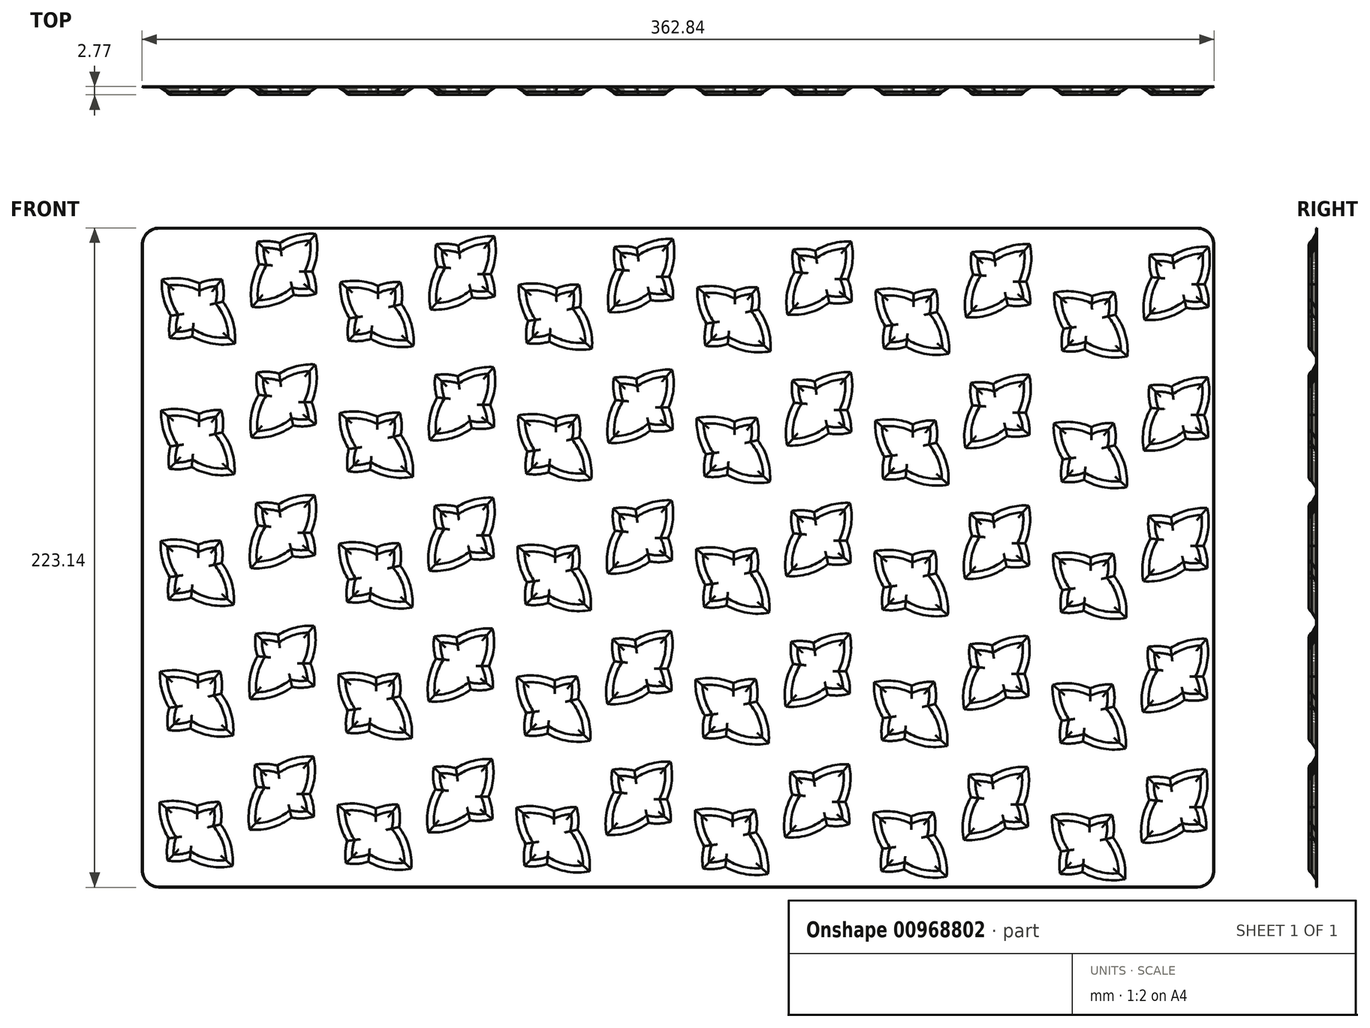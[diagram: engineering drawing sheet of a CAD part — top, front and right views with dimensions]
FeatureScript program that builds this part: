
annotation { "Feature Type Name" : "Feature", "Feature Type Description" : "" }
export const myFeature = defineFeature(function(context is Context, id is Id, definition is map)
    precondition{}
    {
        {
            var Q0;
            Q0=qCreatedBy(makeId("Front.planeOp"),FACE);
            var sketch = newSketch(context, id + "F0", { "sketchPlane" : qUnion([Q0])});
            skLineSegment(sketch, "E0.bottom", {"start": v(175.68, 113.88) * mm, "end": v(-175.68, 113.88) * mm});
            skLineSegment(sketch, "E0.top", {"start": v(175.68, -113.88) * mm, "end": v(-175.68, -113.88) * mm});
            skLineSegment(sketch, "E0.left", {"start": v(183.73, 105.83) * mm, "end": v(183.73, -105.83) * mm});
            skLineSegment(sketch, "E0.right", {"start": v(-183.73, 105.83) * mm, "end": v(-183.73, -105.83) * mm});
            skPoint(sketch, "E1.visualSharp", {"position": v(183.73, 113.88) * mm});
            skArc(sketch, "E1.filletArc", {"start": v(183.73, 105.83) * mm, "mid": v(181.37, 111.52) * mm, "end": v(175.68, 113.88) * mm});
            skPoint(sketch, "E2.visualSharp", {"position": v(-183.73, 113.88) * mm});
            skArc(sketch, "E2.filletArc", {"start": v(-175.68, 113.88) * mm, "mid": v(-181.37, 111.52) * mm, "end": v(-183.73, 105.83) * mm});
            skPoint(sketch, "E3.visualSharp", {"position": v(-183.73, -113.88) * mm});
            skArc(sketch, "E3.filletArc", {"start": v(-183.73, -105.83) * mm, "mid": v(-181.37, -111.52) * mm, "end": v(-175.68, -113.88) * mm});
            skPoint(sketch, "E4.visualSharp", {"position": v(183.73, -113.88) * mm});
            skArc(sketch, "E4.filletArc", {"start": v(175.68, -113.88) * mm, "mid": v(181.37, -111.52) * mm, "end": v(183.73, -105.83) * mm});
            skSolve(sketch);
        }
        {
            var Q0;
            Q0=makeQuery(id+"F0.imprint","IMPRINT",FACE,{"disambiguationData":[TD([[makeQuery(id+"F0.imprint","IMPRINT",EDGE,{"derivedFrom":sQuery(id+"F0.wireOp",EDGE,"E0.bottom")}),1.0]])]});
            var sketch = newSketch(context, id + "F1", { "sketchPlane" : qUnion([Q0])});
            skArc(sketch, "E5.0", {"start": v(-169.28, 82.17) * mm, "mid": v(-169.97, 79.25) * mm, "end": v(-170.06, 76.26) * mm});
            skArc(sketch, "E5.1", {"start": v(-170.4, 90.37) * mm, "mid": v(-169.2, 86.2) * mm, "end": v(-166.97, 82.48) * mm, "construction": true});
            skArc(sketch, "E5.2", {"start": v(-157.93, 89.73) * mm, "mid": v(-160.02, 89.11) * mm, "end": v(-161.98, 88.14) * mm, "construction": true});
            skArc(sketch, "E5.3", {"start": v(-152.04, 74.31) * mm, "mid": v(-153.16, 80.57) * mm, "end": v(-156.38, 86.05) * mm});
            skArc(sketch, "E5.4", {"start": v(-166.97, 82.48) * mm, "mid": v(-167.67, 80.45) * mm, "end": v(-168.03, 78.33) * mm, "construction": true});
            skArc(sketch, "E5.5", {"start": v(-154.2, 76.24) * mm, "mid": v(-155.66, 81.27) * mm, "end": v(-158.67, 85.56) * mm, "construction": true});
            skArc(sketch, "E5.6", {"start": v(-158.67, 85.56) * mm, "mid": v(-158.1, 87.6) * mm, "end": v(-157.93, 89.73) * mm, "construction": true});
            skArc(sketch, "E5.7", {"start": v(-163.98, 79.57) * mm, "mid": v(-159.36, 77.12) * mm, "end": v(-154.2, 76.24) * mm, "construction": true});
            skArc(sketch, "E5.8", {"start": v(-172.6, 92.24) * mm, "mid": v(-171.67, 86.96) * mm, "end": v(-169.28, 82.17) * mm});
            skArc(sketch, "E5.9", {"start": v(-161.98, 90.46) * mm, "mid": v(-167.16, 92.16) * mm, "end": v(-172.6, 92.24) * mm});
            skArc(sketch, "E5.10", {"start": v(-156.38, 86.05) * mm, "mid": v(-155.91, 89.01) * mm, "end": v(-156.12, 92) * mm});
            skArc(sketch, "E5.11", {"start": v(-168.03, 78.33) * mm, "mid": v(-165.95, 78.76) * mm, "end": v(-163.98, 79.57) * mm, "construction": true});
            skArc(sketch, "E5.12", {"start": v(-161.98, 88.14) * mm, "mid": v(-166.03, 89.84) * mm, "end": v(-170.4, 90.37) * mm, "construction": true});
            skArc(sketch, "E5.13", {"start": v(-156.12, 92) * mm, "mid": v(-159.13, 91.54) * mm, "end": v(-161.98, 90.46) * mm});
            skArc(sketch, "E5.14", {"start": v(-170.06, 76.26) * mm, "mid": v(-167.07, 76.41) * mm, "end": v(-164.2, 77.23) * mm});
            skArc(sketch, "E5.15", {"start": v(-164.2, 77.23) * mm, "mid": v(-158.37, 74.72) * mm, "end": v(-152.04, 74.31) * mm});
            skArc(sketch, "E6.0", {"start": v(-124.64, 90.96) * mm, "mid": v(-125.1, 93.98) * mm, "end": v(-126.18, 96.83) * mm});
            skArc(sketch, "E6.1", {"start": v(-138.3, 102.87) * mm, "mid": v(-137.88, 100.8) * mm, "end": v(-137.07, 98.83) * mm, "construction": true});
            skArc(sketch, "E6.2", {"start": v(-126.27, 105.24) * mm, "mid": v(-130.44, 104.05) * mm, "end": v(-134.16, 101.81) * mm, "construction": true});
            skArc(sketch, "E6.3", {"start": v(-131.08, 93.52) * mm, "mid": v(-129.03, 92.95) * mm, "end": v(-126.9, 92.78) * mm, "construction": true});
            skArc(sketch, "E6.4", {"start": v(-134.47, 104.12) * mm, "mid": v(-137.38, 104.82) * mm, "end": v(-140.38, 104.9) * mm});
            skArc(sketch, "E6.5", {"start": v(-139.4, 99.04) * mm, "mid": v(-141.92, 93.22) * mm, "end": v(-142.33, 86.89) * mm});
            skArc(sketch, "E6.6", {"start": v(-142.33, 86.89) * mm, "mid": v(-136.07, 88) * mm, "end": v(-130.58, 91.22) * mm});
            skArc(sketch, "E6.7", {"start": v(-128.5, 96.82) * mm, "mid": v(-126.8, 100.88) * mm, "end": v(-126.27, 105.24) * mm, "construction": true});
            skArc(sketch, "E6.8", {"start": v(-134.16, 101.81) * mm, "mid": v(-136.19, 102.52) * mm, "end": v(-138.3, 102.87) * mm, "construction": true});
            skArc(sketch, "E6.9", {"start": v(-140.4, 89.04) * mm, "mid": v(-135.37, 90.5) * mm, "end": v(-131.08, 93.52) * mm, "construction": true});
            skArc(sketch, "E6.10", {"start": v(-137.07, 98.83) * mm, "mid": v(-139.52, 94.2) * mm, "end": v(-140.4, 89.04) * mm, "construction": true});
            skArc(sketch, "E6.11", {"start": v(-126.9, 92.78) * mm, "mid": v(-127.53, 94.87) * mm, "end": v(-128.5, 96.82) * mm, "construction": true});
            skArc(sketch, "E6.12", {"start": v(-124.4, 107.44) * mm, "mid": v(-129.68, 106.51) * mm, "end": v(-134.47, 104.12) * mm});
            skArc(sketch, "E6.13", {"start": v(-140.38, 104.9) * mm, "mid": v(-140.22, 101.92) * mm, "end": v(-139.4, 99.04) * mm});
            skArc(sketch, "E6.14", {"start": v(-130.58, 91.22) * mm, "mid": v(-127.62, 90.76) * mm, "end": v(-124.64, 90.96) * mm});
            skArc(sketch, "E6.15", {"start": v(-126.18, 96.83) * mm, "mid": v(-124.48, 102) * mm, "end": v(-124.4, 107.44) * mm});
            skArc(sketch, "E7.0.1.0", {"start": v(-152.24, 30.1) * mm, "mid": v(-153.36, 36.35) * mm, "end": v(-156.57, 41.84) * mm});
            skArc(sketch, "E7.0.1.1", {"start": v(-156.57, 41.84) * mm, "mid": v(-156.1, 44.8) * mm, "end": v(-156.31, 47.79) * mm});
            skArc(sketch, "E7.0.1.2", {"start": v(-162.17, 43.93) * mm, "mid": v(-166.23, 45.62) * mm, "end": v(-170.6, 46.15) * mm, "construction": true});
            skArc(sketch, "E7.0.1.3", {"start": v(-164.18, 35.35) * mm, "mid": v(-159.55, 32.9) * mm, "end": v(-154.39, 32.02) * mm, "construction": true});
            skArc(sketch, "E7.0.1.4", {"start": v(-172.8, 48.02) * mm, "mid": v(-171.86, 42.75) * mm, "end": v(-169.47, 37.95) * mm});
            skArc(sketch, "E7.0.1.5", {"start": v(-139.6, 54.82) * mm, "mid": v(-142.11, 49) * mm, "end": v(-142.52, 42.67) * mm});
            skArc(sketch, "E7.0.1.6", {"start": v(-137.26, 54.61) * mm, "mid": v(-139.71, 49.98) * mm, "end": v(-140.6, 44.82) * mm, "construction": true});
            skArc(sketch, "E7.0.1.7", {"start": v(-164.39, 33.02) * mm, "mid": v(-158.57, 30.5) * mm, "end": v(-152.24, 30.1) * mm});
            skArc(sketch, "E7.0.1.8", {"start": v(-162.18, 46.24) * mm, "mid": v(-167.35, 47.94) * mm, "end": v(-172.8, 48.02) * mm});
            skArc(sketch, "E7.0.1.9", {"start": v(-140.6, 44.82) * mm, "mid": v(-135.56, 46.3) * mm, "end": v(-131.28, 49.3) * mm, "construction": true});
            skArc(sketch, "E7.0.1.10", {"start": v(-170.6, 46.15) * mm, "mid": v(-169.4, 41.98) * mm, "end": v(-167.17, 38.26) * mm, "construction": true});
            skArc(sketch, "E7.0.1.11", {"start": v(-154.39, 32.02) * mm, "mid": v(-155.86, 37.05) * mm, "end": v(-158.87, 41.34) * mm, "construction": true});
            skArc(sketch, "E7.0.1.12", {"start": v(-142.52, 42.67) * mm, "mid": v(-136.26, 43.8) * mm, "end": v(-130.78, 47) * mm});
            skArc(sketch, "E7.0.1.13", {"start": v(-124.83, 46.75) * mm, "mid": v(-125.3, 49.76) * mm, "end": v(-126.37, 52.61) * mm});
            skArc(sketch, "E7.0.1.14", {"start": v(-168.22, 34.12) * mm, "mid": v(-166.14, 34.54) * mm, "end": v(-164.18, 35.35) * mm, "construction": true});
            skArc(sketch, "E7.0.1.15", {"start": v(-158.13, 45.51) * mm, "mid": v(-160.22, 44.9) * mm, "end": v(-162.17, 43.93) * mm, "construction": true});
            skArc(sketch, "E7.0.1.16", {"start": v(-134.36, 57.6) * mm, "mid": v(-136.38, 58.3) * mm, "end": v(-138.5, 58.66) * mm, "construction": true});
            skArc(sketch, "E7.0.1.17", {"start": v(-127.1, 48.56) * mm, "mid": v(-127.72, 50.65) * mm, "end": v(-128.7, 52.6) * mm, "construction": true});
            skArc(sketch, "E7.0.1.18", {"start": v(-156.31, 47.79) * mm, "mid": v(-159.33, 47.32) * mm, "end": v(-162.18, 46.24) * mm});
            skArc(sketch, "E7.0.1.19", {"start": v(-170.26, 32.04) * mm, "mid": v(-167.27, 32.2) * mm, "end": v(-164.39, 33.02) * mm});
            skArc(sketch, "E7.0.1.20", {"start": v(-131.28, 49.3) * mm, "mid": v(-129.22, 48.74) * mm, "end": v(-127.1, 48.56) * mm, "construction": true});
            skArc(sketch, "E7.0.1.21", {"start": v(-167.17, 38.26) * mm, "mid": v(-167.87, 36.23) * mm, "end": v(-168.22, 34.12) * mm, "construction": true});
            skArc(sketch, "E7.0.1.22", {"start": v(-158.87, 41.34) * mm, "mid": v(-158.3, 43.4) * mm, "end": v(-158.13, 45.51) * mm, "construction": true});
            skArc(sketch, "E7.0.1.23", {"start": v(-130.78, 47) * mm, "mid": v(-127.82, 46.54) * mm, "end": v(-124.83, 46.75) * mm});
            skArc(sketch, "E7.0.1.24", {"start": v(-169.47, 37.95) * mm, "mid": v(-170.17, 35.04) * mm, "end": v(-170.26, 32.04) * mm});
            skArc(sketch, "E7.0.1.25", {"start": v(-138.5, 58.66) * mm, "mid": v(-138.07, 56.58) * mm, "end": v(-137.26, 54.61) * mm, "construction": true});
            skArc(sketch, "E7.0.1.26", {"start": v(-126.46, 61.03) * mm, "mid": v(-130.64, 59.83) * mm, "end": v(-134.36, 57.6) * mm, "construction": true});
            skArc(sketch, "E7.0.1.27", {"start": v(-124.6, 63.23) * mm, "mid": v(-129.87, 62.3) * mm, "end": v(-134.66, 59.9) * mm});
            skArc(sketch, "E7.0.1.28", {"start": v(-128.7, 52.6) * mm, "mid": v(-127, 56.66) * mm, "end": v(-126.46, 61.03) * mm, "construction": true});
            skArc(sketch, "E7.0.1.29", {"start": v(-126.37, 52.61) * mm, "mid": v(-124.68, 57.79) * mm, "end": v(-124.6, 63.23) * mm});
            skArc(sketch, "E7.0.1.30", {"start": v(-140.58, 60.7) * mm, "mid": v(-140.42, 57.7) * mm, "end": v(-139.6, 54.82) * mm});
            skArc(sketch, "E7.0.1.31", {"start": v(-134.66, 59.9) * mm, "mid": v(-137.58, 60.6) * mm, "end": v(-140.58, 60.7) * mm});
            skArc(sketch, "E7.0.2.0", {"start": v(-152.44, -14.12) * mm, "mid": v(-153.55, -7.86) * mm, "end": v(-156.77, -2.38) * mm});
            skArc(sketch, "E7.0.2.1", {"start": v(-156.77, -2.38) * mm, "mid": v(-156.3, 0.58) * mm, "end": v(-156.5, 3.57) * mm});
            skArc(sketch, "E7.0.2.2", {"start": v(-162.37, -0.29) * mm, "mid": v(-166.42, 1.4) * mm, "end": v(-170.79, 1.94) * mm, "construction": true});
            skArc(sketch, "E7.0.2.3", {"start": v(-164.37, -8.86) * mm, "mid": v(-159.75, -11.31) * mm, "end": v(-154.58, -12.2) * mm, "construction": true});
            skArc(sketch, "E7.0.2.4", {"start": v(-172.99, 3.8) * mm, "mid": v(-172.06, -1.47) * mm, "end": v(-169.67, -6.26) * mm});
            skArc(sketch, "E7.0.2.5", {"start": v(-139.8, 10.6) * mm, "mid": v(-142.3, 4.78) * mm, "end": v(-142.72, -1.54) * mm});
            skArc(sketch, "E7.0.2.6", {"start": v(-137.46, 10.4) * mm, "mid": v(-139.9, 5.77) * mm, "end": v(-140.8, 0.6) * mm, "construction": true});
            skArc(sketch, "E7.0.2.7", {"start": v(-164.58, -11.2) * mm, "mid": v(-158.76, -13.71) * mm, "end": v(-152.44, -14.12) * mm});
            skArc(sketch, "E7.0.2.8", {"start": v(-162.37, 2.03) * mm, "mid": v(-167.55, 3.72) * mm, "end": v(-172.99, 3.8) * mm});
            skArc(sketch, "E7.0.2.9", {"start": v(-140.8, 0.6) * mm, "mid": v(-135.76, 2.08) * mm, "end": v(-131.47, 5.09) * mm, "construction": true});
            skArc(sketch, "E7.0.2.10", {"start": v(-170.79, 1.94) * mm, "mid": v(-169.6, -2.24) * mm, "end": v(-167.36, -5.96) * mm, "construction": true});
            skArc(sketch, "E7.0.2.11", {"start": v(-154.58, -12.2) * mm, "mid": v(-156.05, -7.16) * mm, "end": v(-159.07, -2.87) * mm, "construction": true});
            skArc(sketch, "E7.0.2.12", {"start": v(-142.72, -1.54) * mm, "mid": v(-136.46, -0.42) * mm, "end": v(-130.97, 2.8) * mm});
            skArc(sketch, "E7.0.2.13", {"start": v(-125.03, 2.53) * mm, "mid": v(-125.5, 5.54) * mm, "end": v(-126.57, 8.4) * mm});
            skArc(sketch, "E7.0.2.14", {"start": v(-168.42, -10.1) * mm, "mid": v(-166.34, -9.67) * mm, "end": v(-164.37, -8.86) * mm, "construction": true});
            skArc(sketch, "E7.0.2.15", {"start": v(-158.32, 1.3) * mm, "mid": v(-160.41, 0.68) * mm, "end": v(-162.37, -0.29) * mm, "construction": true});
            skArc(sketch, "E7.0.2.16", {"start": v(-134.55, 13.38) * mm, "mid": v(-136.58, 14.09) * mm, "end": v(-138.7, 14.44) * mm, "construction": true});
            skArc(sketch, "E7.0.2.17", {"start": v(-127.3, 4.35) * mm, "mid": v(-127.92, 6.44) * mm, "end": v(-128.89, 8.4) * mm, "construction": true});
            skArc(sketch, "E7.0.2.18", {"start": v(-156.5, 3.57) * mm, "mid": v(-159.52, 3.1) * mm, "end": v(-162.37, 2.03) * mm});
            skArc(sketch, "E7.0.2.19", {"start": v(-170.45, -12.17) * mm, "mid": v(-167.46, -12.02) * mm, "end": v(-164.58, -11.2) * mm});
            skArc(sketch, "E7.0.2.20", {"start": v(-131.47, 5.09) * mm, "mid": v(-129.42, 4.52) * mm, "end": v(-127.3, 4.35) * mm, "construction": true});
            skArc(sketch, "E7.0.2.21", {"start": v(-167.36, -5.96) * mm, "mid": v(-168.07, -7.98) * mm, "end": v(-168.42, -10.1) * mm, "construction": true});
            skArc(sketch, "E7.0.2.22", {"start": v(-159.07, -2.87) * mm, "mid": v(-158.5, -0.82) * mm, "end": v(-158.32, 1.3) * mm, "construction": true});
            skArc(sketch, "E7.0.2.23", {"start": v(-130.97, 2.8) * mm, "mid": v(-128.02, 2.33) * mm, "end": v(-125.03, 2.53) * mm});
            skArc(sketch, "E7.0.2.24", {"start": v(-169.67, -6.26) * mm, "mid": v(-170.36, -9.18) * mm, "end": v(-170.45, -12.17) * mm});
            skArc(sketch, "E7.0.2.25", {"start": v(-138.7, 14.44) * mm, "mid": v(-138.27, 12.36) * mm, "end": v(-137.46, 10.4) * mm, "construction": true});
            skArc(sketch, "E7.0.2.26", {"start": v(-126.66, 16.81) * mm, "mid": v(-130.83, 15.62) * mm, "end": v(-134.55, 13.38) * mm, "construction": true});
            skArc(sketch, "E7.0.2.27", {"start": v(-124.8, 19.01) * mm, "mid": v(-130.07, 18.08) * mm, "end": v(-134.86, 15.69) * mm});
            skArc(sketch, "E7.0.2.28", {"start": v(-128.89, 8.4) * mm, "mid": v(-127.2, 12.45) * mm, "end": v(-126.66, 16.81) * mm, "construction": true});
            skArc(sketch, "E7.0.2.29", {"start": v(-126.57, 8.4) * mm, "mid": v(-124.87, 13.57) * mm, "end": v(-124.8, 19.01) * mm});
            skArc(sketch, "E7.0.2.30", {"start": v(-140.77, 16.48) * mm, "mid": v(-140.62, 13.49) * mm, "end": v(-139.8, 10.6) * mm});
            skArc(sketch, "E7.0.2.31", {"start": v(-134.86, 15.69) * mm, "mid": v(-137.78, 16.39) * mm, "end": v(-140.77, 16.48) * mm});
            skArc(sketch, "E7.0.3.0", {"start": v(-152.63, -58.33) * mm, "mid": v(-153.75, -52.08) * mm, "end": v(-156.96, -46.6) * mm});
            skArc(sketch, "E7.0.3.1", {"start": v(-156.96, -46.6) * mm, "mid": v(-156.5, -43.63) * mm, "end": v(-156.7, -40.65) * mm});
            skArc(sketch, "E7.0.3.2", {"start": v(-162.56, -44.5) * mm, "mid": v(-166.62, -42.8) * mm, "end": v(-170.98, -42.28) * mm, "construction": true});
            skArc(sketch, "E7.0.3.3", {"start": v(-164.57, -53.08) * mm, "mid": v(-159.94, -55.53) * mm, "end": v(-154.78, -56.4) * mm, "construction": true});
            skArc(sketch, "E7.0.3.4", {"start": v(-173.18, -40.41) * mm, "mid": v(-172.26, -45.69) * mm, "end": v(-169.86, -50.48) * mm});
            skArc(sketch, "E7.0.3.5", {"start": v(-140, -33.61) * mm, "mid": v(-142.5, -39.43) * mm, "end": v(-142.91, -45.76) * mm});
            skArc(sketch, "E7.0.3.6", {"start": v(-137.66, -33.82) * mm, "mid": v(-140.1, -38.45) * mm, "end": v(-140.99, -43.6) * mm, "construction": true});
            skArc(sketch, "E7.0.3.7", {"start": v(-164.78, -55.41) * mm, "mid": v(-158.96, -57.93) * mm, "end": v(-152.63, -58.33) * mm});
            skArc(sketch, "E7.0.3.8", {"start": v(-162.57, -42.19) * mm, "mid": v(-167.74, -40.5) * mm, "end": v(-173.18, -40.41) * mm});
            skArc(sketch, "E7.0.3.9", {"start": v(-140.99, -43.6) * mm, "mid": v(-135.96, -42.14) * mm, "end": v(-131.67, -39.13) * mm, "construction": true});
            skArc(sketch, "E7.0.3.10", {"start": v(-170.98, -42.28) * mm, "mid": v(-169.8, -46.45) * mm, "end": v(-167.56, -50.17) * mm, "construction": true});
            skArc(sketch, "E7.0.3.11", {"start": v(-154.78, -56.4) * mm, "mid": v(-156.25, -51.38) * mm, "end": v(-159.26, -47.09) * mm, "construction": true});
            skArc(sketch, "E7.0.3.12", {"start": v(-142.91, -45.76) * mm, "mid": v(-136.65, -44.64) * mm, "end": v(-131.17, -41.43) * mm});
            skArc(sketch, "E7.0.3.13", {"start": v(-125.22, -41.68) * mm, "mid": v(-125.69, -38.67) * mm, "end": v(-126.76, -35.82) * mm});
            skArc(sketch, "E7.0.3.14", {"start": v(-168.61, -54.31) * mm, "mid": v(-166.53, -53.89) * mm, "end": v(-164.57, -53.08) * mm, "construction": true});
            skArc(sketch, "E7.0.3.15", {"start": v(-158.52, -42.92) * mm, "mid": v(-160.6, -43.53) * mm, "end": v(-162.56, -44.5) * mm, "construction": true});
            skArc(sketch, "E7.0.3.16", {"start": v(-134.75, -30.83) * mm, "mid": v(-136.78, -30.13) * mm, "end": v(-138.9, -29.77) * mm, "construction": true});
            skArc(sketch, "E7.0.3.17", {"start": v(-127.5, -39.87) * mm, "mid": v(-128.11, -37.78) * mm, "end": v(-129.08, -35.82) * mm, "construction": true});
            skArc(sketch, "E7.0.3.18", {"start": v(-156.7, -40.65) * mm, "mid": v(-159.72, -41.1) * mm, "end": v(-162.57, -42.19) * mm});
            skArc(sketch, "E7.0.3.19", {"start": v(-170.65, -56.4) * mm, "mid": v(-167.66, -56.23) * mm, "end": v(-164.78, -55.41) * mm});
            skArc(sketch, "E7.0.3.20", {"start": v(-131.67, -39.13) * mm, "mid": v(-129.62, -39.7) * mm, "end": v(-127.5, -39.87) * mm, "construction": true});
            skArc(sketch, "E7.0.3.21", {"start": v(-167.56, -50.17) * mm, "mid": v(-168.26, -52.2) * mm, "end": v(-168.61, -54.31) * mm, "construction": true});
            skArc(sketch, "E7.0.3.22", {"start": v(-159.26, -47.09) * mm, "mid": v(-158.7, -45.04) * mm, "end": v(-158.52, -42.92) * mm, "construction": true});
            skArc(sketch, "E7.0.3.23", {"start": v(-131.17, -41.43) * mm, "mid": v(-128.21, -41.9) * mm, "end": v(-125.22, -41.68) * mm});
            skArc(sketch, "E7.0.3.24", {"start": v(-169.86, -50.48) * mm, "mid": v(-170.56, -53.4) * mm, "end": v(-170.65, -56.4) * mm});
            skArc(sketch, "E7.0.3.25", {"start": v(-138.9, -29.77) * mm, "mid": v(-138.46, -31.85) * mm, "end": v(-137.66, -33.82) * mm, "construction": true});
            skArc(sketch, "E7.0.3.26", {"start": v(-126.86, -27.4) * mm, "mid": v(-131.03, -28.6) * mm, "end": v(-134.75, -30.83) * mm, "construction": true});
            skArc(sketch, "E7.0.3.27", {"start": v(-124.99, -25.2) * mm, "mid": v(-130.26, -26.13) * mm, "end": v(-135.05, -28.53) * mm});
            skArc(sketch, "E7.0.3.28", {"start": v(-129.08, -35.82) * mm, "mid": v(-127.39, -31.77) * mm, "end": v(-126.86, -27.4) * mm, "construction": true});
            skArc(sketch, "E7.0.3.29", {"start": v(-126.76, -35.82) * mm, "mid": v(-125.07, -30.65) * mm, "end": v(-124.99, -25.2) * mm});
            skArc(sketch, "E7.0.3.30", {"start": v(-140.97, -27.74) * mm, "mid": v(-140.81, -30.73) * mm, "end": v(-140, -33.61) * mm});
            skArc(sketch, "E7.0.3.31", {"start": v(-135.05, -28.53) * mm, "mid": v(-137.97, -27.83) * mm, "end": v(-140.97, -27.74) * mm});
            skArc(sketch, "E7.0.4.0", {"start": v(-152.83, -102.55) * mm, "mid": v(-153.94, -96.3) * mm, "end": v(-157.16, -90.8) * mm});
            skArc(sketch, "E7.0.4.1", {"start": v(-157.16, -90.8) * mm, "mid": v(-156.7, -87.85) * mm, "end": v(-156.9, -84.86) * mm});
            skArc(sketch, "E7.0.4.2", {"start": v(-162.76, -88.72) * mm, "mid": v(-166.82, -87.02) * mm, "end": v(-171.18, -86.5) * mm, "construction": true});
            skArc(sketch, "E7.0.4.3", {"start": v(-164.77, -97.3) * mm, "mid": v(-160.14, -99.74) * mm, "end": v(-154.97, -100.62) * mm, "construction": true});
            skArc(sketch, "E7.0.4.4", {"start": v(-173.38, -84.63) * mm, "mid": v(-172.45, -89.9) * mm, "end": v(-170.06, -94.7) * mm});
            skArc(sketch, "E7.0.4.5", {"start": v(-140.19, -77.83) * mm, "mid": v(-142.7, -83.65) * mm, "end": v(-143.1, -89.97) * mm});
            skArc(sketch, "E7.0.4.6", {"start": v(-137.85, -78.03) * mm, "mid": v(-140.3, -82.66) * mm, "end": v(-141.18, -87.82) * mm, "construction": true});
            skArc(sketch, "E7.0.4.7", {"start": v(-164.97, -99.63) * mm, "mid": v(-159.15, -102.14) * mm, "end": v(-152.83, -102.55) * mm});
            skArc(sketch, "E7.0.4.8", {"start": v(-162.77, -86.4) * mm, "mid": v(-167.94, -84.7) * mm, "end": v(-173.38, -84.63) * mm});
            skArc(sketch, "E7.0.4.9", {"start": v(-141.18, -87.82) * mm, "mid": v(-136.15, -86.35) * mm, "end": v(-131.86, -83.34) * mm, "construction": true});
            skArc(sketch, "E7.0.4.10", {"start": v(-171.18, -86.5) * mm, "mid": v(-169.99, -90.67) * mm, "end": v(-167.75, -94.39) * mm, "construction": true});
            skArc(sketch, "E7.0.4.11", {"start": v(-154.97, -100.62) * mm, "mid": v(-156.45, -95.6) * mm, "end": v(-159.46, -91.3) * mm, "construction": true});
            skArc(sketch, "E7.0.4.12", {"start": v(-143.1, -89.97) * mm, "mid": v(-136.85, -88.85) * mm, "end": v(-131.37, -85.64) * mm});
            skArc(sketch, "E7.0.4.13", {"start": v(-125.42, -85.9) * mm, "mid": v(-125.88, -82.89) * mm, "end": v(-126.96, -80.03) * mm});
            skArc(sketch, "E7.0.4.14", {"start": v(-168.8, -98.53) * mm, "mid": v(-166.73, -98.1) * mm, "end": v(-164.77, -97.3) * mm, "construction": true});
            skArc(sketch, "E7.0.4.15", {"start": v(-158.71, -87.13) * mm, "mid": v(-160.8, -87.75) * mm, "end": v(-162.76, -88.72) * mm, "construction": true});
            skArc(sketch, "E7.0.4.16", {"start": v(-134.94, -75.05) * mm, "mid": v(-136.97, -74.34) * mm, "end": v(-139.09, -73.99) * mm, "construction": true});
            skArc(sketch, "E7.0.4.17", {"start": v(-127.69, -84.09) * mm, "mid": v(-128.3, -82) * mm, "end": v(-129.28, -80.04) * mm, "construction": true});
            skArc(sketch, "E7.0.4.18", {"start": v(-156.9, -84.86) * mm, "mid": v(-159.91, -85.33) * mm, "end": v(-162.77, -86.4) * mm});
            skArc(sketch, "E7.0.4.19", {"start": v(-170.84, -100.6) * mm, "mid": v(-167.85, -100.45) * mm, "end": v(-164.97, -99.63) * mm});
            skArc(sketch, "E7.0.4.20", {"start": v(-131.86, -83.34) * mm, "mid": v(-129.81, -83.91) * mm, "end": v(-127.69, -84.09) * mm, "construction": true});
            skArc(sketch, "E7.0.4.21", {"start": v(-167.75, -94.39) * mm, "mid": v(-168.46, -96.41) * mm, "end": v(-168.8, -98.53) * mm, "construction": true});
            skArc(sketch, "E7.0.4.22", {"start": v(-159.46, -91.3) * mm, "mid": v(-158.89, -89.25) * mm, "end": v(-158.71, -87.13) * mm, "construction": true});
            skArc(sketch, "E7.0.4.23", {"start": v(-131.37, -85.64) * mm, "mid": v(-128.4, -86.1) * mm, "end": v(-125.42, -85.9) * mm});
            skArc(sketch, "E7.0.4.24", {"start": v(-170.06, -94.7) * mm, "mid": v(-170.75, -97.6) * mm, "end": v(-170.84, -100.6) * mm});
            skArc(sketch, "E7.0.4.25", {"start": v(-139.09, -73.99) * mm, "mid": v(-138.66, -76.07) * mm, "end": v(-137.85, -78.03) * mm, "construction": true});
            skArc(sketch, "E7.0.4.26", {"start": v(-127.05, -71.62) * mm, "mid": v(-131.22, -72.81) * mm, "end": v(-134.94, -75.05) * mm, "construction": true});
            skArc(sketch, "E7.0.4.27", {"start": v(-125.18, -69.42) * mm, "mid": v(-130.46, -70.35) * mm, "end": v(-135.25, -72.74) * mm});
            skArc(sketch, "E7.0.4.28", {"start": v(-129.28, -80.04) * mm, "mid": v(-127.58, -75.98) * mm, "end": v(-127.05, -71.62) * mm, "construction": true});
            skArc(sketch, "E7.0.4.29", {"start": v(-126.96, -80.03) * mm, "mid": v(-125.26, -74.86) * mm, "end": v(-125.18, -69.42) * mm});
            skArc(sketch, "E7.0.4.30", {"start": v(-141.16, -71.95) * mm, "mid": v(-141, -74.95) * mm, "end": v(-140.19, -77.83) * mm});
            skArc(sketch, "E7.0.4.31", {"start": v(-135.25, -72.74) * mm, "mid": v(-138.17, -72.04) * mm, "end": v(-141.16, -71.95) * mm});
            skArc(sketch, "E7.1.0.0", {"start": v(-91.63, 73.43) * mm, "mid": v(-92.75, 79.7) * mm, "end": v(-95.97, 85.18) * mm});
            skArc(sketch, "E7.1.0.1", {"start": v(-95.97, 85.18) * mm, "mid": v(-95.5, 88.13) * mm, "end": v(-95.7, 91.12) * mm});
            skArc(sketch, "E7.1.0.2", {"start": v(-101.57, 87.26) * mm, "mid": v(-105.62, 88.96) * mm, "end": v(-109.99, 89.49) * mm, "construction": true});
            skArc(sketch, "E7.1.0.3", {"start": v(-103.57, 78.69) * mm, "mid": v(-98.95, 76.24) * mm, "end": v(-93.78, 75.36) * mm, "construction": true});
            skArc(sketch, "E7.1.0.4", {"start": v(-112.19, 91.36) * mm, "mid": v(-111.26, 86.08) * mm, "end": v(-108.87, 81.3) * mm});
            skArc(sketch, "E7.1.0.5", {"start": v(-79, 98.16) * mm, "mid": v(-81.5, 92.34) * mm, "end": v(-81.92, 86.01) * mm});
            skArc(sketch, "E7.1.0.6", {"start": v(-76.66, 97.95) * mm, "mid": v(-79.1, 93.32) * mm, "end": v(-79.99, 88.16) * mm, "construction": true});
            skArc(sketch, "E7.1.0.7", {"start": v(-103.78, 76.35) * mm, "mid": v(-97.96, 73.84) * mm, "end": v(-91.63, 73.43) * mm});
            skArc(sketch, "E7.1.0.8", {"start": v(-101.57, 89.58) * mm, "mid": v(-106.75, 91.28) * mm, "end": v(-112.19, 91.36) * mm});
            skArc(sketch, "E7.1.0.9", {"start": v(-79.99, 88.16) * mm, "mid": v(-74.96, 89.63) * mm, "end": v(-70.67, 92.64) * mm, "construction": true});
            skArc(sketch, "E7.1.0.10", {"start": v(-109.99, 89.49) * mm, "mid": v(-108.8, 85.32) * mm, "end": v(-106.56, 81.6) * mm, "construction": true});
            skArc(sketch, "E7.1.0.11", {"start": v(-93.78, 75.36) * mm, "mid": v(-95.25, 80.39) * mm, "end": v(-98.26, 84.68) * mm, "construction": true});
            skArc(sketch, "E7.1.0.12", {"start": v(-81.92, 86.01) * mm, "mid": v(-75.66, 87.13) * mm, "end": v(-70.17, 90.34) * mm});
            skArc(sketch, "E7.1.0.13", {"start": v(-64.23, 90.08) * mm, "mid": v(-64.7, 93.1) * mm, "end": v(-65.77, 95.95) * mm});
            skArc(sketch, "E7.1.0.14", {"start": v(-107.62, 77.45) * mm, "mid": v(-105.54, 77.88) * mm, "end": v(-103.57, 78.69) * mm, "construction": true});
            skArc(sketch, "E7.1.0.15", {"start": v(-97.52, 88.85) * mm, "mid": v(-99.61, 88.23) * mm, "end": v(-101.57, 87.26) * mm, "construction": true});
            skArc(sketch, "E7.1.0.16", {"start": v(-73.75, 100.94) * mm, "mid": v(-75.78, 101.64) * mm, "end": v(-77.9, 102) * mm, "construction": true});
            skArc(sketch, "E7.1.0.17", {"start": v(-66.5, 91.9) * mm, "mid": v(-67.12, 93.99) * mm, "end": v(-68.09, 95.94) * mm, "construction": true});
            skArc(sketch, "E7.1.0.18", {"start": v(-95.7, 91.12) * mm, "mid": v(-98.72, 90.66) * mm, "end": v(-101.57, 89.58) * mm});
            skArc(sketch, "E7.1.0.19", {"start": v(-109.65, 75.38) * mm, "mid": v(-106.66, 75.53) * mm, "end": v(-103.78, 76.35) * mm});
            skArc(sketch, "E7.1.0.20", {"start": v(-70.67, 92.64) * mm, "mid": v(-68.62, 92.07) * mm, "end": v(-66.5, 91.9) * mm, "construction": true});
            skArc(sketch, "E7.1.0.21", {"start": v(-106.56, 81.6) * mm, "mid": v(-107.26, 79.57) * mm, "end": v(-107.62, 77.45) * mm, "construction": true});
            skArc(sketch, "E7.1.0.22", {"start": v(-98.26, 84.68) * mm, "mid": v(-97.7, 86.73) * mm, "end": v(-97.52, 88.85) * mm, "construction": true});
            skArc(sketch, "E7.1.0.23", {"start": v(-70.17, 90.34) * mm, "mid": v(-67.21, 89.88) * mm, "end": v(-64.23, 90.08) * mm});
            skArc(sketch, "E7.1.0.24", {"start": v(-108.87, 81.3) * mm, "mid": v(-109.56, 78.37) * mm, "end": v(-109.65, 75.38) * mm});
            skArc(sketch, "E7.1.0.25", {"start": v(-77.9, 102) * mm, "mid": v(-77.47, 99.91) * mm, "end": v(-76.66, 97.95) * mm, "construction": true});
            skArc(sketch, "E7.1.0.26", {"start": v(-65.86, 104.36) * mm, "mid": v(-70.03, 103.17) * mm, "end": v(-73.75, 100.94) * mm, "construction": true});
            skArc(sketch, "E7.1.0.27", {"start": v(-64, 106.56) * mm, "mid": v(-69.27, 105.64) * mm, "end": v(-74.06, 103.24) * mm});
            skArc(sketch, "E7.1.0.28", {"start": v(-68.09, 95.94) * mm, "mid": v(-66.4, 100) * mm, "end": v(-65.86, 104.36) * mm, "construction": true});
            skArc(sketch, "E7.1.0.29", {"start": v(-65.77, 95.95) * mm, "mid": v(-64.07, 101.12) * mm, "end": v(-64, 106.56) * mm});
            skArc(sketch, "E7.1.0.30", {"start": v(-79.97, 104.03) * mm, "mid": v(-79.81, 101.04) * mm, "end": v(-79, 98.16) * mm});
            skArc(sketch, "E7.1.0.31", {"start": v(-74.06, 103.24) * mm, "mid": v(-76.97, 103.94) * mm, "end": v(-79.97, 104.03) * mm});
            skArc(sketch, "E7.1.1.0", {"start": v(-91.83, 29.22) * mm, "mid": v(-92.95, 35.47) * mm, "end": v(-96.16, 40.96) * mm});
            skArc(sketch, "E7.1.1.1", {"start": v(-96.16, 40.96) * mm, "mid": v(-95.7, 43.92) * mm, "end": v(-95.9, 46.9) * mm});
            skArc(sketch, "E7.1.1.2", {"start": v(-101.76, 43.05) * mm, "mid": v(-105.82, 44.74) * mm, "end": v(-110.18, 45.27) * mm, "construction": true});
            skArc(sketch, "E7.1.1.3", {"start": v(-103.77, 34.47) * mm, "mid": v(-99.14, 32.02) * mm, "end": v(-93.98, 31.14) * mm, "construction": true});
            skArc(sketch, "E7.1.1.4", {"start": v(-112.38, 47.14) * mm, "mid": v(-111.45, 41.87) * mm, "end": v(-109.06, 37.08) * mm});
            skArc(sketch, "E7.1.1.5", {"start": v(-79.2, 53.94) * mm, "mid": v(-81.7, 48.12) * mm, "end": v(-82.11, 41.8) * mm});
            skArc(sketch, "E7.1.1.6", {"start": v(-76.85, 53.73) * mm, "mid": v(-79.3, 49.1) * mm, "end": v(-80.18, 43.94) * mm, "construction": true});
            skArc(sketch, "E7.1.1.7", {"start": v(-103.98, 32.14) * mm, "mid": v(-98.16, 29.63) * mm, "end": v(-91.83, 29.22) * mm});
            skArc(sketch, "E7.1.1.8", {"start": v(-101.77, 45.37) * mm, "mid": v(-106.94, 47.06) * mm, "end": v(-112.38, 47.14) * mm});
            skArc(sketch, "E7.1.1.9", {"start": v(-80.18, 43.94) * mm, "mid": v(-75.15, 45.41) * mm, "end": v(-70.87, 48.43) * mm, "construction": true});
            skArc(sketch, "E7.1.1.10", {"start": v(-110.18, 45.27) * mm, "mid": v(-109, 41.1) * mm, "end": v(-106.76, 37.38) * mm, "construction": true});
            skArc(sketch, "E7.1.1.11", {"start": v(-93.98, 31.14) * mm, "mid": v(-95.45, 36.17) * mm, "end": v(-98.46, 40.46) * mm, "construction": true});
            skArc(sketch, "E7.1.1.12", {"start": v(-82.11, 41.8) * mm, "mid": v(-75.85, 42.91) * mm, "end": v(-70.37, 46.13) * mm});
            skArc(sketch, "E7.1.1.13", {"start": v(-64.42, 45.87) * mm, "mid": v(-64.89, 48.88) * mm, "end": v(-65.96, 51.73) * mm});
            skArc(sketch, "E7.1.1.14", {"start": v(-107.81, 33.24) * mm, "mid": v(-105.73, 33.67) * mm, "end": v(-103.77, 34.47) * mm, "construction": true});
            skArc(sketch, "E7.1.1.15", {"start": v(-97.72, 44.64) * mm, "mid": v(-99.8, 44.02) * mm, "end": v(-101.76, 43.05) * mm, "construction": true});
            skArc(sketch, "E7.1.1.16", {"start": v(-73.95, 56.72) * mm, "mid": v(-75.97, 57.43) * mm, "end": v(-78.1, 57.78) * mm, "construction": true});
            skArc(sketch, "E7.1.1.17", {"start": v(-66.7, 47.68) * mm, "mid": v(-67.31, 49.77) * mm, "end": v(-68.28, 51.73) * mm, "construction": true});
            skArc(sketch, "E7.1.1.18", {"start": v(-95.9, 46.9) * mm, "mid": v(-98.92, 46.44) * mm, "end": v(-101.77, 45.37) * mm});
            skArc(sketch, "E7.1.1.19", {"start": v(-109.85, 31.16) * mm, "mid": v(-106.86, 31.32) * mm, "end": v(-103.98, 32.14) * mm});
            skArc(sketch, "E7.1.1.20", {"start": v(-70.87, 48.43) * mm, "mid": v(-68.81, 47.86) * mm, "end": v(-66.7, 47.68) * mm, "construction": true});
            skArc(sketch, "E7.1.1.21", {"start": v(-106.76, 37.38) * mm, "mid": v(-107.46, 35.35) * mm, "end": v(-107.81, 33.24) * mm, "construction": true});
            skArc(sketch, "E7.1.1.22", {"start": v(-98.46, 40.46) * mm, "mid": v(-97.9, 42.51) * mm, "end": v(-97.72, 44.64) * mm, "construction": true});
            skArc(sketch, "E7.1.1.23", {"start": v(-70.37, 46.13) * mm, "mid": v(-67.41, 45.66) * mm, "end": v(-64.42, 45.87) * mm});
            skArc(sketch, "E7.1.1.24", {"start": v(-109.06, 37.08) * mm, "mid": v(-109.76, 34.16) * mm, "end": v(-109.85, 31.16) * mm});
            skArc(sketch, "E7.1.1.25", {"start": v(-78.1, 57.78) * mm, "mid": v(-77.66, 55.7) * mm, "end": v(-76.85, 53.73) * mm, "construction": true});
            skArc(sketch, "E7.1.1.26", {"start": v(-66.05, 60.15) * mm, "mid": v(-70.23, 58.96) * mm, "end": v(-73.95, 56.72) * mm, "construction": true});
            skArc(sketch, "E7.1.1.27", {"start": v(-64.19, 62.35) * mm, "mid": v(-69.46, 61.42) * mm, "end": v(-74.25, 59.03) * mm});
            skArc(sketch, "E7.1.1.28", {"start": v(-68.28, 51.73) * mm, "mid": v(-66.59, 55.78) * mm, "end": v(-66.05, 60.15) * mm, "construction": true});
            skArc(sketch, "E7.1.1.29", {"start": v(-65.96, 51.73) * mm, "mid": v(-64.27, 56.9) * mm, "end": v(-64.19, 62.35) * mm});
            skArc(sketch, "E7.1.1.30", {"start": v(-80.17, 59.81) * mm, "mid": v(-80.01, 56.82) * mm, "end": v(-79.2, 53.94) * mm});
            skArc(sketch, "E7.1.1.31", {"start": v(-74.25, 59.03) * mm, "mid": v(-77.17, 59.72) * mm, "end": v(-80.17, 59.81) * mm});
            skArc(sketch, "E7.1.2.0", {"start": v(-92.03, -15) * mm, "mid": v(-93.14, -8.74) * mm, "end": v(-96.36, -3.26) * mm});
            skArc(sketch, "E7.1.2.1", {"start": v(-96.36, -3.26) * mm, "mid": v(-95.9, -0.3) * mm, "end": v(-96.1, 2.7) * mm});
            skArc(sketch, "E7.1.2.2", {"start": v(-101.96, -1.17) * mm, "mid": v(-106.01, 0.53) * mm, "end": v(-110.38, 1.06) * mm, "construction": true});
            skArc(sketch, "E7.1.2.3", {"start": v(-103.96, -9.74) * mm, "mid": v(-99.34, -12.2) * mm, "end": v(-94.17, -13.07) * mm, "construction": true});
            skArc(sketch, "E7.1.2.4", {"start": v(-112.58, 2.93) * mm, "mid": v(-111.65, -2.35) * mm, "end": v(-109.26, -7.14) * mm});
            skArc(sketch, "E7.1.2.5", {"start": v(-79.39, 9.73) * mm, "mid": v(-81.9, 3.9) * mm, "end": v(-82.3, -2.42) * mm});
            skArc(sketch, "E7.1.2.6", {"start": v(-77.05, 9.52) * mm, "mid": v(-79.5, 4.9) * mm, "end": v(-80.38, -0.27) * mm, "construction": true});
            skArc(sketch, "E7.1.2.7", {"start": v(-104.17, -12.08) * mm, "mid": v(-98.35, -14.59) * mm, "end": v(-92.03, -15) * mm});
            skArc(sketch, "E7.1.2.8", {"start": v(-101.96, 1.15) * mm, "mid": v(-107.14, 2.85) * mm, "end": v(-112.58, 2.93) * mm});
            skArc(sketch, "E7.1.2.9", {"start": v(-80.38, -0.27) * mm, "mid": v(-75.35, 1.2) * mm, "end": v(-71.06, 4.2) * mm, "construction": true});
            skArc(sketch, "E7.1.2.10", {"start": v(-110.38, 1.06) * mm, "mid": v(-109.19, -3.11) * mm, "end": v(-106.95, -6.83) * mm, "construction": true});
            skArc(sketch, "E7.1.2.11", {"start": v(-94.17, -13.07) * mm, "mid": v(-95.64, -8.04) * mm, "end": v(-98.66, -3.75) * mm, "construction": true});
            skArc(sketch, "E7.1.2.12", {"start": v(-82.3, -2.42) * mm, "mid": v(-76.05, -1.3) * mm, "end": v(-70.56, 1.91) * mm});
            skArc(sketch, "E7.1.2.13", {"start": v(-64.62, 1.65) * mm, "mid": v(-65.08, 4.67) * mm, "end": v(-66.16, 7.52) * mm});
            skArc(sketch, "E7.1.2.14", {"start": v(-108, -10.98) * mm, "mid": v(-105.93, -10.55) * mm, "end": v(-103.96, -9.74) * mm, "construction": true});
            skArc(sketch, "E7.1.2.15", {"start": v(-97.91, 0.42) * mm, "mid": v(-100, -0.2) * mm, "end": v(-101.96, -1.17) * mm, "construction": true});
            skArc(sketch, "E7.1.2.16", {"start": v(-74.14, 12.5) * mm, "mid": v(-76.17, 13.2) * mm, "end": v(-78.29, 13.56) * mm, "construction": true});
            skArc(sketch, "E7.1.2.17", {"start": v(-66.89, 3.47) * mm, "mid": v(-67.5, 5.56) * mm, "end": v(-68.48, 7.51) * mm, "construction": true});
            skArc(sketch, "E7.1.2.18", {"start": v(-96.1, 2.7) * mm, "mid": v(-99.11, 2.23) * mm, "end": v(-101.96, 1.15) * mm});
            skArc(sketch, "E7.1.2.19", {"start": v(-110.04, -13.05) * mm, "mid": v(-107.05, -12.9) * mm, "end": v(-104.17, -12.08) * mm});
            skArc(sketch, "E7.1.2.20", {"start": v(-71.06, 4.2) * mm, "mid": v(-69, 3.64) * mm, "end": v(-66.89, 3.47) * mm, "construction": true});
            skArc(sketch, "E7.1.2.21", {"start": v(-106.95, -6.83) * mm, "mid": v(-107.66, -8.86) * mm, "end": v(-108, -10.98) * mm, "construction": true});
            skArc(sketch, "E7.1.2.22", {"start": v(-98.66, -3.75) * mm, "mid": v(-98.09, -1.7) * mm, "end": v(-97.91, 0.42) * mm, "construction": true});
            skArc(sketch, "E7.1.2.23", {"start": v(-70.56, 1.91) * mm, "mid": v(-67.6, 1.45) * mm, "end": v(-64.62, 1.65) * mm});
            skArc(sketch, "E7.1.2.24", {"start": v(-109.26, -7.14) * mm, "mid": v(-109.95, -10.06) * mm, "end": v(-110.04, -13.05) * mm});
            skArc(sketch, "E7.1.2.25", {"start": v(-78.29, 13.56) * mm, "mid": v(-77.86, 11.48) * mm, "end": v(-77.05, 9.52) * mm, "construction": true});
            skArc(sketch, "E7.1.2.26", {"start": v(-66.25, 15.93) * mm, "mid": v(-70.42, 14.74) * mm, "end": v(-74.14, 12.5) * mm, "construction": true});
            skArc(sketch, "E7.1.2.27", {"start": v(-64.38, 18.13) * mm, "mid": v(-69.66, 17.2) * mm, "end": v(-74.45, 14.81) * mm});
            skArc(sketch, "E7.1.2.28", {"start": v(-68.48, 7.51) * mm, "mid": v(-66.78, 11.57) * mm, "end": v(-66.25, 15.93) * mm, "construction": true});
            skArc(sketch, "E7.1.2.29", {"start": v(-66.16, 7.52) * mm, "mid": v(-64.46, 12.7) * mm, "end": v(-64.38, 18.13) * mm});
            skArc(sketch, "E7.1.2.30", {"start": v(-80.36, 15.6) * mm, "mid": v(-80.2, 12.6) * mm, "end": v(-79.39, 9.73) * mm});
            skArc(sketch, "E7.1.2.31", {"start": v(-74.45, 14.81) * mm, "mid": v(-77.37, 15.5) * mm, "end": v(-80.36, 15.6) * mm});
            skArc(sketch, "E7.1.3.0", {"start": v(-92.22, -59.21) * mm, "mid": v(-93.34, -52.96) * mm, "end": v(-96.55, -47.47) * mm});
            skArc(sketch, "E7.1.3.1", {"start": v(-96.55, -47.47) * mm, "mid": v(-96.09, -44.51) * mm, "end": v(-96.3, -41.52) * mm});
            skArc(sketch, "E7.1.3.2", {"start": v(-102.15, -45.38) * mm, "mid": v(-106.21, -43.69) * mm, "end": v(-110.57, -43.16) * mm, "construction": true});
            skArc(sketch, "E7.1.3.3", {"start": v(-104.16, -53.96) * mm, "mid": v(-99.53, -56.4) * mm, "end": v(-94.37, -57.29) * mm, "construction": true});
            skArc(sketch, "E7.1.3.4", {"start": v(-112.77, -41.29) * mm, "mid": v(-111.85, -46.56) * mm, "end": v(-109.45, -51.35) * mm});
            skArc(sketch, "E7.1.3.5", {"start": v(-79.58, -34.49) * mm, "mid": v(-82.1, -40.31) * mm, "end": v(-82.5, -46.64) * mm});
            skArc(sketch, "E7.1.3.6", {"start": v(-77.25, -34.7) * mm, "mid": v(-79.7, -39.32) * mm, "end": v(-80.58, -44.49) * mm, "construction": true});
            skArc(sketch, "E7.1.3.7", {"start": v(-104.37, -56.3) * mm, "mid": v(-98.55, -58.8) * mm, "end": v(-92.22, -59.21) * mm});
            skArc(sketch, "E7.1.3.8", {"start": v(-102.16, -43.07) * mm, "mid": v(-107.33, -41.37) * mm, "end": v(-112.77, -41.29) * mm});
            skArc(sketch, "E7.1.3.9", {"start": v(-80.58, -44.49) * mm, "mid": v(-75.55, -43.02) * mm, "end": v(-71.26, -40) * mm, "construction": true});
            skArc(sketch, "E7.1.3.10", {"start": v(-110.57, -43.16) * mm, "mid": v(-109.38, -47.33) * mm, "end": v(-107.15, -51.05) * mm, "construction": true});
            skArc(sketch, "E7.1.3.11", {"start": v(-94.37, -57.29) * mm, "mid": v(-95.84, -52.26) * mm, "end": v(-98.85, -47.97) * mm, "construction": true});
            skArc(sketch, "E7.1.3.12", {"start": v(-82.5, -46.64) * mm, "mid": v(-76.24, -45.52) * mm, "end": v(-70.76, -42.3) * mm});
            skArc(sketch, "E7.1.3.13", {"start": v(-64.81, -42.56) * mm, "mid": v(-65.28, -39.55) * mm, "end": v(-66.35, -36.7) * mm});
            skArc(sketch, "E7.1.3.14", {"start": v(-108.2, -55.2) * mm, "mid": v(-106.12, -54.77) * mm, "end": v(-104.16, -53.96) * mm, "construction": true});
            skArc(sketch, "E7.1.3.15", {"start": v(-98.1, -43.8) * mm, "mid": v(-100.2, -44.41) * mm, "end": v(-102.15, -45.38) * mm, "construction": true});
            skArc(sketch, "E7.1.3.16", {"start": v(-74.34, -31.71) * mm, "mid": v(-76.37, -31) * mm, "end": v(-78.48, -30.65) * mm, "construction": true});
            skArc(sketch, "E7.1.3.17", {"start": v(-67.08, -40.75) * mm, "mid": v(-67.7, -38.66) * mm, "end": v(-68.67, -36.7) * mm, "construction": true});
            skArc(sketch, "E7.1.3.18", {"start": v(-96.3, -41.52) * mm, "mid": v(-99.3, -41.99) * mm, "end": v(-102.16, -43.07) * mm});
            skArc(sketch, "E7.1.3.19", {"start": v(-110.24, -57.27) * mm, "mid": v(-107.25, -57.11) * mm, "end": v(-104.37, -56.3) * mm});
            skArc(sketch, "E7.1.3.20", {"start": v(-71.26, -40) * mm, "mid": v(-69.2, -40.57) * mm, "end": v(-67.08, -40.75) * mm, "construction": true});
            skArc(sketch, "E7.1.3.21", {"start": v(-107.15, -51.05) * mm, "mid": v(-107.85, -53.08) * mm, "end": v(-108.2, -55.2) * mm, "construction": true});
            skArc(sketch, "E7.1.3.22", {"start": v(-98.85, -47.97) * mm, "mid": v(-98.28, -45.92) * mm, "end": v(-98.1, -43.8) * mm, "construction": true});
            skArc(sketch, "E7.1.3.23", {"start": v(-70.76, -42.3) * mm, "mid": v(-67.8, -42.77) * mm, "end": v(-64.81, -42.56) * mm});
            skArc(sketch, "E7.1.3.24", {"start": v(-109.45, -51.35) * mm, "mid": v(-110.15, -54.27) * mm, "end": v(-110.24, -57.27) * mm});
            skArc(sketch, "E7.1.3.25", {"start": v(-78.48, -30.65) * mm, "mid": v(-78.05, -32.73) * mm, "end": v(-77.25, -34.7) * mm, "construction": true});
            skArc(sketch, "E7.1.3.26", {"start": v(-66.45, -28.28) * mm, "mid": v(-70.62, -29.47) * mm, "end": v(-74.34, -31.71) * mm, "construction": true});
            skArc(sketch, "E7.1.3.27", {"start": v(-64.58, -26.08) * mm, "mid": v(-69.85, -27.01) * mm, "end": v(-74.64, -29.4) * mm});
            skArc(sketch, "E7.1.3.28", {"start": v(-68.67, -36.7) * mm, "mid": v(-66.98, -32.65) * mm, "end": v(-66.45, -28.28) * mm, "construction": true});
            skArc(sketch, "E7.1.3.29", {"start": v(-66.35, -36.7) * mm, "mid": v(-64.66, -31.52) * mm, "end": v(-64.58, -26.08) * mm});
            skArc(sketch, "E7.1.3.30", {"start": v(-80.56, -28.62) * mm, "mid": v(-80.4, -31.6) * mm, "end": v(-79.58, -34.49) * mm});
            skArc(sketch, "E7.1.3.31", {"start": v(-74.64, -29.4) * mm, "mid": v(-77.56, -28.7) * mm, "end": v(-80.56, -28.62) * mm});
            skArc(sketch, "E7.1.4.0", {"start": v(-92.42, -103.43) * mm, "mid": v(-93.53, -97.17) * mm, "end": v(-96.75, -91.69) * mm});
            skArc(sketch, "E7.1.4.1", {"start": v(-96.75, -91.69) * mm, "mid": v(-96.28, -88.73) * mm, "end": v(-96.49, -85.74) * mm});
            skArc(sketch, "E7.1.4.2", {"start": v(-102.35, -89.6) * mm, "mid": v(-106.4, -87.9) * mm, "end": v(-110.77, -87.37) * mm, "construction": true});
            skArc(sketch, "E7.1.4.3", {"start": v(-104.36, -98.17) * mm, "mid": v(-99.73, -100.62) * mm, "end": v(-94.56, -101.5) * mm, "construction": true});
            skArc(sketch, "E7.1.4.4", {"start": v(-112.97, -85.5) * mm, "mid": v(-112.04, -90.78) * mm, "end": v(-109.65, -95.57) * mm});
            skArc(sketch, "E7.1.4.5", {"start": v(-79.78, -78.7) * mm, "mid": v(-82.29, -84.53) * mm, "end": v(-82.7, -90.85) * mm});
            skArc(sketch, "E7.1.4.6", {"start": v(-77.44, -78.91) * mm, "mid": v(-79.9, -83.54) * mm, "end": v(-80.77, -88.7) * mm, "construction": true});
            skArc(sketch, "E7.1.4.7", {"start": v(-104.56, -100.5) * mm, "mid": v(-98.74, -103.02) * mm, "end": v(-92.42, -103.43) * mm});
            skArc(sketch, "E7.1.4.8", {"start": v(-102.36, -87.28) * mm, "mid": v(-107.53, -85.59) * mm, "end": v(-112.97, -85.5) * mm});
            skArc(sketch, "E7.1.4.9", {"start": v(-80.77, -88.7) * mm, "mid": v(-75.74, -87.23) * mm, "end": v(-71.45, -84.22) * mm, "construction": true});
            skArc(sketch, "E7.1.4.10", {"start": v(-110.77, -87.37) * mm, "mid": v(-109.58, -91.55) * mm, "end": v(-107.34, -95.27) * mm, "construction": true});
            skArc(sketch, "E7.1.4.11", {"start": v(-94.56, -101.5) * mm, "mid": v(-96.04, -96.47) * mm, "end": v(-99.05, -92.18) * mm, "construction": true});
            skArc(sketch, "E7.1.4.12", {"start": v(-82.7, -90.85) * mm, "mid": v(-76.44, -89.73) * mm, "end": v(-70.96, -86.52) * mm});
            skArc(sketch, "E7.1.4.13", {"start": v(-65, -86.78) * mm, "mid": v(-65.47, -83.77) * mm, "end": v(-66.55, -80.91) * mm});
            skArc(sketch, "E7.1.4.14", {"start": v(-108.4, -99.4) * mm, "mid": v(-106.32, -98.98) * mm, "end": v(-104.36, -98.17) * mm, "construction": true});
            skArc(sketch, "E7.1.4.15", {"start": v(-98.3, -88.01) * mm, "mid": v(-100.4, -88.63) * mm, "end": v(-102.35, -89.6) * mm, "construction": true});
            skArc(sketch, "E7.1.4.16", {"start": v(-74.53, -75.93) * mm, "mid": v(-76.56, -75.22) * mm, "end": v(-78.68, -74.87) * mm, "construction": true});
            skArc(sketch, "E7.1.4.17", {"start": v(-67.28, -84.96) * mm, "mid": v(-67.9, -82.87) * mm, "end": v(-68.87, -80.92) * mm, "construction": true});
            skArc(sketch, "E7.1.4.18", {"start": v(-96.49, -85.74) * mm, "mid": v(-99.5, -86.2) * mm, "end": v(-102.36, -87.28) * mm});
            skArc(sketch, "E7.1.4.19", {"start": v(-110.43, -101.48) * mm, "mid": v(-107.44, -101.33) * mm, "end": v(-104.56, -100.5) * mm});
            skArc(sketch, "E7.1.4.20", {"start": v(-71.45, -84.22) * mm, "mid": v(-69.4, -84.79) * mm, "end": v(-67.28, -84.96) * mm, "construction": true});
            skArc(sketch, "E7.1.4.21", {"start": v(-107.34, -95.27) * mm, "mid": v(-108.05, -97.3) * mm, "end": v(-108.4, -99.4) * mm, "construction": true});
            skArc(sketch, "E7.1.4.22", {"start": v(-99.05, -92.18) * mm, "mid": v(-98.48, -90.13) * mm, "end": v(-98.3, -88.01) * mm, "construction": true});
            skArc(sketch, "E7.1.4.23", {"start": v(-70.96, -86.52) * mm, "mid": v(-68, -86.98) * mm, "end": v(-65, -86.78) * mm});
            skArc(sketch, "E7.1.4.24", {"start": v(-109.65, -95.57) * mm, "mid": v(-110.34, -98.49) * mm, "end": v(-110.43, -101.48) * mm});
            skArc(sketch, "E7.1.4.25", {"start": v(-78.68, -74.87) * mm, "mid": v(-78.25, -76.95) * mm, "end": v(-77.44, -78.91) * mm, "construction": true});
            skArc(sketch, "E7.1.4.26", {"start": v(-66.64, -72.5) * mm, "mid": v(-70.81, -73.7) * mm, "end": v(-74.53, -75.93) * mm, "construction": true});
            skArc(sketch, "E7.1.4.27", {"start": v(-64.77, -70.3) * mm, "mid": v(-70.05, -71.23) * mm, "end": v(-74.84, -73.62) * mm});
            skArc(sketch, "E7.1.4.28", {"start": v(-68.87, -80.92) * mm, "mid": v(-67.17, -76.86) * mm, "end": v(-66.64, -72.5) * mm, "construction": true});
            skArc(sketch, "E7.1.4.29", {"start": v(-66.55, -80.91) * mm, "mid": v(-64.85, -75.74) * mm, "end": v(-64.77, -70.3) * mm});
            skArc(sketch, "E7.1.4.30", {"start": v(-80.75, -72.83) * mm, "mid": v(-80.6, -75.82) * mm, "end": v(-79.78, -78.7) * mm});
            skArc(sketch, "E7.1.4.31", {"start": v(-74.84, -73.62) * mm, "mid": v(-77.76, -72.92) * mm, "end": v(-80.75, -72.83) * mm});
            skArc(sketch, "E7.2.0.0", {"start": v(-31.22, 72.55) * mm, "mid": v(-32.34, 78.81) * mm, "end": v(-35.56, 84.3) * mm});
            skArc(sketch, "E7.2.0.1", {"start": v(-35.56, 84.3) * mm, "mid": v(-35.1, 87.25) * mm, "end": v(-35.3, 90.24) * mm});
            skArc(sketch, "E7.2.0.2", {"start": v(-41.16, 86.38) * mm, "mid": v(-45.21, 88.08) * mm, "end": v(-49.58, 88.61) * mm, "construction": true});
            skArc(sketch, "E7.2.0.3", {"start": v(-43.16, 77.81) * mm, "mid": v(-38.54, 75.36) * mm, "end": v(-33.37, 74.48) * mm, "construction": true});
            skArc(sketch, "E7.2.0.4", {"start": v(-51.78, 90.48) * mm, "mid": v(-50.85, 85.2) * mm, "end": v(-48.46, 80.41) * mm});
            skArc(sketch, "E7.2.0.5", {"start": v(-18.59, 97.28) * mm, "mid": v(-21.1, 91.46) * mm, "end": v(-21.5, 85.13) * mm});
            skArc(sketch, "E7.2.0.6", {"start": v(-16.25, 97.07) * mm, "mid": v(-18.7, 92.44) * mm, "end": v(-19.58, 87.28) * mm, "construction": true});
            skArc(sketch, "E7.2.0.7", {"start": v(-43.37, 75.47) * mm, "mid": v(-37.55, 72.96) * mm, "end": v(-31.22, 72.55) * mm});
            skArc(sketch, "E7.2.0.8", {"start": v(-41.16, 88.7) * mm, "mid": v(-46.34, 90.4) * mm, "end": v(-51.78, 90.48) * mm});
            skArc(sketch, "E7.2.0.9", {"start": v(-19.58, 87.28) * mm, "mid": v(-14.55, 88.75) * mm, "end": v(-10.26, 91.76) * mm, "construction": true});
            skArc(sketch, "E7.2.0.10", {"start": v(-49.58, 88.61) * mm, "mid": v(-48.39, 84.44) * mm, "end": v(-46.15, 80.72) * mm, "construction": true});
            skArc(sketch, "E7.2.0.11", {"start": v(-33.37, 74.48) * mm, "mid": v(-34.84, 79.51) * mm, "end": v(-37.85, 83.8) * mm, "construction": true});
            skArc(sketch, "E7.2.0.12", {"start": v(-21.5, 85.13) * mm, "mid": v(-15.25, 86.25) * mm, "end": v(-9.76, 89.46) * mm});
            skArc(sketch, "E7.2.0.13", {"start": v(-3.82, 89.2) * mm, "mid": v(-4.28, 92.22) * mm, "end": v(-5.36, 95.07) * mm});
            skArc(sketch, "E7.2.0.14", {"start": v(-47.2, 76.57) * mm, "mid": v(-45.13, 77) * mm, "end": v(-43.16, 77.81) * mm, "construction": true});
            skArc(sketch, "E7.2.0.15", {"start": v(-37.11, 87.97) * mm, "mid": v(-39.2, 87.35) * mm, "end": v(-41.16, 86.38) * mm, "construction": true});
            skArc(sketch, "E7.2.0.16", {"start": v(-13.34, 100.06) * mm, "mid": v(-15.37, 100.76) * mm, "end": v(-17.49, 101.11) * mm, "construction": true});
            skArc(sketch, "E7.2.0.17", {"start": v(-6.09, 91.02) * mm, "mid": v(-6.7, 93.11) * mm, "end": v(-7.68, 95.07) * mm, "construction": true});
            skArc(sketch, "E7.2.0.18", {"start": v(-35.3, 90.24) * mm, "mid": v(-38.31, 89.78) * mm, "end": v(-41.16, 88.7) * mm});
            skArc(sketch, "E7.2.0.19", {"start": v(-49.24, 74.5) * mm, "mid": v(-46.25, 74.65) * mm, "end": v(-43.37, 75.47) * mm});
            skArc(sketch, "E7.2.0.20", {"start": v(-10.26, 91.76) * mm, "mid": v(-8.2, 91.2) * mm, "end": v(-6.09, 91.02) * mm, "construction": true});
            skArc(sketch, "E7.2.0.21", {"start": v(-46.15, 80.72) * mm, "mid": v(-46.85, 78.7) * mm, "end": v(-47.2, 76.57) * mm, "construction": true});
            skArc(sketch, "E7.2.0.22", {"start": v(-37.85, 83.8) * mm, "mid": v(-37.29, 85.85) * mm, "end": v(-37.11, 87.97) * mm, "construction": true});
            skArc(sketch, "E7.2.0.23", {"start": v(-9.76, 89.46) * mm, "mid": v(-6.8, 89) * mm, "end": v(-3.82, 89.2) * mm});
            skArc(sketch, "E7.2.0.24", {"start": v(-48.46, 80.41) * mm, "mid": v(-49.15, 77.5) * mm, "end": v(-49.24, 74.5) * mm});
            skArc(sketch, "E7.2.0.25", {"start": v(-17.49, 101.11) * mm, "mid": v(-17.06, 99.03) * mm, "end": v(-16.25, 97.07) * mm, "construction": true});
            skArc(sketch, "E7.2.0.26", {"start": v(-5.45, 103.48) * mm, "mid": v(-9.62, 102.3) * mm, "end": v(-13.34, 100.06) * mm, "construction": true});
            skArc(sketch, "E7.2.0.27", {"start": v(-3.58, 105.68) * mm, "mid": v(-8.86, 104.76) * mm, "end": v(-13.65, 102.36) * mm});
            skArc(sketch, "E7.2.0.28", {"start": v(-7.68, 95.07) * mm, "mid": v(-5.98, 99.12) * mm, "end": v(-5.45, 103.48) * mm, "construction": true});
            skArc(sketch, "E7.2.0.29", {"start": v(-5.36, 95.07) * mm, "mid": v(-3.66, 100.24) * mm, "end": v(-3.58, 105.68) * mm});
            skArc(sketch, "E7.2.0.30", {"start": v(-19.56, 103.15) * mm, "mid": v(-19.4, 100.16) * mm, "end": v(-18.59, 97.28) * mm});
            skArc(sketch, "E7.2.0.31", {"start": v(-13.65, 102.36) * mm, "mid": v(-16.56, 103.06) * mm, "end": v(-19.56, 103.15) * mm});
            skArc(sketch, "E7.2.1.0", {"start": v(-31.42, 28.34) * mm, "mid": v(-32.54, 34.6) * mm, "end": v(-35.75, 40.08) * mm});
            skArc(sketch, "E7.2.1.1", {"start": v(-35.75, 40.08) * mm, "mid": v(-35.29, 43.04) * mm, "end": v(-35.5, 46.03) * mm});
            skArc(sketch, "E7.2.1.2", {"start": v(-41.35, 42.17) * mm, "mid": v(-45.4, 43.86) * mm, "end": v(-49.77, 44.4) * mm, "construction": true});
            skArc(sketch, "E7.2.1.3", {"start": v(-43.36, 33.6) * mm, "mid": v(-38.73, 31.15) * mm, "end": v(-33.57, 30.26) * mm, "construction": true});
            skArc(sketch, "E7.2.1.4", {"start": v(-51.97, 46.26) * mm, "mid": v(-51.04, 40.99) * mm, "end": v(-48.65, 36.2) * mm});
            skArc(sketch, "E7.2.1.5", {"start": v(-18.78, 53.06) * mm, "mid": v(-21.3, 47.24) * mm, "end": v(-21.7, 40.92) * mm});
            skArc(sketch, "E7.2.1.6", {"start": v(-16.44, 52.86) * mm, "mid": v(-18.9, 48.23) * mm, "end": v(-19.77, 43.06) * mm, "construction": true});
            skArc(sketch, "E7.2.1.7", {"start": v(-43.57, 31.26) * mm, "mid": v(-37.75, 28.75) * mm, "end": v(-31.42, 28.34) * mm});
            skArc(sketch, "E7.2.1.8", {"start": v(-41.36, 44.49) * mm, "mid": v(-46.53, 46.18) * mm, "end": v(-51.97, 46.26) * mm});
            skArc(sketch, "E7.2.1.9", {"start": v(-19.77, 43.06) * mm, "mid": v(-14.74, 44.53) * mm, "end": v(-10.46, 47.55) * mm, "construction": true});
            skArc(sketch, "E7.2.1.10", {"start": v(-49.77, 44.4) * mm, "mid": v(-48.58, 40.22) * mm, "end": v(-46.35, 36.5) * mm, "construction": true});
            skArc(sketch, "E7.2.1.11", {"start": v(-33.57, 30.26) * mm, "mid": v(-35.04, 35.3) * mm, "end": v(-38.05, 39.58) * mm, "construction": true});
            skArc(sketch, "E7.2.1.12", {"start": v(-21.7, 40.92) * mm, "mid": v(-15.44, 42.03) * mm, "end": v(-9.96, 45.25) * mm});
            skArc(sketch, "E7.2.1.13", {"start": v(-4.01, 44.99) * mm, "mid": v(-4.48, 48) * mm, "end": v(-5.55, 50.86) * mm});
            skArc(sketch, "E7.2.1.14", {"start": v(-47.4, 32.36) * mm, "mid": v(-45.32, 32.79) * mm, "end": v(-43.36, 33.6) * mm, "construction": true});
            skArc(sketch, "E7.2.1.15", {"start": v(-37.3, 43.76) * mm, "mid": v(-39.4, 43.14) * mm, "end": v(-41.35, 42.17) * mm, "construction": true});
            skArc(sketch, "E7.2.1.16", {"start": v(-13.54, 55.84) * mm, "mid": v(-15.56, 56.55) * mm, "end": v(-17.68, 56.9) * mm, "construction": true});
            skArc(sketch, "E7.2.1.17", {"start": v(-6.28, 46.8) * mm, "mid": v(-6.9, 48.9) * mm, "end": v(-7.87, 50.85) * mm, "construction": true});
            skArc(sketch, "E7.2.1.18", {"start": v(-35.5, 46.03) * mm, "mid": v(-38.5, 45.56) * mm, "end": v(-41.36, 44.49) * mm});
            skArc(sketch, "E7.2.1.19", {"start": v(-49.44, 30.28) * mm, "mid": v(-46.45, 30.44) * mm, "end": v(-43.57, 31.26) * mm});
            skArc(sketch, "E7.2.1.20", {"start": v(-10.46, 47.55) * mm, "mid": v(-8.4, 46.98) * mm, "end": v(-6.28, 46.8) * mm, "construction": true});
            skArc(sketch, "E7.2.1.21", {"start": v(-46.35, 36.5) * mm, "mid": v(-47.05, 34.47) * mm, "end": v(-47.4, 32.36) * mm, "construction": true});
            skArc(sketch, "E7.2.1.22", {"start": v(-38.05, 39.58) * mm, "mid": v(-37.48, 41.64) * mm, "end": v(-37.3, 43.76) * mm, "construction": true});
            skArc(sketch, "E7.2.1.23", {"start": v(-9.96, 45.25) * mm, "mid": v(-7, 44.78) * mm, "end": v(-4.01, 44.99) * mm});
            skArc(sketch, "E7.2.1.24", {"start": v(-48.65, 36.2) * mm, "mid": v(-49.35, 33.28) * mm, "end": v(-49.44, 30.28) * mm});
            skArc(sketch, "E7.2.1.25", {"start": v(-17.68, 56.9) * mm, "mid": v(-17.25, 54.82) * mm, "end": v(-16.44, 52.86) * mm, "construction": true});
            skArc(sketch, "E7.2.1.26", {"start": v(-5.64, 59.27) * mm, "mid": v(-9.82, 58.08) * mm, "end": v(-13.54, 55.84) * mm, "construction": true});
            skArc(sketch, "E7.2.1.27", {"start": v(-3.78, 61.47) * mm, "mid": v(-9.05, 60.54) * mm, "end": v(-13.84, 58.15) * mm});
            skArc(sketch, "E7.2.1.28", {"start": v(-7.87, 50.85) * mm, "mid": v(-6.18, 54.9) * mm, "end": v(-5.64, 59.27) * mm, "construction": true});
            skArc(sketch, "E7.2.1.29", {"start": v(-5.55, 50.86) * mm, "mid": v(-3.86, 56.03) * mm, "end": v(-3.78, 61.47) * mm});
            skArc(sketch, "E7.2.1.30", {"start": v(-19.76, 58.93) * mm, "mid": v(-19.6, 55.94) * mm, "end": v(-18.78, 53.06) * mm});
            skArc(sketch, "E7.2.1.31", {"start": v(-13.84, 58.15) * mm, "mid": v(-16.76, 58.84) * mm, "end": v(-19.76, 58.93) * mm});
            skArc(sketch, "E7.2.2.0", {"start": v(-31.62, -15.88) * mm, "mid": v(-32.73, -9.62) * mm, "end": v(-35.95, -4.13) * mm});
            skArc(sketch, "E7.2.2.1", {"start": v(-35.95, -4.13) * mm, "mid": v(-35.48, -1.18) * mm, "end": v(-35.69, 1.81) * mm});
            skArc(sketch, "E7.2.2.2", {"start": v(-41.55, -2.05) * mm, "mid": v(-45.6, -0.35) * mm, "end": v(-49.97, 0.18) * mm, "construction": true});
            skArc(sketch, "E7.2.2.3", {"start": v(-43.55, -10.62) * mm, "mid": v(-38.93, -13.07) * mm, "end": v(-33.76, -13.95) * mm, "construction": true});
            skArc(sketch, "E7.2.2.4", {"start": v(-52.17, 2.05) * mm, "mid": v(-51.24, -3.23) * mm, "end": v(-48.85, -8.02) * mm});
            skArc(sketch, "E7.2.2.5", {"start": v(-18.98, 8.85) * mm, "mid": v(-21.49, 3.03) * mm, "end": v(-21.9, -3.3) * mm});
            skArc(sketch, "E7.2.2.6", {"start": v(-16.64, 8.64) * mm, "mid": v(-19.09, 4.01) * mm, "end": v(-19.97, -1.15) * mm, "construction": true});
            skArc(sketch, "E7.2.2.7", {"start": v(-43.76, -12.96) * mm, "mid": v(-37.94, -15.47) * mm, "end": v(-31.62, -15.88) * mm});
            skArc(sketch, "E7.2.2.8", {"start": v(-41.55, 0.27) * mm, "mid": v(-46.73, 1.97) * mm, "end": v(-52.17, 2.05) * mm});
            skArc(sketch, "E7.2.2.9", {"start": v(-19.97, -1.15) * mm, "mid": v(-14.94, 0.32) * mm, "end": v(-10.65, 3.33) * mm, "construction": true});
            skArc(sketch, "E7.2.2.10", {"start": v(-49.97, 0.18) * mm, "mid": v(-48.78, -4) * mm, "end": v(-46.54, -7.71) * mm, "construction": true});
            skArc(sketch, "E7.2.2.11", {"start": v(-33.76, -13.95) * mm, "mid": v(-35.23, -8.92) * mm, "end": v(-38.25, -4.63) * mm, "construction": true});
            skArc(sketch, "E7.2.2.12", {"start": v(-21.9, -3.3) * mm, "mid": v(-15.64, -2.18) * mm, "end": v(-10.15, 1.03) * mm});
            skArc(sketch, "E7.2.2.13", {"start": v(-4.2, 0.77) * mm, "mid": v(-4.67, 3.79) * mm, "end": v(-5.75, 6.64) * mm});
            skArc(sketch, "E7.2.2.14", {"start": v(-47.6, -11.86) * mm, "mid": v(-45.52, -11.43) * mm, "end": v(-43.55, -10.62) * mm, "construction": true});
            skArc(sketch, "E7.2.2.15", {"start": v(-37.5, -0.46) * mm, "mid": v(-39.6, -1.08) * mm, "end": v(-41.55, -2.05) * mm, "construction": true});
            skArc(sketch, "E7.2.2.16", {"start": v(-13.73, 11.63) * mm, "mid": v(-15.76, 12.33) * mm, "end": v(-17.88, 12.68) * mm, "construction": true});
            skArc(sketch, "E7.2.2.17", {"start": v(-6.48, 2.59) * mm, "mid": v(-7.1, 4.68) * mm, "end": v(-8.07, 6.63) * mm, "construction": true});
            skArc(sketch, "E7.2.2.18", {"start": v(-35.69, 1.81) * mm, "mid": v(-38.7, 1.35) * mm, "end": v(-41.55, 0.27) * mm});
            skArc(sketch, "E7.2.2.19", {"start": v(-49.63, -13.93) * mm, "mid": v(-46.64, -13.78) * mm, "end": v(-43.76, -12.96) * mm});
            skArc(sketch, "E7.2.2.20", {"start": v(-10.65, 3.33) * mm, "mid": v(-8.6, 2.76) * mm, "end": v(-6.48, 2.59) * mm, "construction": true});
            skArc(sketch, "E7.2.2.21", {"start": v(-46.54, -7.71) * mm, "mid": v(-47.25, -9.74) * mm, "end": v(-47.6, -11.86) * mm, "construction": true});
            skArc(sketch, "E7.2.2.22", {"start": v(-38.25, -4.63) * mm, "mid": v(-37.68, -2.58) * mm, "end": v(-37.5, -0.46) * mm, "construction": true});
            skArc(sketch, "E7.2.2.23", {"start": v(-10.15, 1.03) * mm, "mid": v(-7.2, 0.57) * mm, "end": v(-4.2, 0.77) * mm});
            skArc(sketch, "E7.2.2.24", {"start": v(-48.85, -8.02) * mm, "mid": v(-49.54, -10.94) * mm, "end": v(-49.63, -13.93) * mm});
            skArc(sketch, "E7.2.2.25", {"start": v(-17.88, 12.68) * mm, "mid": v(-17.45, 10.6) * mm, "end": v(-16.64, 8.64) * mm, "construction": true});
            skArc(sketch, "E7.2.2.26", {"start": v(-5.84, 15.05) * mm, "mid": v(-10.01, 13.86) * mm, "end": v(-13.73, 11.63) * mm, "construction": true});
            skArc(sketch, "E7.2.2.27", {"start": v(-3.97, 17.25) * mm, "mid": v(-9.25, 16.33) * mm, "end": v(-14.04, 13.93) * mm});
            skArc(sketch, "E7.2.2.28", {"start": v(-8.07, 6.63) * mm, "mid": v(-6.37, 10.69) * mm, "end": v(-5.84, 15.05) * mm, "construction": true});
            skArc(sketch, "E7.2.2.29", {"start": v(-5.75, 6.64) * mm, "mid": v(-4.05, 11.81) * mm, "end": v(-3.97, 17.25) * mm});
            skArc(sketch, "E7.2.2.30", {"start": v(-19.95, 14.72) * mm, "mid": v(-19.8, 11.73) * mm, "end": v(-18.98, 8.85) * mm});
            skArc(sketch, "E7.2.2.31", {"start": v(-14.04, 13.93) * mm, "mid": v(-16.96, 14.63) * mm, "end": v(-19.95, 14.72) * mm});
            skArc(sketch, "E7.2.3.0", {"start": v(-31.81, -60.1) * mm, "mid": v(-32.93, -53.83) * mm, "end": v(-36.14, -48.35) * mm});
            skArc(sketch, "E7.2.3.1", {"start": v(-36.14, -48.35) * mm, "mid": v(-35.68, -45.4) * mm, "end": v(-35.88, -42.4) * mm});
            skArc(sketch, "E7.2.3.2", {"start": v(-41.74, -46.26) * mm, "mid": v(-45.8, -44.57) * mm, "end": v(-50.16, -44.04) * mm, "construction": true});
            skArc(sketch, "E7.2.3.3", {"start": v(-43.75, -54.84) * mm, "mid": v(-39.12, -57.29) * mm, "end": v(-33.96, -58.17) * mm, "construction": true});
            skArc(sketch, "E7.2.3.4", {"start": v(-52.36, -42.17) * mm, "mid": v(-51.44, -47.44) * mm, "end": v(-49.04, -52.23) * mm});
            skArc(sketch, "E7.2.3.5", {"start": v(-19.17, -35.37) * mm, "mid": v(-21.68, -41.19) * mm, "end": v(-22.1, -47.51) * mm});
            skArc(sketch, "E7.2.3.6", {"start": v(-16.84, -35.58) * mm, "mid": v(-19.29, -40.2) * mm, "end": v(-20.17, -45.37) * mm, "construction": true});
            skArc(sketch, "E7.2.3.7", {"start": v(-43.96, -57.17) * mm, "mid": v(-38.14, -59.68) * mm, "end": v(-31.81, -60.1) * mm});
            skArc(sketch, "E7.2.3.8", {"start": v(-41.75, -43.94) * mm, "mid": v(-46.92, -42.25) * mm, "end": v(-52.36, -42.17) * mm});
            skArc(sketch, "E7.2.3.9", {"start": v(-20.17, -45.37) * mm, "mid": v(-15.14, -43.9) * mm, "end": v(-10.85, -40.88) * mm, "construction": true});
            skArc(sketch, "E7.2.3.10", {"start": v(-50.16, -44.04) * mm, "mid": v(-48.97, -48.2) * mm, "end": v(-46.74, -51.93) * mm, "construction": true});
            skArc(sketch, "E7.2.3.11", {"start": v(-33.96, -58.17) * mm, "mid": v(-35.43, -53.14) * mm, "end": v(-38.44, -48.85) * mm, "construction": true});
            skArc(sketch, "E7.2.3.12", {"start": v(-22.1, -47.51) * mm, "mid": v(-15.83, -46.4) * mm, "end": v(-10.35, -43.18) * mm});
            skArc(sketch, "E7.2.3.13", {"start": v(-4.4, -43.44) * mm, "mid": v(-4.87, -40.43) * mm, "end": v(-5.94, -37.58) * mm});
            skArc(sketch, "E7.2.3.14", {"start": v(-47.8, -56.07) * mm, "mid": v(-45.71, -55.64) * mm, "end": v(-43.75, -54.84) * mm, "construction": true});
            skArc(sketch, "E7.2.3.15", {"start": v(-37.7, -44.67) * mm, "mid": v(-39.79, -45.3) * mm, "end": v(-41.74, -46.26) * mm, "construction": true});
            skArc(sketch, "E7.2.3.16", {"start": v(-13.93, -32.59) * mm, "mid": v(-15.96, -31.88) * mm, "end": v(-18.07, -31.53) * mm, "construction": true});
            skArc(sketch, "E7.2.3.17", {"start": v(-6.67, -41.63) * mm, "mid": v(-7.3, -39.54) * mm, "end": v(-8.26, -37.58) * mm, "construction": true});
            skArc(sketch, "E7.2.3.18", {"start": v(-35.88, -42.4) * mm, "mid": v(-38.9, -42.87) * mm, "end": v(-41.75, -43.94) * mm});
            skArc(sketch, "E7.2.3.19", {"start": v(-49.83, -58.15) * mm, "mid": v(-46.84, -58) * mm, "end": v(-43.96, -57.17) * mm});
            skArc(sketch, "E7.2.3.20", {"start": v(-10.85, -40.88) * mm, "mid": v(-8.8, -41.45) * mm, "end": v(-6.67, -41.63) * mm, "construction": true});
            skArc(sketch, "E7.2.3.21", {"start": v(-46.74, -51.93) * mm, "mid": v(-47.44, -53.96) * mm, "end": v(-47.8, -56.07) * mm, "construction": true});
            skArc(sketch, "E7.2.3.22", {"start": v(-38.44, -48.85) * mm, "mid": v(-37.87, -46.8) * mm, "end": v(-37.7, -44.67) * mm, "construction": true});
            skArc(sketch, "E7.2.3.23", {"start": v(-10.35, -43.18) * mm, "mid": v(-7.4, -43.65) * mm, "end": v(-4.4, -43.44) * mm});
            skArc(sketch, "E7.2.3.24", {"start": v(-49.04, -52.23) * mm, "mid": v(-49.74, -55.15) * mm, "end": v(-49.83, -58.15) * mm});
            skArc(sketch, "E7.2.3.25", {"start": v(-18.07, -31.53) * mm, "mid": v(-17.64, -33.61) * mm, "end": v(-16.84, -35.58) * mm, "construction": true});
            skArc(sketch, "E7.2.3.26", {"start": v(-6.04, -29.16) * mm, "mid": v(-10.2, -30.35) * mm, "end": v(-13.93, -32.59) * mm, "construction": true});
            skArc(sketch, "E7.2.3.27", {"start": v(-4.17, -26.96) * mm, "mid": v(-9.44, -27.89) * mm, "end": v(-14.23, -30.28) * mm});
            skArc(sketch, "E7.2.3.28", {"start": v(-8.26, -37.58) * mm, "mid": v(-6.57, -33.53) * mm, "end": v(-6.04, -29.16) * mm, "construction": true});
            skArc(sketch, "E7.2.3.29", {"start": v(-5.94, -37.58) * mm, "mid": v(-4.25, -32.4) * mm, "end": v(-4.17, -26.96) * mm});
            skArc(sketch, "E7.2.3.30", {"start": v(-20.15, -29.5) * mm, "mid": v(-20, -32.49) * mm, "end": v(-19.17, -35.37) * mm});
            skArc(sketch, "E7.2.3.31", {"start": v(-14.23, -30.28) * mm, "mid": v(-17.15, -29.59) * mm, "end": v(-20.15, -29.5) * mm});
            skArc(sketch, "E7.2.4.0", {"start": v(-32, -104.3) * mm, "mid": v(-33.12, -98.05) * mm, "end": v(-36.34, -92.57) * mm});
            skArc(sketch, "E7.2.4.1", {"start": v(-36.34, -92.57) * mm, "mid": v(-35.87, -89.6) * mm, "end": v(-36.08, -86.62) * mm});
            skArc(sketch, "E7.2.4.2", {"start": v(-41.94, -90.48) * mm, "mid": v(-46, -88.78) * mm, "end": v(-50.36, -88.25) * mm, "construction": true});
            skArc(sketch, "E7.2.4.3", {"start": v(-43.95, -99.05) * mm, "mid": v(-39.32, -101.5) * mm, "end": v(-34.15, -102.38) * mm, "construction": true});
            skArc(sketch, "E7.2.4.4", {"start": v(-52.56, -86.38) * mm, "mid": v(-51.63, -91.66) * mm, "end": v(-49.24, -96.45) * mm});
            skArc(sketch, "E7.2.4.5", {"start": v(-19.37, -79.58) * mm, "mid": v(-21.88, -85.4) * mm, "end": v(-22.29, -91.73) * mm});
            skArc(sketch, "E7.2.4.6", {"start": v(-17.03, -79.8) * mm, "mid": v(-19.48, -84.42) * mm, "end": v(-20.36, -89.58) * mm, "construction": true});
            skArc(sketch, "E7.2.4.7", {"start": v(-44.15, -101.39) * mm, "mid": v(-38.33, -103.9) * mm, "end": v(-32, -104.3) * mm});
            skArc(sketch, "E7.2.4.8", {"start": v(-41.95, -88.16) * mm, "mid": v(-47.12, -86.46) * mm, "end": v(-52.56, -86.38) * mm});
            skArc(sketch, "E7.2.4.9", {"start": v(-20.36, -89.58) * mm, "mid": v(-15.33, -88.11) * mm, "end": v(-11.04, -85.1) * mm, "construction": true});
            skArc(sketch, "E7.2.4.10", {"start": v(-50.36, -88.25) * mm, "mid": v(-49.17, -92.42) * mm, "end": v(-46.93, -96.14) * mm, "construction": true});
            skArc(sketch, "E7.2.4.11", {"start": v(-34.15, -102.38) * mm, "mid": v(-35.63, -97.35) * mm, "end": v(-38.64, -93.06) * mm, "construction": true});
            skArc(sketch, "E7.2.4.12", {"start": v(-22.29, -91.73) * mm, "mid": v(-16.03, -90.61) * mm, "end": v(-10.55, -87.4) * mm});
            skArc(sketch, "E7.2.4.13", {"start": v(-4.6, -87.66) * mm, "mid": v(-5.06, -84.64) * mm, "end": v(-6.14, -81.8) * mm});
            skArc(sketch, "E7.2.4.14", {"start": v(-47.99, -100.29) * mm, "mid": v(-45.9, -99.86) * mm, "end": v(-43.95, -99.05) * mm, "construction": true});
            skArc(sketch, "E7.2.4.15", {"start": v(-37.9, -88.89) * mm, "mid": v(-39.99, -89.5) * mm, "end": v(-41.94, -90.48) * mm, "construction": true});
            skArc(sketch, "E7.2.4.16", {"start": v(-14.12, -76.8) * mm, "mid": v(-16.15, -76.1) * mm, "end": v(-18.27, -75.75) * mm, "construction": true});
            skArc(sketch, "E7.2.4.17", {"start": v(-6.87, -85.84) * mm, "mid": v(-7.49, -83.75) * mm, "end": v(-8.46, -81.8) * mm, "construction": true});
            skArc(sketch, "E7.2.4.18", {"start": v(-36.08, -86.62) * mm, "mid": v(-39.1, -87.08) * mm, "end": v(-41.95, -88.16) * mm});
            skArc(sketch, "E7.2.4.19", {"start": v(-50.02, -102.36) * mm, "mid": v(-47.03, -102.2) * mm, "end": v(-44.15, -101.39) * mm});
            skArc(sketch, "E7.2.4.20", {"start": v(-11.04, -85.1) * mm, "mid": v(-9, -85.67) * mm, "end": v(-6.87, -85.84) * mm, "construction": true});
            skArc(sketch, "E7.2.4.21", {"start": v(-46.93, -96.14) * mm, "mid": v(-47.64, -98.17) * mm, "end": v(-47.99, -100.29) * mm, "construction": true});
            skArc(sketch, "E7.2.4.22", {"start": v(-38.64, -93.06) * mm, "mid": v(-38.07, -91.01) * mm, "end": v(-37.9, -88.89) * mm, "construction": true});
            skArc(sketch, "E7.2.4.23", {"start": v(-10.55, -87.4) * mm, "mid": v(-7.59, -87.86) * mm, "end": v(-4.6, -87.66) * mm});
            skArc(sketch, "E7.2.4.24", {"start": v(-49.24, -96.45) * mm, "mid": v(-49.93, -99.37) * mm, "end": v(-50.02, -102.36) * mm});
            skArc(sketch, "E7.2.4.25", {"start": v(-18.27, -75.75) * mm, "mid": v(-17.84, -77.83) * mm, "end": v(-17.03, -79.8) * mm, "construction": true});
            skArc(sketch, "E7.2.4.26", {"start": v(-6.23, -73.38) * mm, "mid": v(-10.4, -74.57) * mm, "end": v(-14.12, -76.8) * mm, "construction": true});
            skArc(sketch, "E7.2.4.27", {"start": v(-4.36, -71.18) * mm, "mid": v(-9.64, -72.1) * mm, "end": v(-14.43, -74.5) * mm});
            skArc(sketch, "E7.2.4.28", {"start": v(-8.46, -81.8) * mm, "mid": v(-6.76, -77.74) * mm, "end": v(-6.23, -73.38) * mm, "construction": true});
            skArc(sketch, "E7.2.4.29", {"start": v(-6.14, -81.8) * mm, "mid": v(-4.44, -76.62) * mm, "end": v(-4.36, -71.18) * mm});
            skArc(sketch, "E7.2.4.30", {"start": v(-20.34, -73.71) * mm, "mid": v(-20.19, -76.7) * mm, "end": v(-19.37, -79.58) * mm});
            skArc(sketch, "E7.2.4.31", {"start": v(-14.43, -74.5) * mm, "mid": v(-17.35, -73.8) * mm, "end": v(-20.34, -73.71) * mm});
            skArc(sketch, "E7.3.0.0", {"start": v(29.19, 71.67) * mm, "mid": v(28.07, 77.93) * mm, "end": v(24.85, 83.42) * mm});
            skArc(sketch, "E7.3.0.1", {"start": v(24.85, 83.42) * mm, "mid": v(25.32, 86.38) * mm, "end": v(25.11, 89.36) * mm});
            skArc(sketch, "E7.3.0.2", {"start": v(19.25, 85.5) * mm, "mid": v(15.2, 87.2) * mm, "end": v(10.83, 87.73) * mm, "construction": true});
            skArc(sketch, "E7.3.0.3", {"start": v(17.25, 76.93) * mm, "mid": v(21.87, 74.48) * mm, "end": v(27.04, 73.6) * mm, "construction": true});
            skArc(sketch, "E7.3.0.4", {"start": v(8.63, 89.6) * mm, "mid": v(9.56, 84.32) * mm, "end": v(11.95, 79.53) * mm});
            skArc(sketch, "E7.3.0.5", {"start": v(41.82, 96.4) * mm, "mid": v(39.31, 90.58) * mm, "end": v(38.9, 84.25) * mm});
            skArc(sketch, "E7.3.0.6", {"start": v(44.16, 96.2) * mm, "mid": v(41.71, 91.56) * mm, "end": v(40.83, 86.4) * mm, "construction": true});
            skArc(sketch, "E7.3.0.7", {"start": v(17.04, 74.6) * mm, "mid": v(22.86, 72.08) * mm, "end": v(29.19, 71.67) * mm});
            skArc(sketch, "E7.3.0.8", {"start": v(19.25, 87.82) * mm, "mid": v(14.07, 89.52) * mm, "end": v(8.63, 89.6) * mm});
            skArc(sketch, "E7.3.0.9", {"start": v(40.83, 86.4) * mm, "mid": v(45.86, 87.87) * mm, "end": v(50.15, 90.88) * mm, "construction": true});
            skArc(sketch, "E7.3.0.10", {"start": v(10.83, 87.73) * mm, "mid": v(12.02, 83.56) * mm, "end": v(14.26, 79.84) * mm, "construction": true});
            skArc(sketch, "E7.3.0.11", {"start": v(27.04, 73.6) * mm, "mid": v(25.57, 78.63) * mm, "end": v(22.56, 82.92) * mm, "construction": true});
            skArc(sketch, "E7.3.0.12", {"start": v(38.9, 84.25) * mm, "mid": v(45.16, 85.37) * mm, "end": v(50.65, 88.58) * mm});
            skArc(sketch, "E7.3.0.13", {"start": v(56.6, 88.32) * mm, "mid": v(56.13, 91.34) * mm, "end": v(55.05, 94.2) * mm});
            skArc(sketch, "E7.3.0.14", {"start": v(13.2, 75.7) * mm, "mid": v(15.28, 76.12) * mm, "end": v(17.25, 76.93) * mm, "construction": true});
            skArc(sketch, "E7.3.0.15", {"start": v(23.3, 87.1) * mm, "mid": v(21.2, 86.47) * mm, "end": v(19.25, 85.5) * mm, "construction": true});
            skArc(sketch, "E7.3.0.16", {"start": v(47.07, 99.18) * mm, "mid": v(45.04, 99.88) * mm, "end": v(42.92, 100.24) * mm, "construction": true});
            skArc(sketch, "E7.3.0.17", {"start": v(54.32, 90.14) * mm, "mid": v(53.7, 92.23) * mm, "end": v(52.73, 94.19) * mm, "construction": true});
            skArc(sketch, "E7.3.0.18", {"start": v(25.11, 89.36) * mm, "mid": v(22.1, 88.9) * mm, "end": v(19.25, 87.82) * mm});
            skArc(sketch, "E7.3.0.19", {"start": v(11.17, 73.62) * mm, "mid": v(14.16, 73.78) * mm, "end": v(17.04, 74.6) * mm});
            skArc(sketch, "E7.3.0.20", {"start": v(50.15, 90.88) * mm, "mid": v(52.2, 90.31) * mm, "end": v(54.32, 90.14) * mm, "construction": true});
            skArc(sketch, "E7.3.0.21", {"start": v(14.26, 79.84) * mm, "mid": v(13.56, 77.81) * mm, "end": v(13.2, 75.7) * mm, "construction": true});
            skArc(sketch, "E7.3.0.22", {"start": v(22.56, 82.92) * mm, "mid": v(23.12, 84.97) * mm, "end": v(23.3, 87.1) * mm, "construction": true});
            skArc(sketch, "E7.3.0.23", {"start": v(50.65, 88.58) * mm, "mid": v(53.6, 88.12) * mm, "end": v(56.6, 88.32) * mm});
            skArc(sketch, "E7.3.0.24", {"start": v(11.95, 79.53) * mm, "mid": v(11.26, 76.62) * mm, "end": v(11.17, 73.62) * mm});
            skArc(sketch, "E7.3.0.25", {"start": v(42.92, 100.24) * mm, "mid": v(43.35, 98.16) * mm, "end": v(44.16, 96.2) * mm, "construction": true});
            skArc(sketch, "E7.3.0.26", {"start": v(54.96, 102.6) * mm, "mid": v(50.79, 101.41) * mm, "end": v(47.07, 99.18) * mm, "construction": true});
            skArc(sketch, "E7.3.0.27", {"start": v(56.83, 104.8) * mm, "mid": v(51.55, 103.88) * mm, "end": v(46.76, 101.48) * mm});
            skArc(sketch, "E7.3.0.28", {"start": v(52.73, 94.19) * mm, "mid": v(54.43, 98.24) * mm, "end": v(54.96, 102.6) * mm, "construction": true});
            skArc(sketch, "E7.3.0.29", {"start": v(55.05, 94.2) * mm, "mid": v(56.75, 99.36) * mm, "end": v(56.83, 104.8) * mm});
            skArc(sketch, "E7.3.0.30", {"start": v(40.85, 102.27) * mm, "mid": v(41, 99.28) * mm, "end": v(41.82, 96.4) * mm});
            skArc(sketch, "E7.3.0.31", {"start": v(46.76, 101.48) * mm, "mid": v(43.85, 102.18) * mm, "end": v(40.85, 102.27) * mm});
            skArc(sketch, "E7.3.1.0", {"start": v(29, 27.46) * mm, "mid": v(27.87, 33.72) * mm, "end": v(24.66, 39.2) * mm});
            skArc(sketch, "E7.3.1.1", {"start": v(24.66, 39.2) * mm, "mid": v(25.12, 42.16) * mm, "end": v(24.92, 45.15) * mm});
            skArc(sketch, "E7.3.1.2", {"start": v(19.06, 41.3) * mm, "mid": v(15, 42.98) * mm, "end": v(10.64, 43.52) * mm, "construction": true});
            skArc(sketch, "E7.3.1.3", {"start": v(17.05, 32.72) * mm, "mid": v(21.68, 30.27) * mm, "end": v(26.84, 29.39) * mm, "construction": true});
            skArc(sketch, "E7.3.1.4", {"start": v(8.44, 45.38) * mm, "mid": v(9.37, 40.1) * mm, "end": v(11.76, 35.32) * mm});
            skArc(sketch, "E7.3.1.5", {"start": v(41.63, 52.18) * mm, "mid": v(39.12, 46.36) * mm, "end": v(38.7, 40.04) * mm});
            skArc(sketch, "E7.3.1.6", {"start": v(43.97, 51.98) * mm, "mid": v(41.52, 47.35) * mm, "end": v(40.64, 42.19) * mm, "construction": true});
            skArc(sketch, "E7.3.1.7", {"start": v(16.84, 30.38) * mm, "mid": v(22.66, 27.87) * mm, "end": v(29, 27.46) * mm});
            skArc(sketch, "E7.3.1.8", {"start": v(19.05, 43.6) * mm, "mid": v(13.88, 45.3) * mm, "end": v(8.44, 45.38) * mm});
            skArc(sketch, "E7.3.1.9", {"start": v(40.64, 42.19) * mm, "mid": v(45.67, 43.66) * mm, "end": v(49.95, 46.67) * mm, "construction": true});
            skArc(sketch, "E7.3.1.10", {"start": v(10.64, 43.52) * mm, "mid": v(11.83, 39.34) * mm, "end": v(14.06, 35.62) * mm, "construction": true});
            skArc(sketch, "E7.3.1.11", {"start": v(26.84, 29.39) * mm, "mid": v(25.37, 34.42) * mm, "end": v(22.36, 38.7) * mm, "construction": true});
            skArc(sketch, "E7.3.1.12", {"start": v(38.7, 40.04) * mm, "mid": v(44.97, 41.16) * mm, "end": v(50.45, 44.37) * mm});
            skArc(sketch, "E7.3.1.13", {"start": v(56.4, 44.1) * mm, "mid": v(55.93, 47.12) * mm, "end": v(54.86, 49.98) * mm});
            skArc(sketch, "E7.3.1.14", {"start": v(13, 31.48) * mm, "mid": v(15.09, 31.9) * mm, "end": v(17.05, 32.72) * mm, "construction": true});
            skArc(sketch, "E7.3.1.15", {"start": v(23.1, 42.88) * mm, "mid": v(21.01, 42.26) * mm, "end": v(19.06, 41.3) * mm, "construction": true});
            skArc(sketch, "E7.3.1.16", {"start": v(46.87, 54.96) * mm, "mid": v(44.85, 55.67) * mm, "end": v(42.73, 56.02) * mm, "construction": true});
            skArc(sketch, "E7.3.1.17", {"start": v(54.13, 45.92) * mm, "mid": v(53.5, 48.02) * mm, "end": v(52.54, 49.97) * mm, "construction": true});
            skArc(sketch, "E7.3.1.18", {"start": v(24.92, 45.15) * mm, "mid": v(21.9, 44.68) * mm, "end": v(19.05, 43.6) * mm});
            skArc(sketch, "E7.3.1.19", {"start": v(10.97, 29.4) * mm, "mid": v(13.96, 29.56) * mm, "end": v(16.84, 30.38) * mm});
            skArc(sketch, "E7.3.1.20", {"start": v(49.95, 46.67) * mm, "mid": v(52, 46.1) * mm, "end": v(54.13, 45.92) * mm, "construction": true});
            skArc(sketch, "E7.3.1.21", {"start": v(14.06, 35.62) * mm, "mid": v(13.36, 33.6) * mm, "end": v(13, 31.48) * mm, "construction": true});
            skArc(sketch, "E7.3.1.22", {"start": v(22.36, 38.7) * mm, "mid": v(22.93, 40.76) * mm, "end": v(23.1, 42.88) * mm, "construction": true});
            skArc(sketch, "E7.3.1.23", {"start": v(50.45, 44.37) * mm, "mid": v(53.4, 43.9) * mm, "end": v(56.4, 44.1) * mm});
            skArc(sketch, "E7.3.1.24", {"start": v(11.76, 35.32) * mm, "mid": v(11.06, 32.4) * mm, "end": v(10.97, 29.4) * mm});
            skArc(sketch, "E7.3.1.25", {"start": v(42.73, 56.02) * mm, "mid": v(43.16, 53.94) * mm, "end": v(43.97, 51.98) * mm, "construction": true});
            skArc(sketch, "E7.3.1.26", {"start": v(54.77, 58.39) * mm, "mid": v(50.6, 57.2) * mm, "end": v(46.87, 54.96) * mm, "construction": true});
            skArc(sketch, "E7.3.1.27", {"start": v(56.63, 60.6) * mm, "mid": v(51.36, 59.66) * mm, "end": v(46.57, 57.27) * mm});
            skArc(sketch, "E7.3.1.28", {"start": v(52.54, 49.97) * mm, "mid": v(54.23, 54.03) * mm, "end": v(54.77, 58.39) * mm, "construction": true});
            skArc(sketch, "E7.3.1.29", {"start": v(54.86, 49.98) * mm, "mid": v(56.55, 55.15) * mm, "end": v(56.63, 60.6) * mm});
            skArc(sketch, "E7.3.1.30", {"start": v(40.65, 58.06) * mm, "mid": v(40.8, 55.06) * mm, "end": v(41.63, 52.18) * mm});
            skArc(sketch, "E7.3.1.31", {"start": v(46.57, 57.27) * mm, "mid": v(43.65, 57.96) * mm, "end": v(40.65, 58.06) * mm});
            skArc(sketch, "E7.3.2.0", {"start": v(28.8, -16.76) * mm, "mid": v(27.68, -10.5) * mm, "end": v(24.46, -5.01) * mm});
            skArc(sketch, "E7.3.2.1", {"start": v(24.46, -5.01) * mm, "mid": v(24.93, -2.05) * mm, "end": v(24.72, 0.93) * mm});
            skArc(sketch, "E7.3.2.2", {"start": v(18.86, -2.93) * mm, "mid": v(14.8, -1.23) * mm, "end": v(10.44, -0.7) * mm, "construction": true});
            skArc(sketch, "E7.3.2.3", {"start": v(16.86, -11.5) * mm, "mid": v(21.48, -13.95) * mm, "end": v(26.65, -14.83) * mm, "construction": true});
            skArc(sketch, "E7.3.2.4", {"start": v(8.24, 1.17) * mm, "mid": v(9.17, -4.1) * mm, "end": v(11.56, -8.9) * mm});
            skArc(sketch, "E7.3.2.5", {"start": v(41.43, 7.97) * mm, "mid": v(38.92, 2.15) * mm, "end": v(38.51, -4.18) * mm});
            skArc(sketch, "E7.3.2.6", {"start": v(43.77, 7.76) * mm, "mid": v(41.32, 3.13) * mm, "end": v(40.44, -2.03) * mm, "construction": true});
            skArc(sketch, "E7.3.2.7", {"start": v(16.65, -13.84) * mm, "mid": v(22.47, -16.35) * mm, "end": v(28.8, -16.76) * mm});
            skArc(sketch, "E7.3.2.8", {"start": v(18.86, -0.6) * mm, "mid": v(13.68, 1.09) * mm, "end": v(8.24, 1.17) * mm});
            skArc(sketch, "E7.3.2.9", {"start": v(40.44, -2.03) * mm, "mid": v(45.47, -0.56) * mm, "end": v(49.76, 2.45) * mm, "construction": true});
            skArc(sketch, "E7.3.2.10", {"start": v(10.44, -0.7) * mm, "mid": v(11.63, -4.87) * mm, "end": v(13.87, -8.6) * mm, "construction": true});
            skArc(sketch, "E7.3.2.11", {"start": v(26.65, -14.83) * mm, "mid": v(25.18, -9.8) * mm, "end": v(22.16, -5.51) * mm, "construction": true});
            skArc(sketch, "E7.3.2.12", {"start": v(38.51, -4.18) * mm, "mid": v(44.77, -3.06) * mm, "end": v(50.26, 0.15) * mm});
            skArc(sketch, "E7.3.2.13", {"start": v(56.2, -0.1) * mm, "mid": v(55.74, 2.9) * mm, "end": v(54.66, 5.76) * mm});
            skArc(sketch, "E7.3.2.14", {"start": v(12.81, -12.74) * mm, "mid": v(14.9, -12.3) * mm, "end": v(16.86, -11.5) * mm, "construction": true});
            skArc(sketch, "E7.3.2.15", {"start": v(22.9, -1.34) * mm, "mid": v(20.82, -1.96) * mm, "end": v(18.86, -2.93) * mm, "construction": true});
            skArc(sketch, "E7.3.2.16", {"start": v(46.68, 10.75) * mm, "mid": v(44.65, 11.45) * mm, "end": v(42.53, 11.8) * mm, "construction": true});
            skArc(sketch, "E7.3.2.17", {"start": v(53.93, 1.7) * mm, "mid": v(53.31, 3.8) * mm, "end": v(52.34, 5.76) * mm, "construction": true});
            skArc(sketch, "E7.3.2.18", {"start": v(24.72, 0.93) * mm, "mid": v(21.7, 0.47) * mm, "end": v(18.86, -0.6) * mm});
            skArc(sketch, "E7.3.2.19", {"start": v(10.78, -14.81) * mm, "mid": v(13.77, -14.65) * mm, "end": v(16.65, -13.84) * mm});
            skArc(sketch, "E7.3.2.20", {"start": v(49.76, 2.45) * mm, "mid": v(51.81, 1.88) * mm, "end": v(53.93, 1.7) * mm, "construction": true});
            skArc(sketch, "E7.3.2.21", {"start": v(13.87, -8.6) * mm, "mid": v(13.16, -10.62) * mm, "end": v(12.81, -12.74) * mm, "construction": true});
            skArc(sketch, "E7.3.2.22", {"start": v(22.16, -5.51) * mm, "mid": v(22.73, -3.46) * mm, "end": v(22.9, -1.34) * mm, "construction": true});
            skArc(sketch, "E7.3.2.23", {"start": v(50.26, 0.15) * mm, "mid": v(53.21, -0.31) * mm, "end": v(56.2, -0.1) * mm});
            skArc(sketch, "E7.3.2.24", {"start": v(11.56, -8.9) * mm, "mid": v(10.87, -11.81) * mm, "end": v(10.78, -14.81) * mm});
            skArc(sketch, "E7.3.2.25", {"start": v(42.53, 11.8) * mm, "mid": v(42.96, 9.72) * mm, "end": v(43.77, 7.76) * mm, "construction": true});
            skArc(sketch, "E7.3.2.26", {"start": v(54.57, 14.17) * mm, "mid": v(50.4, 12.98) * mm, "end": v(46.68, 10.75) * mm, "construction": true});
            skArc(sketch, "E7.3.2.27", {"start": v(56.44, 16.37) * mm, "mid": v(51.16, 15.45) * mm, "end": v(46.37, 13.05) * mm});
            skArc(sketch, "E7.3.2.28", {"start": v(52.34, 5.76) * mm, "mid": v(54.04, 9.81) * mm, "end": v(54.57, 14.17) * mm, "construction": true});
            skArc(sketch, "E7.3.2.29", {"start": v(54.66, 5.76) * mm, "mid": v(56.36, 10.93) * mm, "end": v(56.44, 16.37) * mm});
            skArc(sketch, "E7.3.2.30", {"start": v(40.46, 13.84) * mm, "mid": v(40.61, 10.85) * mm, "end": v(41.43, 7.97) * mm});
            skArc(sketch, "E7.3.2.31", {"start": v(46.37, 13.05) * mm, "mid": v(43.45, 13.75) * mm, "end": v(40.46, 13.84) * mm});
            skArc(sketch, "E7.3.3.0", {"start": v(28.6, -60.97) * mm, "mid": v(27.48, -54.71) * mm, "end": v(24.27, -49.23) * mm});
            skArc(sketch, "E7.3.3.1", {"start": v(24.27, -49.23) * mm, "mid": v(24.73, -46.27) * mm, "end": v(24.53, -43.28) * mm});
            skArc(sketch, "E7.3.3.2", {"start": v(18.67, -47.14) * mm, "mid": v(14.6, -45.45) * mm, "end": v(10.25, -44.91) * mm, "construction": true});
            skArc(sketch, "E7.3.3.3", {"start": v(16.66, -55.71) * mm, "mid": v(21.29, -58.16) * mm, "end": v(26.45, -59.04) * mm, "construction": true});
            skArc(sketch, "E7.3.3.4", {"start": v(8.05, -43.05) * mm, "mid": v(8.97, -48.32) * mm, "end": v(11.37, -53.11) * mm});
            skArc(sketch, "E7.3.3.5", {"start": v(41.24, -36.25) * mm, "mid": v(38.73, -42.07) * mm, "end": v(38.32, -48.4) * mm});
            skArc(sketch, "E7.3.3.6", {"start": v(43.57, -36.45) * mm, "mid": v(41.12, -41.08) * mm, "end": v(40.24, -46.25) * mm, "construction": true});
            skArc(sketch, "E7.3.3.7", {"start": v(16.45, -58.05) * mm, "mid": v(22.27, -60.56) * mm, "end": v(28.6, -60.97) * mm});
            skArc(sketch, "E7.3.3.8", {"start": v(18.66, -44.82) * mm, "mid": v(13.49, -43.13) * mm, "end": v(8.05, -43.05) * mm});
            skArc(sketch, "E7.3.3.9", {"start": v(40.24, -46.25) * mm, "mid": v(45.27, -44.77) * mm, "end": v(49.56, -41.76) * mm, "construction": true});
            skArc(sketch, "E7.3.3.10", {"start": v(10.25, -44.91) * mm, "mid": v(11.44, -49.09) * mm, "end": v(13.67, -52.8) * mm, "construction": true});
            skArc(sketch, "E7.3.3.11", {"start": v(26.45, -59.04) * mm, "mid": v(24.98, -54.01) * mm, "end": v(21.97, -49.73) * mm, "construction": true});
            skArc(sketch, "E7.3.3.12", {"start": v(38.32, -48.4) * mm, "mid": v(44.58, -47.28) * mm, "end": v(50.06, -44.06) * mm});
            skArc(sketch, "E7.3.3.13", {"start": v(56, -44.32) * mm, "mid": v(55.54, -41.3) * mm, "end": v(54.47, -38.45) * mm});
            skArc(sketch, "E7.3.3.14", {"start": v(12.62, -56.95) * mm, "mid": v(14.7, -56.52) * mm, "end": v(16.66, -55.71) * mm, "construction": true});
            skArc(sketch, "E7.3.3.15", {"start": v(22.71, -45.55) * mm, "mid": v(20.62, -46.17) * mm, "end": v(18.67, -47.14) * mm, "construction": true});
            skArc(sketch, "E7.3.3.16", {"start": v(46.48, -33.47) * mm, "mid": v(44.45, -32.76) * mm, "end": v(42.34, -32.41) * mm, "construction": true});
            skArc(sketch, "E7.3.3.17", {"start": v(53.74, -42.5) * mm, "mid": v(53.12, -40.41) * mm, "end": v(52.15, -38.46) * mm, "construction": true});
            skArc(sketch, "E7.3.3.18", {"start": v(24.53, -43.28) * mm, "mid": v(21.51, -43.75) * mm, "end": v(18.66, -44.82) * mm});
            skArc(sketch, "E7.3.3.19", {"start": v(10.58, -59.03) * mm, "mid": v(13.57, -58.87) * mm, "end": v(16.45, -58.05) * mm});
            skArc(sketch, "E7.3.3.20", {"start": v(49.56, -41.76) * mm, "mid": v(51.61, -42.33) * mm, "end": v(53.74, -42.5) * mm, "construction": true});
            skArc(sketch, "E7.3.3.21", {"start": v(13.67, -52.8) * mm, "mid": v(12.97, -54.83) * mm, "end": v(12.62, -56.95) * mm, "construction": true});
            skArc(sketch, "E7.3.3.22", {"start": v(21.97, -49.73) * mm, "mid": v(22.54, -47.67) * mm, "end": v(22.71, -45.55) * mm, "construction": true});
            skArc(sketch, "E7.3.3.23", {"start": v(50.06, -44.06) * mm, "mid": v(53.02, -44.53) * mm, "end": v(56, -44.32) * mm});
            skArc(sketch, "E7.3.3.24", {"start": v(11.37, -53.11) * mm, "mid": v(10.67, -56.03) * mm, "end": v(10.58, -59.03) * mm});
            skArc(sketch, "E7.3.3.25", {"start": v(42.34, -32.41) * mm, "mid": v(42.77, -34.5) * mm, "end": v(43.57, -36.45) * mm, "construction": true});
            skArc(sketch, "E7.3.3.26", {"start": v(54.37, -30.04) * mm, "mid": v(50.2, -31.23) * mm, "end": v(46.48, -33.47) * mm, "construction": true});
            skArc(sketch, "E7.3.3.27", {"start": v(56.24, -27.84) * mm, "mid": v(50.97, -28.77) * mm, "end": v(46.18, -31.16) * mm});
            skArc(sketch, "E7.3.3.28", {"start": v(52.15, -38.46) * mm, "mid": v(53.84, -34.4) * mm, "end": v(54.37, -30.04) * mm, "construction": true});
            skArc(sketch, "E7.3.3.29", {"start": v(54.47, -38.45) * mm, "mid": v(56.16, -33.28) * mm, "end": v(56.24, -27.84) * mm});
            skArc(sketch, "E7.3.3.30", {"start": v(40.26, -30.38) * mm, "mid": v(40.42, -33.37) * mm, "end": v(41.24, -36.25) * mm});
            skArc(sketch, "E7.3.3.31", {"start": v(46.18, -31.16) * mm, "mid": v(43.26, -30.47) * mm, "end": v(40.26, -30.38) * mm});
            skArc(sketch, "E7.3.4.0", {"start": v(28.4, -105.19) * mm, "mid": v(27.29, -98.93) * mm, "end": v(24.07, -93.44) * mm});
            skArc(sketch, "E7.3.4.1", {"start": v(24.07, -93.44) * mm, "mid": v(24.54, -90.49) * mm, "end": v(24.33, -87.5) * mm});
            skArc(sketch, "E7.3.4.2", {"start": v(18.47, -91.36) * mm, "mid": v(14.41, -89.66) * mm, "end": v(10.05, -89.13) * mm, "construction": true});
            skArc(sketch, "E7.3.4.3", {"start": v(16.46, -99.93) * mm, "mid": v(21.1, -102.38) * mm, "end": v(26.26, -103.26) * mm, "construction": true});
            skArc(sketch, "E7.3.4.4", {"start": v(7.85, -87.26) * mm, "mid": v(8.78, -92.54) * mm, "end": v(11.17, -97.33) * mm});
            skArc(sketch, "E7.3.4.5", {"start": v(41.04, -80.46) * mm, "mid": v(38.53, -86.28) * mm, "end": v(38.12, -92.6) * mm});
            skArc(sketch, "E7.3.4.6", {"start": v(43.38, -80.67) * mm, "mid": v(40.93, -85.3) * mm, "end": v(40.05, -90.46) * mm, "construction": true});
            skArc(sketch, "E7.3.4.7", {"start": v(16.26, -102.27) * mm, "mid": v(22.08, -104.78) * mm, "end": v(28.4, -105.19) * mm});
            skArc(sketch, "E7.3.4.8", {"start": v(18.46, -89.04) * mm, "mid": v(13.3, -87.34) * mm, "end": v(7.85, -87.26) * mm});
            skArc(sketch, "E7.3.4.9", {"start": v(40.05, -90.46) * mm, "mid": v(45.08, -89) * mm, "end": v(49.37, -85.98) * mm, "construction": true});
            skArc(sketch, "E7.3.4.10", {"start": v(10.05, -89.13) * mm, "mid": v(11.24, -93.3) * mm, "end": v(13.48, -97.02) * mm, "construction": true});
            skArc(sketch, "E7.3.4.11", {"start": v(26.26, -103.26) * mm, "mid": v(24.78, -98.23) * mm, "end": v(21.77, -93.94) * mm, "construction": true});
            skArc(sketch, "E7.3.4.12", {"start": v(38.12, -92.6) * mm, "mid": v(44.38, -91.5) * mm, "end": v(49.86, -88.28) * mm});
            skArc(sketch, "E7.3.4.13", {"start": v(55.81, -88.54) * mm, "mid": v(55.35, -85.52) * mm, "end": v(54.27, -82.67) * mm});
            skArc(sketch, "E7.3.4.14", {"start": v(12.42, -101.17) * mm, "mid": v(14.5, -100.74) * mm, "end": v(16.46, -99.93) * mm, "construction": true});
            skArc(sketch, "E7.3.4.15", {"start": v(22.52, -89.77) * mm, "mid": v(20.42, -90.39) * mm, "end": v(18.47, -91.36) * mm, "construction": true});
            skArc(sketch, "E7.3.4.16", {"start": v(46.29, -77.68) * mm, "mid": v(44.26, -76.98) * mm, "end": v(42.14, -76.63) * mm, "construction": true});
            skArc(sketch, "E7.3.4.17", {"start": v(53.54, -86.72) * mm, "mid": v(52.92, -84.63) * mm, "end": v(51.95, -82.68) * mm, "construction": true});
            skArc(sketch, "E7.3.4.18", {"start": v(24.33, -87.5) * mm, "mid": v(21.32, -87.96) * mm, "end": v(18.46, -89.04) * mm});
            skArc(sketch, "E7.3.4.19", {"start": v(10.39, -103.24) * mm, "mid": v(13.38, -103.09) * mm, "end": v(16.26, -102.27) * mm});
            skArc(sketch, "E7.3.4.20", {"start": v(49.37, -85.98) * mm, "mid": v(51.42, -86.55) * mm, "end": v(53.54, -86.72) * mm, "construction": true});
            skArc(sketch, "E7.3.4.21", {"start": v(13.48, -97.02) * mm, "mid": v(12.77, -99.05) * mm, "end": v(12.42, -101.17) * mm, "construction": true});
            skArc(sketch, "E7.3.4.22", {"start": v(21.77, -93.94) * mm, "mid": v(22.34, -91.89) * mm, "end": v(22.52, -89.77) * mm, "construction": true});
            skArc(sketch, "E7.3.4.23", {"start": v(49.86, -88.28) * mm, "mid": v(52.82, -88.74) * mm, "end": v(55.81, -88.54) * mm});
            skArc(sketch, "E7.3.4.24", {"start": v(11.17, -97.33) * mm, "mid": v(10.48, -100.25) * mm, "end": v(10.39, -103.24) * mm});
            skArc(sketch, "E7.3.4.25", {"start": v(42.14, -76.63) * mm, "mid": v(42.57, -78.7) * mm, "end": v(43.38, -80.67) * mm, "construction": true});
            skArc(sketch, "E7.3.4.26", {"start": v(54.18, -74.26) * mm, "mid": v(50, -75.45) * mm, "end": v(46.29, -77.68) * mm, "construction": true});
            skArc(sketch, "E7.3.4.27", {"start": v(56.05, -72.06) * mm, "mid": v(50.77, -72.98) * mm, "end": v(45.98, -75.38) * mm});
            skArc(sketch, "E7.3.4.28", {"start": v(51.95, -82.68) * mm, "mid": v(53.65, -78.62) * mm, "end": v(54.18, -74.26) * mm, "construction": true});
            skArc(sketch, "E7.3.4.29", {"start": v(54.27, -82.67) * mm, "mid": v(55.97, -77.5) * mm, "end": v(56.05, -72.06) * mm});
            skArc(sketch, "E7.3.4.30", {"start": v(40.07, -74.6) * mm, "mid": v(40.22, -77.58) * mm, "end": v(41.04, -80.46) * mm});
            skArc(sketch, "E7.3.4.31", {"start": v(45.98, -75.38) * mm, "mid": v(43.06, -74.68) * mm, "end": v(40.07, -74.6) * mm});
            skArc(sketch, "E7.4.0.0", {"start": v(89.6, 70.8) * mm, "mid": v(88.48, 77.05) * mm, "end": v(85.26, 82.54) * mm});
            skArc(sketch, "E7.4.0.1", {"start": v(85.26, 82.54) * mm, "mid": v(85.73, 85.5) * mm, "end": v(85.52, 88.48) * mm});
            skArc(sketch, "E7.4.0.2", {"start": v(79.66, 84.63) * mm, "mid": v(75.6, 86.32) * mm, "end": v(71.24, 86.85) * mm, "construction": true});
            skArc(sketch, "E7.4.0.3", {"start": v(77.66, 76.05) * mm, "mid": v(82.28, 73.6) * mm, "end": v(87.45, 72.72) * mm, "construction": true});
            skArc(sketch, "E7.4.0.4", {"start": v(69.04, 88.72) * mm, "mid": v(69.97, 83.45) * mm, "end": v(72.36, 78.65) * mm});
            skArc(sketch, "E7.4.0.5", {"start": v(102.23, 95.52) * mm, "mid": v(99.72, 89.7) * mm, "end": v(99.31, 83.37) * mm});
            skArc(sketch, "E7.4.0.6", {"start": v(104.57, 95.31) * mm, "mid": v(102.12, 90.68) * mm, "end": v(101.24, 85.52) * mm, "construction": true});
            skArc(sketch, "E7.4.0.7", {"start": v(77.45, 73.72) * mm, "mid": v(83.27, 71.2) * mm, "end": v(89.6, 70.8) * mm});
            skArc(sketch, "E7.4.0.8", {"start": v(79.66, 86.94) * mm, "mid": v(74.48, 88.64) * mm, "end": v(69.04, 88.72) * mm});
            skArc(sketch, "E7.4.0.9", {"start": v(101.24, 85.52) * mm, "mid": v(106.27, 87) * mm, "end": v(110.56, 90) * mm, "construction": true});
            skArc(sketch, "E7.4.0.10", {"start": v(71.24, 86.85) * mm, "mid": v(72.43, 82.68) * mm, "end": v(74.67, 78.96) * mm, "construction": true});
            skArc(sketch, "E7.4.0.11", {"start": v(87.45, 72.72) * mm, "mid": v(85.98, 77.75) * mm, "end": v(82.97, 82.04) * mm, "construction": true});
            skArc(sketch, "E7.4.0.12", {"start": v(99.31, 83.37) * mm, "mid": v(105.57, 84.5) * mm, "end": v(111.06, 87.7) * mm});
            skArc(sketch, "E7.4.0.13", {"start": v(117, 87.45) * mm, "mid": v(116.54, 90.46) * mm, "end": v(115.46, 93.31) * mm});
            skArc(sketch, "E7.4.0.14", {"start": v(73.61, 74.82) * mm, "mid": v(75.7, 75.24) * mm, "end": v(77.66, 76.05) * mm, "construction": true});
            skArc(sketch, "E7.4.0.15", {"start": v(83.7, 86.21) * mm, "mid": v(81.62, 85.6) * mm, "end": v(79.66, 84.63) * mm, "construction": true});
            skArc(sketch, "E7.4.0.16", {"start": v(107.48, 98.3) * mm, "mid": v(105.45, 99) * mm, "end": v(103.33, 99.36) * mm, "construction": true});
            skArc(sketch, "E7.4.0.17", {"start": v(114.73, 89.26) * mm, "mid": v(114.11, 91.35) * mm, "end": v(113.14, 93.3) * mm, "construction": true});
            skArc(sketch, "E7.4.0.18", {"start": v(85.52, 88.48) * mm, "mid": v(82.5, 88.02) * mm, "end": v(79.66, 86.94) * mm});
            skArc(sketch, "E7.4.0.19", {"start": v(71.58, 72.74) * mm, "mid": v(74.57, 72.9) * mm, "end": v(77.45, 73.72) * mm});
            skArc(sketch, "E7.4.0.20", {"start": v(110.56, 90) * mm, "mid": v(112.61, 89.44) * mm, "end": v(114.73, 89.26) * mm, "construction": true});
            skArc(sketch, "E7.4.0.21", {"start": v(74.67, 78.96) * mm, "mid": v(73.97, 76.93) * mm, "end": v(73.61, 74.82) * mm, "construction": true});
            skArc(sketch, "E7.4.0.22", {"start": v(82.97, 82.04) * mm, "mid": v(83.53, 84.1) * mm, "end": v(83.7, 86.21) * mm, "construction": true});
            skArc(sketch, "E7.4.0.23", {"start": v(111.06, 87.7) * mm, "mid": v(114.02, 87.24) * mm, "end": v(117, 87.45) * mm});
            skArc(sketch, "E7.4.0.24", {"start": v(72.36, 78.65) * mm, "mid": v(71.67, 75.74) * mm, "end": v(71.58, 72.74) * mm});
            skArc(sketch, "E7.4.0.25", {"start": v(103.33, 99.36) * mm, "mid": v(103.76, 97.28) * mm, "end": v(104.57, 95.31) * mm, "construction": true});
            skArc(sketch, "E7.4.0.26", {"start": v(115.37, 101.73) * mm, "mid": v(111.2, 100.53) * mm, "end": v(107.48, 98.3) * mm, "construction": true});
            skArc(sketch, "E7.4.0.27", {"start": v(117.24, 103.93) * mm, "mid": v(111.96, 103) * mm, "end": v(107.17, 100.6) * mm});
            skArc(sketch, "E7.4.0.28", {"start": v(113.14, 93.3) * mm, "mid": v(114.84, 97.36) * mm, "end": v(115.37, 101.73) * mm, "construction": true});
            skArc(sketch, "E7.4.0.29", {"start": v(115.46, 93.31) * mm, "mid": v(117.16, 98.48) * mm, "end": v(117.24, 103.93) * mm});
            skArc(sketch, "E7.4.0.30", {"start": v(101.26, 101.4) * mm, "mid": v(101.42, 98.4) * mm, "end": v(102.23, 95.52) * mm});
            skArc(sketch, "E7.4.0.31", {"start": v(107.17, 100.6) * mm, "mid": v(104.26, 101.3) * mm, "end": v(101.26, 101.4) * mm});
            skArc(sketch, "E7.4.1.0", {"start": v(89.4, 26.58) * mm, "mid": v(88.28, 32.84) * mm, "end": v(85.07, 38.32) * mm});
            skArc(sketch, "E7.4.1.1", {"start": v(85.07, 38.32) * mm, "mid": v(85.53, 41.28) * mm, "end": v(85.33, 44.27) * mm});
            skArc(sketch, "E7.4.1.2", {"start": v(79.47, 40.41) * mm, "mid": v(75.41, 42.1) * mm, "end": v(71.05, 42.64) * mm, "construction": true});
            skArc(sketch, "E7.4.1.3", {"start": v(77.46, 31.84) * mm, "mid": v(82.09, 29.39) * mm, "end": v(87.25, 28.5) * mm, "construction": true});
            skArc(sketch, "E7.4.1.4", {"start": v(68.85, 44.5) * mm, "mid": v(69.78, 39.23) * mm, "end": v(72.17, 34.44) * mm});
            skArc(sketch, "E7.4.1.5", {"start": v(102.04, 51.3) * mm, "mid": v(99.53, 45.48) * mm, "end": v(99.12, 39.16) * mm});
            skArc(sketch, "E7.4.1.6", {"start": v(104.38, 51.1) * mm, "mid": v(101.93, 46.47) * mm, "end": v(101.05, 41.3) * mm, "construction": true});
            skArc(sketch, "E7.4.1.7", {"start": v(77.25, 29.5) * mm, "mid": v(83.07, 26.99) * mm, "end": v(89.4, 26.58) * mm});
            skArc(sketch, "E7.4.1.8", {"start": v(79.46, 42.73) * mm, "mid": v(74.29, 44.42) * mm, "end": v(68.85, 44.5) * mm});
            skArc(sketch, "E7.4.1.9", {"start": v(101.05, 41.3) * mm, "mid": v(106.08, 42.78) * mm, "end": v(110.36, 45.79) * mm, "construction": true});
            skArc(sketch, "E7.4.1.10", {"start": v(71.05, 42.64) * mm, "mid": v(72.24, 38.46) * mm, "end": v(74.47, 34.74) * mm, "construction": true});
            skArc(sketch, "E7.4.1.11", {"start": v(87.25, 28.5) * mm, "mid": v(85.78, 33.54) * mm, "end": v(82.77, 37.83) * mm, "construction": true});
            skArc(sketch, "E7.4.1.12", {"start": v(99.12, 39.16) * mm, "mid": v(105.38, 40.28) * mm, "end": v(110.86, 43.49) * mm});
            skArc(sketch, "E7.4.1.13", {"start": v(116.8, 43.23) * mm, "mid": v(116.34, 46.24) * mm, "end": v(115.27, 49.1) * mm});
            skArc(sketch, "E7.4.1.14", {"start": v(73.42, 30.6) * mm, "mid": v(75.5, 31.03) * mm, "end": v(77.46, 31.84) * mm, "construction": true});
            skArc(sketch, "E7.4.1.15", {"start": v(83.51, 42) * mm, "mid": v(81.42, 41.38) * mm, "end": v(79.47, 40.41) * mm, "construction": true});
            skArc(sketch, "E7.4.1.16", {"start": v(107.28, 54.08) * mm, "mid": v(105.26, 54.79) * mm, "end": v(103.14, 55.14) * mm, "construction": true});
            skArc(sketch, "E7.4.1.17", {"start": v(114.54, 45.04) * mm, "mid": v(113.92, 47.14) * mm, "end": v(112.95, 49.1) * mm, "construction": true});
            skArc(sketch, "E7.4.1.18", {"start": v(85.33, 44.27) * mm, "mid": v(82.31, 43.8) * mm, "end": v(79.46, 42.73) * mm});
            skArc(sketch, "E7.4.1.19", {"start": v(71.38, 28.52) * mm, "mid": v(74.37, 28.68) * mm, "end": v(77.25, 29.5) * mm});
            skArc(sketch, "E7.4.1.20", {"start": v(110.36, 45.79) * mm, "mid": v(112.42, 45.22) * mm, "end": v(114.54, 45.04) * mm, "construction": true});
            skArc(sketch, "E7.4.1.21", {"start": v(74.47, 34.74) * mm, "mid": v(73.77, 32.72) * mm, "end": v(73.42, 30.6) * mm, "construction": true});
            skArc(sketch, "E7.4.1.22", {"start": v(82.77, 37.83) * mm, "mid": v(83.34, 39.88) * mm, "end": v(83.51, 42) * mm, "construction": true});
            skArc(sketch, "E7.4.1.23", {"start": v(110.86, 43.49) * mm, "mid": v(113.82, 43.02) * mm, "end": v(116.8, 43.23) * mm});
            skArc(sketch, "E7.4.1.24", {"start": v(72.17, 34.44) * mm, "mid": v(71.47, 31.52) * mm, "end": v(71.38, 28.52) * mm});
            skArc(sketch, "E7.4.1.25", {"start": v(103.14, 55.14) * mm, "mid": v(103.57, 53.06) * mm, "end": v(104.38, 51.1) * mm, "construction": true});
            skArc(sketch, "E7.4.1.26", {"start": v(115.18, 57.51) * mm, "mid": v(111, 56.32) * mm, "end": v(107.28, 54.08) * mm, "construction": true});
            skArc(sketch, "E7.4.1.27", {"start": v(117.04, 59.71) * mm, "mid": v(111.77, 58.78) * mm, "end": v(106.98, 56.39) * mm});
            skArc(sketch, "E7.4.1.28", {"start": v(112.95, 49.1) * mm, "mid": v(114.64, 53.15) * mm, "end": v(115.18, 57.51) * mm, "construction": true});
            skArc(sketch, "E7.4.1.29", {"start": v(115.27, 49.1) * mm, "mid": v(116.96, 54.27) * mm, "end": v(117.04, 59.71) * mm});
            skArc(sketch, "E7.4.1.30", {"start": v(101.06, 57.18) * mm, "mid": v(101.22, 54.18) * mm, "end": v(102.04, 51.3) * mm});
            skArc(sketch, "E7.4.1.31", {"start": v(106.98, 56.39) * mm, "mid": v(104.06, 57.09) * mm, "end": v(101.06, 57.18) * mm});
            skArc(sketch, "E7.4.2.0", {"start": v(89.2, -17.64) * mm, "mid": v(88.09, -11.38) * mm, "end": v(84.87, -5.9) * mm});
            skArc(sketch, "E7.4.2.1", {"start": v(84.87, -5.9) * mm, "mid": v(85.34, -2.93) * mm, "end": v(85.13, 0.05) * mm});
            skArc(sketch, "E7.4.2.2", {"start": v(79.27, -3.8) * mm, "mid": v(75.22, -2.1) * mm, "end": v(70.85, -1.58) * mm, "construction": true});
            skArc(sketch, "E7.4.2.3", {"start": v(77.27, -12.38) * mm, "mid": v(81.9, -14.83) * mm, "end": v(87.06, -15.7) * mm, "construction": true});
            skArc(sketch, "E7.4.2.4", {"start": v(68.65, 0.29) * mm, "mid": v(69.58, -4.99) * mm, "end": v(71.97, -9.78) * mm});
            skArc(sketch, "E7.4.2.5", {"start": v(101.84, 7.09) * mm, "mid": v(99.33, 1.27) * mm, "end": v(98.92, -5.06) * mm});
            skArc(sketch, "E7.4.2.6", {"start": v(104.18, 6.88) * mm, "mid": v(101.73, 2.25) * mm, "end": v(100.85, -2.9) * mm, "construction": true});
            skArc(sketch, "E7.4.2.7", {"start": v(77.06, -14.71) * mm, "mid": v(82.88, -17.23) * mm, "end": v(89.2, -17.64) * mm});
            skArc(sketch, "E7.4.2.8", {"start": v(79.27, -1.49) * mm, "mid": v(74.1, 0.2) * mm, "end": v(68.65, 0.29) * mm});
            skArc(sketch, "E7.4.2.9", {"start": v(100.85, -2.9) * mm, "mid": v(105.88, -1.44) * mm, "end": v(110.17, 1.57) * mm, "construction": true});
            skArc(sketch, "E7.4.2.10", {"start": v(70.85, -1.58) * mm, "mid": v(72.04, -5.75) * mm, "end": v(74.28, -9.47) * mm, "construction": true});
            skArc(sketch, "E7.4.2.11", {"start": v(87.06, -15.7) * mm, "mid": v(85.59, -10.68) * mm, "end": v(82.57, -6.39) * mm, "construction": true});
            skArc(sketch, "E7.4.2.12", {"start": v(98.92, -5.06) * mm, "mid": v(105.18, -3.94) * mm, "end": v(110.67, -0.73) * mm});
            skArc(sketch, "E7.4.2.13", {"start": v(116.61, -0.99) * mm, "mid": v(116.15, 2.03) * mm, "end": v(115.07, 4.88) * mm});
            skArc(sketch, "E7.4.2.14", {"start": v(73.22, -13.62) * mm, "mid": v(75.3, -13.19) * mm, "end": v(77.27, -12.38) * mm, "construction": true});
            skArc(sketch, "E7.4.2.15", {"start": v(83.32, -2.22) * mm, "mid": v(81.23, -2.84) * mm, "end": v(79.27, -3.8) * mm, "construction": true});
            skArc(sketch, "E7.4.2.16", {"start": v(107.09, 9.87) * mm, "mid": v(105.06, 10.57) * mm, "end": v(102.94, 10.93) * mm, "construction": true});
            skArc(sketch, "E7.4.2.17", {"start": v(114.34, 0.83) * mm, "mid": v(113.72, 2.92) * mm, "end": v(112.75, 4.88) * mm, "construction": true});
            skArc(sketch, "E7.4.2.18", {"start": v(85.13, 0.05) * mm, "mid": v(82.12, -0.41) * mm, "end": v(79.27, -1.49) * mm});
            skArc(sketch, "E7.4.2.19", {"start": v(71.19, -15.7) * mm, "mid": v(74.18, -15.53) * mm, "end": v(77.06, -14.71) * mm});
            skArc(sketch, "E7.4.2.20", {"start": v(110.17, 1.57) * mm, "mid": v(112.22, 1) * mm, "end": v(114.34, 0.83) * mm, "construction": true});
            skArc(sketch, "E7.4.2.21", {"start": v(74.28, -9.47) * mm, "mid": v(73.57, -11.5) * mm, "end": v(73.22, -13.62) * mm, "construction": true});
            skArc(sketch, "E7.4.2.22", {"start": v(82.57, -6.39) * mm, "mid": v(83.14, -4.34) * mm, "end": v(83.32, -2.22) * mm, "construction": true});
            skArc(sketch, "E7.4.2.23", {"start": v(110.67, -0.73) * mm, "mid": v(113.62, -1.2) * mm, "end": v(116.61, -0.99) * mm});
            skArc(sketch, "E7.4.2.24", {"start": v(71.97, -9.78) * mm, "mid": v(71.28, -12.7) * mm, "end": v(71.19, -15.7) * mm});
            skArc(sketch, "E7.4.2.25", {"start": v(102.94, 10.93) * mm, "mid": v(103.37, 8.85) * mm, "end": v(104.18, 6.88) * mm, "construction": true});
            skArc(sketch, "E7.4.2.26", {"start": v(114.98, 13.3) * mm, "mid": v(110.8, 12.1) * mm, "end": v(107.09, 9.87) * mm, "construction": true});
            skArc(sketch, "E7.4.2.27", {"start": v(116.85, 15.5) * mm, "mid": v(111.57, 14.57) * mm, "end": v(106.78, 12.17) * mm});
            skArc(sketch, "E7.4.2.28", {"start": v(112.75, 4.88) * mm, "mid": v(114.45, 8.93) * mm, "end": v(114.98, 13.3) * mm, "construction": true});
            skArc(sketch, "E7.4.2.29", {"start": v(115.07, 4.88) * mm, "mid": v(116.77, 10.05) * mm, "end": v(116.85, 15.5) * mm});
            skArc(sketch, "E7.4.2.30", {"start": v(100.87, 12.96) * mm, "mid": v(101.02, 9.97) * mm, "end": v(101.84, 7.09) * mm});
            skArc(sketch, "E7.4.2.31", {"start": v(106.78, 12.17) * mm, "mid": v(103.86, 12.87) * mm, "end": v(100.87, 12.96) * mm});
            skArc(sketch, "E7.4.3.0", {"start": v(89, -61.85) * mm, "mid": v(87.9, -55.6) * mm, "end": v(84.68, -50.1) * mm});
            skArc(sketch, "E7.4.3.1", {"start": v(84.68, -50.1) * mm, "mid": v(85.14, -47.15) * mm, "end": v(84.94, -44.16) * mm});
            skArc(sketch, "E7.4.3.2", {"start": v(79.08, -48.02) * mm, "mid": v(75.02, -46.33) * mm, "end": v(70.66, -45.8) * mm, "construction": true});
            skArc(sketch, "E7.4.3.3", {"start": v(77.07, -56.6) * mm, "mid": v(81.7, -59.04) * mm, "end": v(86.86, -59.92) * mm, "construction": true});
            skArc(sketch, "E7.4.3.4", {"start": v(68.46, -43.93) * mm, "mid": v(69.38, -49.2) * mm, "end": v(71.78, -54) * mm});
            skArc(sketch, "E7.4.3.5", {"start": v(101.65, -37.13) * mm, "mid": v(99.14, -42.95) * mm, "end": v(98.73, -49.27) * mm});
            skArc(sketch, "E7.4.3.6", {"start": v(103.98, -37.33) * mm, "mid": v(101.53, -41.96) * mm, "end": v(100.65, -47.12) * mm, "construction": true});
            skArc(sketch, "E7.4.3.7", {"start": v(76.86, -58.93) * mm, "mid": v(82.68, -61.44) * mm, "end": v(89, -61.85) * mm});
            skArc(sketch, "E7.4.3.8", {"start": v(79.07, -45.7) * mm, "mid": v(73.9, -44) * mm, "end": v(68.46, -43.93) * mm});
            skArc(sketch, "E7.4.3.9", {"start": v(100.65, -47.12) * mm, "mid": v(105.68, -45.65) * mm, "end": v(109.97, -42.64) * mm, "construction": true});
            skArc(sketch, "E7.4.3.10", {"start": v(70.66, -45.8) * mm, "mid": v(71.85, -49.97) * mm, "end": v(74.08, -53.69) * mm, "construction": true});
            skArc(sketch, "E7.4.3.11", {"start": v(86.86, -59.92) * mm, "mid": v(85.4, -54.9) * mm, "end": v(82.38, -50.6) * mm, "construction": true});
            skArc(sketch, "E7.4.3.12", {"start": v(98.73, -49.27) * mm, "mid": v(104.99, -48.15) * mm, "end": v(110.47, -44.94) * mm});
            skArc(sketch, "E7.4.3.13", {"start": v(116.42, -45.2) * mm, "mid": v(115.95, -42.19) * mm, "end": v(114.88, -39.33) * mm});
            skArc(sketch, "E7.4.3.14", {"start": v(73.03, -57.83) * mm, "mid": v(75.1, -57.4) * mm, "end": v(77.07, -56.6) * mm, "construction": true});
            skArc(sketch, "E7.4.3.15", {"start": v(83.12, -46.43) * mm, "mid": v(81.03, -47.05) * mm, "end": v(79.08, -48.02) * mm, "construction": true});
            skArc(sketch, "E7.4.3.16", {"start": v(106.9, -34.35) * mm, "mid": v(104.86, -33.64) * mm, "end": v(102.75, -33.29) * mm, "construction": true});
            skArc(sketch, "E7.4.3.17", {"start": v(114.15, -43.39) * mm, "mid": v(113.53, -41.3) * mm, "end": v(112.56, -39.34) * mm, "construction": true});
            skArc(sketch, "E7.4.3.18", {"start": v(84.94, -44.16) * mm, "mid": v(81.92, -44.63) * mm, "end": v(79.07, -45.7) * mm});
            skArc(sketch, "E7.4.3.19", {"start": v(71, -59.9) * mm, "mid": v(73.98, -59.75) * mm, "end": v(76.86, -58.93) * mm});
            skArc(sketch, "E7.4.3.20", {"start": v(109.97, -42.64) * mm, "mid": v(112.02, -43.21) * mm, "end": v(114.15, -43.39) * mm, "construction": true});
            skArc(sketch, "E7.4.3.21", {"start": v(74.08, -53.69) * mm, "mid": v(73.38, -55.71) * mm, "end": v(73.03, -57.83) * mm, "construction": true});
            skArc(sketch, "E7.4.3.22", {"start": v(82.38, -50.6) * mm, "mid": v(82.95, -48.55) * mm, "end": v(83.12, -46.43) * mm, "construction": true});
            skArc(sketch, "E7.4.3.23", {"start": v(110.47, -44.94) * mm, "mid": v(113.43, -45.4) * mm, "end": v(116.42, -45.2) * mm});
            skArc(sketch, "E7.4.3.24", {"start": v(71.78, -54) * mm, "mid": v(71.08, -56.9) * mm, "end": v(71, -59.9) * mm});
            skArc(sketch, "E7.4.3.25", {"start": v(102.75, -33.29) * mm, "mid": v(103.18, -35.37) * mm, "end": v(103.98, -37.33) * mm, "construction": true});
            skArc(sketch, "E7.4.3.26", {"start": v(114.78, -30.92) * mm, "mid": v(110.61, -32.11) * mm, "end": v(106.9, -34.35) * mm, "construction": true});
            skArc(sketch, "E7.4.3.27", {"start": v(116.65, -28.72) * mm, "mid": v(111.38, -29.65) * mm, "end": v(106.59, -32.04) * mm});
            skArc(sketch, "E7.4.3.28", {"start": v(112.56, -39.34) * mm, "mid": v(114.25, -35.28) * mm, "end": v(114.78, -30.92) * mm, "construction": true});
            skArc(sketch, "E7.4.3.29", {"start": v(114.88, -39.33) * mm, "mid": v(116.57, -34.16) * mm, "end": v(116.65, -28.72) * mm});
            skArc(sketch, "E7.4.3.30", {"start": v(100.67, -31.25) * mm, "mid": v(100.83, -34.25) * mm, "end": v(101.65, -37.13) * mm});
            skArc(sketch, "E7.4.3.31", {"start": v(106.59, -32.04) * mm, "mid": v(103.67, -31.35) * mm, "end": v(100.67, -31.25) * mm});
            skArc(sketch, "E7.4.4.0", {"start": v(88.81, -106.07) * mm, "mid": v(87.7, -99.8) * mm, "end": v(84.48, -94.32) * mm});
            skArc(sketch, "E7.4.4.1", {"start": v(84.48, -94.32) * mm, "mid": v(84.95, -91.36) * mm, "end": v(84.74, -88.38) * mm});
            skArc(sketch, "E7.4.4.2", {"start": v(78.88, -92.23) * mm, "mid": v(74.82, -90.54) * mm, "end": v(70.46, -90) * mm, "construction": true});
            skArc(sketch, "E7.4.4.3", {"start": v(76.87, -100.8) * mm, "mid": v(81.5, -103.26) * mm, "end": v(86.67, -104.14) * mm, "construction": true});
            skArc(sketch, "E7.4.4.4", {"start": v(68.26, -88.14) * mm, "mid": v(69.19, -93.42) * mm, "end": v(71.58, -98.2) * mm});
            skArc(sketch, "E7.4.4.5", {"start": v(101.45, -81.34) * mm, "mid": v(98.94, -87.16) * mm, "end": v(98.53, -93.49) * mm});
            skArc(sketch, "E7.4.4.6", {"start": v(103.79, -81.55) * mm, "mid": v(101.34, -86.18) * mm, "end": v(100.46, -91.34) * mm, "construction": true});
            skArc(sketch, "E7.4.4.7", {"start": v(76.67, -103.15) * mm, "mid": v(82.49, -105.66) * mm, "end": v(88.81, -106.07) * mm});
            skArc(sketch, "E7.4.4.8", {"start": v(78.87, -89.92) * mm, "mid": v(73.7, -88.22) * mm, "end": v(68.26, -88.14) * mm});
            skArc(sketch, "E7.4.4.9", {"start": v(100.46, -91.34) * mm, "mid": v(105.49, -89.87) * mm, "end": v(109.78, -86.86) * mm, "construction": true});
            skArc(sketch, "E7.4.4.10", {"start": v(70.46, -90) * mm, "mid": v(71.65, -94.18) * mm, "end": v(73.89, -97.9) * mm, "construction": true});
            skArc(sketch, "E7.4.4.11", {"start": v(86.67, -104.14) * mm, "mid": v(85.2, -99.1) * mm, "end": v(82.18, -94.82) * mm, "construction": true});
            skArc(sketch, "E7.4.4.12", {"start": v(98.53, -93.49) * mm, "mid": v(104.79, -92.37) * mm, "end": v(110.27, -89.16) * mm});
            skArc(sketch, "E7.4.4.13", {"start": v(116.22, -89.42) * mm, "mid": v(115.76, -86.4) * mm, "end": v(114.68, -83.55) * mm});
            skArc(sketch, "E7.4.4.14", {"start": v(72.83, -102.05) * mm, "mid": v(74.91, -101.62) * mm, "end": v(76.87, -100.8) * mm, "construction": true});
            skArc(sketch, "E7.4.4.15", {"start": v(82.93, -90.65) * mm, "mid": v(80.83, -91.27) * mm, "end": v(78.88, -92.23) * mm, "construction": true});
            skArc(sketch, "E7.4.4.16", {"start": v(106.7, -78.56) * mm, "mid": v(104.67, -77.86) * mm, "end": v(102.55, -77.5) * mm, "construction": true});
            skArc(sketch, "E7.4.4.17", {"start": v(113.95, -87.6) * mm, "mid": v(113.33, -85.5) * mm, "end": v(112.36, -83.55) * mm, "construction": true});
            skArc(sketch, "E7.4.4.18", {"start": v(84.74, -88.38) * mm, "mid": v(81.73, -88.84) * mm, "end": v(78.87, -89.92) * mm});
            skArc(sketch, "E7.4.4.19", {"start": v(70.8, -104.12) * mm, "mid": v(73.79, -103.96) * mm, "end": v(76.67, -103.15) * mm});
            skArc(sketch, "E7.4.4.20", {"start": v(109.78, -86.86) * mm, "mid": v(111.83, -87.43) * mm, "end": v(113.95, -87.6) * mm, "construction": true});
            skArc(sketch, "E7.4.4.21", {"start": v(73.89, -97.9) * mm, "mid": v(73.18, -99.93) * mm, "end": v(72.83, -102.05) * mm, "construction": true});
            skArc(sketch, "E7.4.4.22", {"start": v(82.18, -94.82) * mm, "mid": v(82.75, -92.77) * mm, "end": v(82.93, -90.65) * mm, "construction": true});
            skArc(sketch, "E7.4.4.23", {"start": v(110.27, -89.16) * mm, "mid": v(113.23, -89.62) * mm, "end": v(116.22, -89.42) * mm});
            skArc(sketch, "E7.4.4.24", {"start": v(71.58, -98.2) * mm, "mid": v(70.89, -101.12) * mm, "end": v(70.8, -104.12) * mm});
            skArc(sketch, "E7.4.4.25", {"start": v(102.55, -77.5) * mm, "mid": v(102.98, -79.59) * mm, "end": v(103.79, -81.55) * mm, "construction": true});
            skArc(sketch, "E7.4.4.26", {"start": v(114.59, -75.14) * mm, "mid": v(110.42, -76.33) * mm, "end": v(106.7, -78.56) * mm, "construction": true});
            skArc(sketch, "E7.4.4.27", {"start": v(116.46, -72.94) * mm, "mid": v(111.18, -73.86) * mm, "end": v(106.4, -76.26) * mm});
            skArc(sketch, "E7.4.4.28", {"start": v(112.36, -83.55) * mm, "mid": v(114.06, -79.5) * mm, "end": v(114.59, -75.14) * mm, "construction": true});
            skArc(sketch, "E7.4.4.29", {"start": v(114.68, -83.55) * mm, "mid": v(116.38, -78.38) * mm, "end": v(116.46, -72.94) * mm});
            skArc(sketch, "E7.4.4.30", {"start": v(100.48, -75.47) * mm, "mid": v(100.63, -78.46) * mm, "end": v(101.45, -81.34) * mm});
            skArc(sketch, "E7.4.4.31", {"start": v(106.4, -76.26) * mm, "mid": v(103.47, -75.56) * mm, "end": v(100.48, -75.47) * mm});
            skArc(sketch, "E7.5.0.0", {"start": v(150, 69.92) * mm, "mid": v(148.89, 76.17) * mm, "end": v(145.67, 81.66) * mm});
            skArc(sketch, "E7.5.0.1", {"start": v(145.67, 81.66) * mm, "mid": v(146.14, 84.62) * mm, "end": v(145.93, 87.6) * mm});
            skArc(sketch, "E7.5.0.2", {"start": v(140.07, 83.75) * mm, "mid": v(136.02, 85.44) * mm, "end": v(131.65, 85.97) * mm, "construction": true});
            skArc(sketch, "E7.5.0.3", {"start": v(138.07, 75.17) * mm, "mid": v(142.7, 72.72) * mm, "end": v(147.86, 71.84) * mm, "construction": true});
            skArc(sketch, "E7.5.0.4", {"start": v(129.45, 87.84) * mm, "mid": v(130.38, 82.57) * mm, "end": v(132.77, 77.78) * mm});
            skArc(sketch, "E7.5.0.5", {"start": v(162.64, 94.64) * mm, "mid": v(160.13, 88.82) * mm, "end": v(159.72, 82.5) * mm});
            skArc(sketch, "E7.5.0.6", {"start": v(164.98, 94.43) * mm, "mid": v(162.53, 89.8) * mm, "end": v(161.65, 84.64) * mm, "construction": true});
            skArc(sketch, "E7.5.0.7", {"start": v(137.86, 72.84) * mm, "mid": v(143.68, 70.33) * mm, "end": v(150, 69.92) * mm});
            skArc(sketch, "E7.5.0.8", {"start": v(140.07, 86.07) * mm, "mid": v(134.9, 87.76) * mm, "end": v(129.45, 87.84) * mm});
            skArc(sketch, "E7.5.0.9", {"start": v(161.65, 84.64) * mm, "mid": v(166.68, 86.11) * mm, "end": v(170.97, 89.12) * mm, "construction": true});
            skArc(sketch, "E7.5.0.10", {"start": v(131.65, 85.97) * mm, "mid": v(132.84, 81.8) * mm, "end": v(135.08, 78.08) * mm, "construction": true});
            skArc(sketch, "E7.5.0.11", {"start": v(147.86, 71.84) * mm, "mid": v(146.39, 76.87) * mm, "end": v(143.38, 81.16) * mm, "construction": true});
            skArc(sketch, "E7.5.0.12", {"start": v(159.72, 82.5) * mm, "mid": v(165.98, 83.61) * mm, "end": v(171.47, 86.83) * mm});
            skArc(sketch, "E7.5.0.13", {"start": v(177.41, 86.57) * mm, "mid": v(176.95, 89.58) * mm, "end": v(175.87, 92.43) * mm});
            skArc(sketch, "E7.5.0.14", {"start": v(134.02, 73.94) * mm, "mid": v(136.1, 74.36) * mm, "end": v(138.07, 75.17) * mm, "construction": true});
            skArc(sketch, "E7.5.0.15", {"start": v(144.12, 85.34) * mm, "mid": v(142.03, 84.72) * mm, "end": v(140.07, 83.75) * mm, "construction": true});
            skArc(sketch, "E7.5.0.16", {"start": v(167.89, 97.42) * mm, "mid": v(165.86, 98.12) * mm, "end": v(163.74, 98.48) * mm, "construction": true});
            skArc(sketch, "E7.5.0.17", {"start": v(175.14, 88.38) * mm, "mid": v(174.52, 90.47) * mm, "end": v(173.55, 92.43) * mm, "construction": true});
            skArc(sketch, "E7.5.0.18", {"start": v(145.93, 87.6) * mm, "mid": v(142.92, 87.14) * mm, "end": v(140.07, 86.07) * mm});
            skArc(sketch, "E7.5.0.19", {"start": v(131.99, 71.86) * mm, "mid": v(134.98, 72.02) * mm, "end": v(137.86, 72.84) * mm});
            skArc(sketch, "E7.5.0.20", {"start": v(170.97, 89.12) * mm, "mid": v(173.02, 88.56) * mm, "end": v(175.14, 88.38) * mm, "construction": true});
            skArc(sketch, "E7.5.0.21", {"start": v(135.08, 78.08) * mm, "mid": v(134.38, 76.05) * mm, "end": v(134.02, 73.94) * mm, "construction": true});
            skArc(sketch, "E7.5.0.22", {"start": v(143.38, 81.16) * mm, "mid": v(143.94, 83.21) * mm, "end": v(144.12, 85.34) * mm, "construction": true});
            skArc(sketch, "E7.5.0.23", {"start": v(171.47, 86.83) * mm, "mid": v(174.43, 86.36) * mm, "end": v(177.41, 86.57) * mm});
            skArc(sketch, "E7.5.0.24", {"start": v(132.77, 77.78) * mm, "mid": v(132.08, 74.86) * mm, "end": v(131.99, 71.86) * mm});
            skArc(sketch, "E7.5.0.25", {"start": v(163.74, 98.48) * mm, "mid": v(164.17, 96.4) * mm, "end": v(164.98, 94.43) * mm, "construction": true});
            skArc(sketch, "E7.5.0.26", {"start": v(175.78, 100.85) * mm, "mid": v(171.6, 99.66) * mm, "end": v(167.89, 97.42) * mm, "construction": true});
            skArc(sketch, "E7.5.0.27", {"start": v(177.65, 103.05) * mm, "mid": v(172.37, 102.12) * mm, "end": v(167.58, 99.73) * mm});
            skArc(sketch, "E7.5.0.28", {"start": v(173.55, 92.43) * mm, "mid": v(175.25, 96.48) * mm, "end": v(175.78, 100.85) * mm, "construction": true});
            skArc(sketch, "E7.5.0.29", {"start": v(175.87, 92.43) * mm, "mid": v(177.57, 97.6) * mm, "end": v(177.65, 103.05) * mm});
            skArc(sketch, "E7.5.0.30", {"start": v(161.67, 100.51) * mm, "mid": v(161.83, 97.52) * mm, "end": v(162.64, 94.64) * mm});
            skArc(sketch, "E7.5.0.31", {"start": v(167.58, 99.73) * mm, "mid": v(164.67, 100.42) * mm, "end": v(161.67, 100.51) * mm});
            skArc(sketch, "E7.5.1.0", {"start": v(149.81, 25.7) * mm, "mid": v(148.7, 31.96) * mm, "end": v(145.48, 37.44) * mm});
            skArc(sketch, "E7.5.1.1", {"start": v(145.48, 37.44) * mm, "mid": v(145.94, 40.4) * mm, "end": v(145.74, 43.4) * mm});
            skArc(sketch, "E7.5.1.2", {"start": v(139.88, 39.53) * mm, "mid": v(135.82, 41.23) * mm, "end": v(131.46, 41.76) * mm, "construction": true});
            skArc(sketch, "E7.5.1.3", {"start": v(137.87, 30.96) * mm, "mid": v(142.5, 28.5) * mm, "end": v(147.66, 27.63) * mm, "construction": true});
            skArc(sketch, "E7.5.1.4", {"start": v(129.26, 43.63) * mm, "mid": v(130.19, 38.35) * mm, "end": v(132.58, 33.56) * mm});
            skArc(sketch, "E7.5.1.5", {"start": v(162.45, 50.42) * mm, "mid": v(159.94, 44.6) * mm, "end": v(159.53, 38.28) * mm});
            skArc(sketch, "E7.5.1.6", {"start": v(164.79, 50.22) * mm, "mid": v(162.34, 45.59) * mm, "end": v(161.46, 40.43) * mm, "construction": true});
            skArc(sketch, "E7.5.1.7", {"start": v(137.66, 28.62) * mm, "mid": v(143.48, 26.1) * mm, "end": v(149.81, 25.7) * mm});
            skArc(sketch, "E7.5.1.8", {"start": v(139.87, 41.85) * mm, "mid": v(134.7, 43.54) * mm, "end": v(129.26, 43.63) * mm});
            skArc(sketch, "E7.5.1.9", {"start": v(161.46, 40.43) * mm, "mid": v(166.49, 41.9) * mm, "end": v(170.77, 44.9) * mm, "construction": true});
            skArc(sketch, "E7.5.1.10", {"start": v(131.46, 41.76) * mm, "mid": v(132.65, 37.59) * mm, "end": v(134.88, 33.86) * mm, "construction": true});
            skArc(sketch, "E7.5.1.11", {"start": v(147.66, 27.63) * mm, "mid": v(146.2, 32.66) * mm, "end": v(143.18, 36.95) * mm, "construction": true});
            skArc(sketch, "E7.5.1.12", {"start": v(159.53, 38.28) * mm, "mid": v(165.79, 39.4) * mm, "end": v(171.27, 42.61) * mm});
            skArc(sketch, "E7.5.1.13", {"start": v(177.22, 42.35) * mm, "mid": v(176.75, 45.37) * mm, "end": v(175.68, 48.22) * mm});
            skArc(sketch, "E7.5.1.14", {"start": v(133.83, 29.72) * mm, "mid": v(135.9, 30.15) * mm, "end": v(137.87, 30.96) * mm, "construction": true});
            skArc(sketch, "E7.5.1.15", {"start": v(143.92, 41.12) * mm, "mid": v(141.83, 40.5) * mm, "end": v(139.88, 39.53) * mm, "construction": true});
            skArc(sketch, "E7.5.1.16", {"start": v(167.7, 53.2) * mm, "mid": v(165.67, 53.9) * mm, "end": v(163.55, 54.26) * mm, "construction": true});
            skArc(sketch, "E7.5.1.17", {"start": v(174.95, 44.17) * mm, "mid": v(174.33, 46.26) * mm, "end": v(173.36, 48.21) * mm, "construction": true});
            skArc(sketch, "E7.5.1.18", {"start": v(145.74, 43.4) * mm, "mid": v(142.72, 42.93) * mm, "end": v(139.87, 41.85) * mm});
            skArc(sketch, "E7.5.1.19", {"start": v(131.8, 27.65) * mm, "mid": v(134.78, 27.8) * mm, "end": v(137.66, 28.62) * mm});
            skArc(sketch, "E7.5.1.20", {"start": v(170.77, 44.9) * mm, "mid": v(172.83, 44.34) * mm, "end": v(174.95, 44.17) * mm, "construction": true});
            skArc(sketch, "E7.5.1.21", {"start": v(134.88, 33.86) * mm, "mid": v(134.18, 31.84) * mm, "end": v(133.83, 29.72) * mm, "construction": true});
            skArc(sketch, "E7.5.1.22", {"start": v(143.18, 36.95) * mm, "mid": v(143.75, 39) * mm, "end": v(143.92, 41.12) * mm, "construction": true});
            skArc(sketch, "E7.5.1.23", {"start": v(171.27, 42.61) * mm, "mid": v(174.23, 42.15) * mm, "end": v(177.22, 42.35) * mm});
            skArc(sketch, "E7.5.1.24", {"start": v(132.58, 33.56) * mm, "mid": v(131.88, 30.64) * mm, "end": v(131.8, 27.65) * mm});
            skArc(sketch, "E7.5.1.25", {"start": v(163.55, 54.26) * mm, "mid": v(163.98, 52.18) * mm, "end": v(164.79, 50.22) * mm, "construction": true});
            skArc(sketch, "E7.5.1.26", {"start": v(175.59, 56.63) * mm, "mid": v(171.41, 55.44) * mm, "end": v(167.7, 53.2) * mm, "construction": true});
            skArc(sketch, "E7.5.1.27", {"start": v(177.45, 58.83) * mm, "mid": v(172.18, 57.9) * mm, "end": v(167.39, 55.51) * mm});
            skArc(sketch, "E7.5.1.28", {"start": v(173.36, 48.21) * mm, "mid": v(175.05, 52.27) * mm, "end": v(175.59, 56.63) * mm, "construction": true});
            skArc(sketch, "E7.5.1.29", {"start": v(175.68, 48.22) * mm, "mid": v(177.37, 53.4) * mm, "end": v(177.45, 58.83) * mm});
            skArc(sketch, "E7.5.1.30", {"start": v(161.47, 56.3) * mm, "mid": v(161.63, 53.3) * mm, "end": v(162.45, 50.42) * mm});
            skArc(sketch, "E7.5.1.31", {"start": v(167.39, 55.51) * mm, "mid": v(164.47, 56.2) * mm, "end": v(161.47, 56.3) * mm});
            skArc(sketch, "E7.5.2.0", {"start": v(149.61, -18.51) * mm, "mid": v(148.5, -12.26) * mm, "end": v(145.28, -6.77) * mm});
            skArc(sketch, "E7.5.2.1", {"start": v(145.28, -6.77) * mm, "mid": v(145.75, -3.81) * mm, "end": v(145.54, -0.83) * mm});
            skArc(sketch, "E7.5.2.2", {"start": v(139.68, -4.68) * mm, "mid": v(135.63, -2.99) * mm, "end": v(131.26, -2.46) * mm, "construction": true});
            skArc(sketch, "E7.5.2.3", {"start": v(137.68, -13.26) * mm, "mid": v(142.3, -15.7) * mm, "end": v(147.47, -16.59) * mm, "construction": true});
            skArc(sketch, "E7.5.2.4", {"start": v(129.06, -0.6) * mm, "mid": v(129.99, -5.86) * mm, "end": v(132.38, -10.66) * mm});
            skArc(sketch, "E7.5.2.5", {"start": v(162.25, 6.2) * mm, "mid": v(159.74, 0.39) * mm, "end": v(159.33, -5.94) * mm});
            skArc(sketch, "E7.5.2.6", {"start": v(164.59, 6) * mm, "mid": v(162.14, 1.37) * mm, "end": v(161.26, -3.79) * mm, "construction": true});
            skArc(sketch, "E7.5.2.7", {"start": v(137.47, -15.6) * mm, "mid": v(143.29, -18.1) * mm, "end": v(149.61, -18.51) * mm});
            skArc(sketch, "E7.5.2.8", {"start": v(139.68, -2.37) * mm, "mid": v(134.5, -0.67) * mm, "end": v(129.06, -0.6) * mm});
            skArc(sketch, "E7.5.2.9", {"start": v(161.26, -3.79) * mm, "mid": v(166.29, -2.32) * mm, "end": v(170.58, 0.7) * mm, "construction": true});
            skArc(sketch, "E7.5.2.10", {"start": v(131.26, -2.46) * mm, "mid": v(132.45, -6.63) * mm, "end": v(134.69, -10.35) * mm, "construction": true});
            skArc(sketch, "E7.5.2.11", {"start": v(147.47, -16.59) * mm, "mid": v(146, -11.56) * mm, "end": v(142.98, -7.27) * mm, "construction": true});
            skArc(sketch, "E7.5.2.12", {"start": v(159.33, -5.94) * mm, "mid": v(165.6, -4.82) * mm, "end": v(171.08, -1.6) * mm});
            skArc(sketch, "E7.5.2.13", {"start": v(177.02, -1.86) * mm, "mid": v(176.56, 1.15) * mm, "end": v(175.48, 4) * mm});
            skArc(sketch, "E7.5.2.14", {"start": v(133.63, -14.5) * mm, "mid": v(135.71, -14.07) * mm, "end": v(137.68, -13.26) * mm, "construction": true});
            skArc(sketch, "E7.5.2.15", {"start": v(143.73, -3.1) * mm, "mid": v(141.64, -3.71) * mm, "end": v(139.68, -4.68) * mm, "construction": true});
            skArc(sketch, "E7.5.2.16", {"start": v(167.5, 8.99) * mm, "mid": v(165.47, 9.7) * mm, "end": v(163.35, 10.05) * mm, "construction": true});
            skArc(sketch, "E7.5.2.17", {"start": v(174.75, -0.05) * mm, "mid": v(174.13, 2.04) * mm, "end": v(173.16, 4) * mm, "construction": true});
            skArc(sketch, "E7.5.2.18", {"start": v(145.54, -0.83) * mm, "mid": v(142.53, -1.29) * mm, "end": v(139.68, -2.37) * mm});
            skArc(sketch, "E7.5.2.19", {"start": v(131.6, -16.57) * mm, "mid": v(134.59, -16.41) * mm, "end": v(137.47, -15.6) * mm});
            skArc(sketch, "E7.5.2.20", {"start": v(170.58, 0.7) * mm, "mid": v(172.63, 0.13) * mm, "end": v(174.75, -0.05) * mm, "construction": true});
            skArc(sketch, "E7.5.2.21", {"start": v(134.69, -10.35) * mm, "mid": v(133.98, -12.38) * mm, "end": v(133.63, -14.5) * mm, "construction": true});
            skArc(sketch, "E7.5.2.22", {"start": v(142.98, -7.27) * mm, "mid": v(143.55, -5.22) * mm, "end": v(143.73, -3.1) * mm, "construction": true});
            skArc(sketch, "E7.5.2.23", {"start": v(171.08, -1.6) * mm, "mid": v(174.03, -2.07) * mm, "end": v(177.02, -1.86) * mm});
            skArc(sketch, "E7.5.2.24", {"start": v(132.38, -10.66) * mm, "mid": v(131.69, -13.57) * mm, "end": v(131.6, -16.57) * mm});
            skArc(sketch, "E7.5.2.25", {"start": v(163.35, 10.05) * mm, "mid": v(163.78, 7.97) * mm, "end": v(164.59, 6) * mm, "construction": true});
            skArc(sketch, "E7.5.2.26", {"start": v(175.4, 12.42) * mm, "mid": v(171.22, 11.22) * mm, "end": v(167.5, 8.99) * mm, "construction": true});
            skArc(sketch, "E7.5.2.27", {"start": v(177.26, 14.62) * mm, "mid": v(171.98, 13.69) * mm, "end": v(167.2, 11.3) * mm});
            skArc(sketch, "E7.5.2.28", {"start": v(173.16, 4) * mm, "mid": v(174.86, 8.05) * mm, "end": v(175.4, 12.42) * mm, "construction": true});
            skArc(sketch, "E7.5.2.29", {"start": v(175.48, 4) * mm, "mid": v(177.18, 9.17) * mm, "end": v(177.26, 14.62) * mm});
            skArc(sketch, "E7.5.2.30", {"start": v(161.28, 12.08) * mm, "mid": v(161.43, 9.1) * mm, "end": v(162.25, 6.2) * mm});
            skArc(sketch, "E7.5.2.31", {"start": v(167.2, 11.3) * mm, "mid": v(164.27, 12) * mm, "end": v(161.28, 12.08) * mm});
            skArc(sketch, "E7.5.3.0", {"start": v(149.42, -62.73) * mm, "mid": v(148.3, -56.47) * mm, "end": v(145.09, -50.99) * mm});
            skArc(sketch, "E7.5.3.1", {"start": v(145.09, -50.99) * mm, "mid": v(145.55, -48.03) * mm, "end": v(145.35, -45.04) * mm});
            skArc(sketch, "E7.5.3.2", {"start": v(139.49, -48.9) * mm, "mid": v(135.43, -47.2) * mm, "end": v(131.07, -46.67) * mm, "construction": true});
            skArc(sketch, "E7.5.3.3", {"start": v(137.48, -57.47) * mm, "mid": v(142.1, -59.92) * mm, "end": v(147.27, -60.8) * mm, "construction": true});
            skArc(sketch, "E7.5.3.4", {"start": v(128.87, -44.8) * mm, "mid": v(129.8, -50.08) * mm, "end": v(132.19, -54.87) * mm});
            skArc(sketch, "E7.5.3.5", {"start": v(162.06, -38) * mm, "mid": v(159.55, -43.83) * mm, "end": v(159.14, -50.15) * mm});
            skArc(sketch, "E7.5.3.6", {"start": v(164.4, -38.21) * mm, "mid": v(161.94, -42.84) * mm, "end": v(161.06, -48) * mm, "construction": true});
            skArc(sketch, "E7.5.3.7", {"start": v(137.27, -59.8) * mm, "mid": v(143.1, -62.32) * mm, "end": v(149.42, -62.73) * mm});
            skArc(sketch, "E7.5.3.8", {"start": v(139.48, -46.58) * mm, "mid": v(134.3, -44.89) * mm, "end": v(128.87, -44.8) * mm});
            skArc(sketch, "E7.5.3.9", {"start": v(161.06, -48) * mm, "mid": v(166.1, -46.53) * mm, "end": v(170.38, -43.52) * mm, "construction": true});
            skArc(sketch, "E7.5.3.10", {"start": v(131.07, -46.67) * mm, "mid": v(132.26, -50.85) * mm, "end": v(134.5, -54.57) * mm, "construction": true});
            skArc(sketch, "E7.5.3.11", {"start": v(147.27, -60.8) * mm, "mid": v(145.8, -55.77) * mm, "end": v(142.79, -51.48) * mm, "construction": true});
            skArc(sketch, "E7.5.3.12", {"start": v(159.14, -50.15) * mm, "mid": v(165.4, -49.03) * mm, "end": v(170.88, -45.82) * mm});
            skArc(sketch, "E7.5.3.13", {"start": v(176.83, -46.08) * mm, "mid": v(176.36, -43.07) * mm, "end": v(175.29, -40.21) * mm});
            skArc(sketch, "E7.5.3.14", {"start": v(133.44, -58.7) * mm, "mid": v(135.52, -58.28) * mm, "end": v(137.48, -57.47) * mm, "construction": true});
            skArc(sketch, "E7.5.3.15", {"start": v(143.53, -47.31) * mm, "mid": v(141.44, -47.93) * mm, "end": v(139.49, -48.9) * mm, "construction": true});
            skArc(sketch, "E7.5.3.16", {"start": v(167.3, -35.23) * mm, "mid": v(165.27, -34.52) * mm, "end": v(163.16, -34.17) * mm, "construction": true});
            skArc(sketch, "E7.5.3.17", {"start": v(174.56, -44.27) * mm, "mid": v(173.94, -42.17) * mm, "end": v(172.97, -40.22) * mm, "construction": true});
            skArc(sketch, "E7.5.3.18", {"start": v(145.35, -45.04) * mm, "mid": v(142.33, -45.5) * mm, "end": v(139.48, -46.58) * mm});
            skArc(sketch, "E7.5.3.19", {"start": v(131.4, -60.79) * mm, "mid": v(134.4, -60.63) * mm, "end": v(137.27, -59.8) * mm});
            skArc(sketch, "E7.5.3.20", {"start": v(170.38, -43.52) * mm, "mid": v(172.43, -44.1) * mm, "end": v(174.56, -44.27) * mm, "construction": true});
            skArc(sketch, "E7.5.3.21", {"start": v(134.5, -54.57) * mm, "mid": v(133.79, -56.6) * mm, "end": v(133.44, -58.7) * mm, "construction": true});
            skArc(sketch, "E7.5.3.22", {"start": v(142.79, -51.48) * mm, "mid": v(143.36, -49.43) * mm, "end": v(143.53, -47.31) * mm, "construction": true});
            skArc(sketch, "E7.5.3.23", {"start": v(170.88, -45.82) * mm, "mid": v(173.84, -46.29) * mm, "end": v(176.83, -46.08) * mm});
            skArc(sketch, "E7.5.3.24", {"start": v(132.19, -54.87) * mm, "mid": v(131.5, -57.79) * mm, "end": v(131.4, -60.79) * mm});
            skArc(sketch, "E7.5.3.25", {"start": v(163.16, -34.17) * mm, "mid": v(163.59, -36.25) * mm, "end": v(164.4, -38.21) * mm, "construction": true});
            skArc(sketch, "E7.5.3.26", {"start": v(175.2, -31.8) * mm, "mid": v(171.02, -33) * mm, "end": v(167.3, -35.23) * mm, "construction": true});
            skArc(sketch, "E7.5.3.27", {"start": v(177.06, -29.6) * mm, "mid": v(171.79, -30.53) * mm, "end": v(167, -32.92) * mm});
            skArc(sketch, "E7.5.3.28", {"start": v(172.97, -40.22) * mm, "mid": v(174.66, -36.16) * mm, "end": v(175.2, -31.8) * mm, "construction": true});
            skArc(sketch, "E7.5.3.29", {"start": v(175.29, -40.21) * mm, "mid": v(176.98, -35.04) * mm, "end": v(177.06, -29.6) * mm});
            skArc(sketch, "E7.5.3.30", {"start": v(161.08, -32.13) * mm, "mid": v(161.24, -35.12) * mm, "end": v(162.06, -38) * mm});
            skArc(sketch, "E7.5.3.31", {"start": v(167, -32.92) * mm, "mid": v(164.08, -32.22) * mm, "end": v(161.08, -32.13) * mm});
            skArc(sketch, "E7.5.4.0", {"start": v(149.22, -106.95) * mm, "mid": v(148.1, -100.69) * mm, "end": v(144.9, -95.2) * mm});
            skArc(sketch, "E7.5.4.1", {"start": v(144.9, -95.2) * mm, "mid": v(145.36, -92.24) * mm, "end": v(145.15, -89.26) * mm});
            skArc(sketch, "E7.5.4.2", {"start": v(139.29, -93.11) * mm, "mid": v(135.23, -91.42) * mm, "end": v(130.87, -90.89) * mm, "construction": true});
            skArc(sketch, "E7.5.4.3", {"start": v(137.28, -101.69) * mm, "mid": v(141.91, -104.14) * mm, "end": v(147.08, -105.02) * mm, "construction": true});
            skArc(sketch, "E7.5.4.4", {"start": v(128.67, -89.02) * mm, "mid": v(129.6, -94.3) * mm, "end": v(132, -99.09) * mm});
            skArc(sketch, "E7.5.4.5", {"start": v(161.86, -82.22) * mm, "mid": v(159.35, -88.04) * mm, "end": v(158.94, -94.37) * mm});
            skArc(sketch, "E7.5.4.6", {"start": v(164.2, -82.43) * mm, "mid": v(161.75, -87.06) * mm, "end": v(160.87, -92.22) * mm, "construction": true});
            skArc(sketch, "E7.5.4.7", {"start": v(137.08, -104.02) * mm, "mid": v(142.9, -106.54) * mm, "end": v(149.22, -106.95) * mm});
            skArc(sketch, "E7.5.4.8", {"start": v(139.28, -90.8) * mm, "mid": v(134.11, -89.1) * mm, "end": v(128.67, -89.02) * mm});
            skArc(sketch, "E7.5.4.9", {"start": v(160.87, -92.22) * mm, "mid": v(165.9, -90.75) * mm, "end": v(170.19, -87.74) * mm, "construction": true});
            skArc(sketch, "E7.5.4.10", {"start": v(130.87, -90.89) * mm, "mid": v(132.06, -95.06) * mm, "end": v(134.3, -98.78) * mm, "construction": true});
            skArc(sketch, "E7.5.4.11", {"start": v(147.08, -105.02) * mm, "mid": v(145.6, -99.99) * mm, "end": v(142.6, -95.7) * mm, "construction": true});
            skArc(sketch, "E7.5.4.12", {"start": v(158.94, -94.37) * mm, "mid": v(165.2, -93.25) * mm, "end": v(170.68, -90.04) * mm});
            skArc(sketch, "E7.5.4.13", {"start": v(176.63, -90.3) * mm, "mid": v(176.17, -87.28) * mm, "end": v(175.1, -84.43) * mm});
            skArc(sketch, "E7.5.4.14", {"start": v(133.24, -102.93) * mm, "mid": v(135.32, -102.5) * mm, "end": v(137.28, -101.69) * mm, "construction": true});
            skArc(sketch, "E7.5.4.15", {"start": v(143.34, -91.53) * mm, "mid": v(141.24, -92.15) * mm, "end": v(139.29, -93.11) * mm, "construction": true});
            skArc(sketch, "E7.5.4.16", {"start": v(167.1, -79.44) * mm, "mid": v(165.08, -78.74) * mm, "end": v(162.96, -78.38) * mm, "construction": true});
            skArc(sketch, "E7.5.4.17", {"start": v(174.36, -88.48) * mm, "mid": v(173.74, -86.39) * mm, "end": v(172.77, -84.43) * mm, "construction": true});
            skArc(sketch, "E7.5.4.18", {"start": v(145.15, -89.26) * mm, "mid": v(142.14, -89.72) * mm, "end": v(139.28, -90.8) * mm});
            skArc(sketch, "E7.5.4.19", {"start": v(131.2, -105) * mm, "mid": v(134.2, -104.84) * mm, "end": v(137.08, -104.02) * mm});
            skArc(sketch, "E7.5.4.20", {"start": v(170.19, -87.74) * mm, "mid": v(172.24, -88.3) * mm, "end": v(174.36, -88.48) * mm, "construction": true});
            skArc(sketch, "E7.5.4.21", {"start": v(134.3, -98.78) * mm, "mid": v(133.6, -100.8) * mm, "end": v(133.24, -102.93) * mm, "construction": true});
            skArc(sketch, "E7.5.4.22", {"start": v(142.6, -95.7) * mm, "mid": v(143.16, -93.65) * mm, "end": v(143.34, -91.53) * mm, "construction": true});
            skArc(sketch, "E7.5.4.23", {"start": v(170.68, -90.04) * mm, "mid": v(173.64, -90.5) * mm, "end": v(176.63, -90.3) * mm});
            skArc(sketch, "E7.5.4.24", {"start": v(132, -99.09) * mm, "mid": v(131.3, -102) * mm, "end": v(131.2, -105) * mm});
            skArc(sketch, "E7.5.4.25", {"start": v(162.96, -78.38) * mm, "mid": v(163.4, -80.46) * mm, "end": v(164.2, -82.43) * mm, "construction": true});
            skArc(sketch, "E7.5.4.26", {"start": v(175, -76.02) * mm, "mid": v(170.83, -77.2) * mm, "end": v(167.1, -79.44) * mm, "construction": true});
            skArc(sketch, "E7.5.4.27", {"start": v(176.87, -73.81) * mm, "mid": v(171.6, -74.74) * mm, "end": v(166.8, -77.14) * mm});
            skArc(sketch, "E7.5.4.28", {"start": v(172.77, -84.43) * mm, "mid": v(174.47, -80.38) * mm, "end": v(175, -76.02) * mm, "construction": true});
            skArc(sketch, "E7.5.4.29", {"start": v(175.1, -84.43) * mm, "mid": v(176.79, -79.26) * mm, "end": v(176.87, -73.81) * mm});
            skArc(sketch, "E7.5.4.30", {"start": v(160.89, -76.35) * mm, "mid": v(161.04, -79.34) * mm, "end": v(161.86, -82.22) * mm});
            skArc(sketch, "E7.5.4.31", {"start": v(166.8, -77.14) * mm, "mid": v(163.88, -76.44) * mm, "end": v(160.89, -76.35) * mm});
            skLineSegment(sketch, "E7.direction1", {"start": v(-169.26, 89.6) * mm, "end": v(-108.85, 88.72) * mm, "construction": true});
            skLineSegment(sketch, "E7.direction2", {"start": v(-169.26, 89.6) * mm, "end": v(-169.46, 45.38) * mm, "construction": true});
            skSolve(sketch);
        }
        {
            var Q0;
            Q0=makeQuery(id+"F1.imprint","IMPRINT",FACE,{"disambiguationData":[TD([[makeQuery(id+"F1.imprint","IMPRINT",EDGE,{"derivedFrom":sQuery(id+"F1.wireOp",EDGE,"E5.0")}),-1.0]])]});
            extrude(context, id + "F2", {"entities" : qUnion([Q0]), "depth" : 2.54 * mm, "offsetDistance" : 25.4 * mm, "hasSecondDirection" : true, "secondDirectionOppositeDirection" : false, "secondDirectionDepth" : 1.27 * mm});
        }
        {
            var Q0;
            Q0 = qSketchRegion(id + "F1", true);
            extrude(context, id + "F3", {"entities" : qUnion([Q0]), "operationType" : NewBodyOperationType.ADD, "depth" : 5.08 * mm, "offsetDistance" : 25.4 * mm, "hasSecondDirection" : true, "secondDirectionOppositeDirection" : false, "secondDirectionDepth" : 1.27 * mm});
        }
        {
            var Q0;
            Q0=makeQuery(id+"F3.opExtrude","CAP_FACE",FACE,{"disambiguationData":[OSD([sQuery(id+"F1.wireOp",EDGE,"E5.0"),sQuery(id+"F1.wireOp",EDGE,"E5.3"),sQuery(id+"F1.wireOp",EDGE,"E5.8"),sQuery(id+"F1.wireOp",EDGE,"E5.9"),sQuery(id+"F1.wireOp",EDGE,"E5.10"),sQuery(id+"F1.wireOp",EDGE,"E5.13"),sQuery(id+"F1.wireOp",EDGE,"E5.14"),sQuery(id+"F1.wireOp",EDGE,"E5.15")])],"isStart":false});
            var Q1;
            Q1=makeQuery(id+"F3.opExtrude","CAP_FACE",FACE,{"disambiguationData":[OSD([sQuery(id+"F1.wireOp",EDGE,"E6.0"),sQuery(id+"F1.wireOp",EDGE,"E6.4"),sQuery(id+"F1.wireOp",EDGE,"E6.5"),sQuery(id+"F1.wireOp",EDGE,"E6.6"),sQuery(id+"F1.wireOp",EDGE,"E6.12"),sQuery(id+"F1.wireOp",EDGE,"E6.13"),sQuery(id+"F1.wireOp",EDGE,"E6.14"),sQuery(id+"F1.wireOp",EDGE,"E6.15")])],"isStart":false});
            var Q2;
            Q2=makeQuery(id+"F3.opExtrude","CAP_FACE",FACE,{"disambiguationData":[OSD([sQuery(id+"F1.wireOp",EDGE,"E7.0.1.0"),sQuery(id+"F1.wireOp",EDGE,"E7.0.1.1"),sQuery(id+"F1.wireOp",EDGE,"E7.0.1.4"),sQuery(id+"F1.wireOp",EDGE,"E7.0.1.7"),sQuery(id+"F1.wireOp",EDGE,"E7.0.1.8"),sQuery(id+"F1.wireOp",EDGE,"E7.0.1.18"),sQuery(id+"F1.wireOp",EDGE,"E7.0.1.19"),sQuery(id+"F1.wireOp",EDGE,"E7.0.1.24")])],"isStart":false});
            var Q3;
            Q3=makeQuery(id+"F3.opExtrude","CAP_FACE",FACE,{"disambiguationData":[OSD([sQuery(id+"F1.wireOp",EDGE,"E7.0.1.5"),sQuery(id+"F1.wireOp",EDGE,"E7.0.1.12"),sQuery(id+"F1.wireOp",EDGE,"E7.0.1.13"),sQuery(id+"F1.wireOp",EDGE,"E7.0.1.23"),sQuery(id+"F1.wireOp",EDGE,"E7.0.1.27"),sQuery(id+"F1.wireOp",EDGE,"E7.0.1.29"),sQuery(id+"F1.wireOp",EDGE,"E7.0.1.30"),sQuery(id+"F1.wireOp",EDGE,"E7.0.1.31")])],"isStart":false});
            var Q4;
            Q4=makeQuery(id+"F3.opExtrude","CAP_FACE",FACE,{"disambiguationData":[OSD([sQuery(id+"F1.wireOp",EDGE,"E7.0.2.0"),sQuery(id+"F1.wireOp",EDGE,"E7.0.2.1"),sQuery(id+"F1.wireOp",EDGE,"E7.0.2.4"),sQuery(id+"F1.wireOp",EDGE,"E7.0.2.7"),sQuery(id+"F1.wireOp",EDGE,"E7.0.2.8"),sQuery(id+"F1.wireOp",EDGE,"E7.0.2.18"),sQuery(id+"F1.wireOp",EDGE,"E7.0.2.19"),sQuery(id+"F1.wireOp",EDGE,"E7.0.2.24")])],"isStart":false});
            var Q5;
            Q5=makeQuery(id+"F3.opExtrude","CAP_FACE",FACE,{"disambiguationData":[OSD([sQuery(id+"F1.wireOp",EDGE,"E7.0.2.5"),sQuery(id+"F1.wireOp",EDGE,"E7.0.2.12"),sQuery(id+"F1.wireOp",EDGE,"E7.0.2.13"),sQuery(id+"F1.wireOp",EDGE,"E7.0.2.23"),sQuery(id+"F1.wireOp",EDGE,"E7.0.2.27"),sQuery(id+"F1.wireOp",EDGE,"E7.0.2.29"),sQuery(id+"F1.wireOp",EDGE,"E7.0.2.30"),sQuery(id+"F1.wireOp",EDGE,"E7.0.2.31")])],"isStart":false});
            var Q6;
            Q6=makeQuery(id+"F3.opExtrude","CAP_FACE",FACE,{"disambiguationData":[OSD([sQuery(id+"F1.wireOp",EDGE,"E7.0.3.0"),sQuery(id+"F1.wireOp",EDGE,"E7.0.3.1"),sQuery(id+"F1.wireOp",EDGE,"E7.0.3.4"),sQuery(id+"F1.wireOp",EDGE,"E7.0.3.7"),sQuery(id+"F1.wireOp",EDGE,"E7.0.3.8"),sQuery(id+"F1.wireOp",EDGE,"E7.0.3.18"),sQuery(id+"F1.wireOp",EDGE,"E7.0.3.19"),sQuery(id+"F1.wireOp",EDGE,"E7.0.3.24")])],"isStart":false});
            var Q7;
            Q7=makeQuery(id+"F3.opExtrude","CAP_FACE",FACE,{"disambiguationData":[OSD([sQuery(id+"F1.wireOp",EDGE,"E7.0.3.5"),sQuery(id+"F1.wireOp",EDGE,"E7.0.3.12"),sQuery(id+"F1.wireOp",EDGE,"E7.0.3.13"),sQuery(id+"F1.wireOp",EDGE,"E7.0.3.23"),sQuery(id+"F1.wireOp",EDGE,"E7.0.3.27"),sQuery(id+"F1.wireOp",EDGE,"E7.0.3.29"),sQuery(id+"F1.wireOp",EDGE,"E7.0.3.30"),sQuery(id+"F1.wireOp",EDGE,"E7.0.3.31")])],"isStart":false});
            var Q8;
            Q8=makeQuery(id+"F3.opExtrude","CAP_FACE",FACE,{"disambiguationData":[OSD([sQuery(id+"F1.wireOp",EDGE,"E7.0.4.0"),sQuery(id+"F1.wireOp",EDGE,"E7.0.4.1"),sQuery(id+"F1.wireOp",EDGE,"E7.0.4.4"),sQuery(id+"F1.wireOp",EDGE,"E7.0.4.7"),sQuery(id+"F1.wireOp",EDGE,"E7.0.4.8"),sQuery(id+"F1.wireOp",EDGE,"E7.0.4.18"),sQuery(id+"F1.wireOp",EDGE,"E7.0.4.19"),sQuery(id+"F1.wireOp",EDGE,"E7.0.4.24")])],"isStart":false});
            var Q9;
            Q9=makeQuery(id+"F3.opExtrude","CAP_FACE",FACE,{"disambiguationData":[OSD([sQuery(id+"F1.wireOp",EDGE,"E7.0.4.5"),sQuery(id+"F1.wireOp",EDGE,"E7.0.4.12"),sQuery(id+"F1.wireOp",EDGE,"E7.0.4.13"),sQuery(id+"F1.wireOp",EDGE,"E7.0.4.23"),sQuery(id+"F1.wireOp",EDGE,"E7.0.4.27"),sQuery(id+"F1.wireOp",EDGE,"E7.0.4.29"),sQuery(id+"F1.wireOp",EDGE,"E7.0.4.30"),sQuery(id+"F1.wireOp",EDGE,"E7.0.4.31")])],"isStart":false});
            var Q10;
            Q10=makeQuery(id+"F3.opExtrude","CAP_FACE",FACE,{"disambiguationData":[OSD([sQuery(id+"F1.wireOp",EDGE,"E7.1.0.0"),sQuery(id+"F1.wireOp",EDGE,"E7.1.0.1"),sQuery(id+"F1.wireOp",EDGE,"E7.1.0.4"),sQuery(id+"F1.wireOp",EDGE,"E7.1.0.7"),sQuery(id+"F1.wireOp",EDGE,"E7.1.0.8"),sQuery(id+"F1.wireOp",EDGE,"E7.1.0.18"),sQuery(id+"F1.wireOp",EDGE,"E7.1.0.19"),sQuery(id+"F1.wireOp",EDGE,"E7.1.0.24")])],"isStart":false});
            var Q11;
            Q11=makeQuery(id+"F3.opExtrude","CAP_FACE",FACE,{"disambiguationData":[OSD([sQuery(id+"F1.wireOp",EDGE,"E7.1.0.5"),sQuery(id+"F1.wireOp",EDGE,"E7.1.0.12"),sQuery(id+"F1.wireOp",EDGE,"E7.1.0.13"),sQuery(id+"F1.wireOp",EDGE,"E7.1.0.23"),sQuery(id+"F1.wireOp",EDGE,"E7.1.0.27"),sQuery(id+"F1.wireOp",EDGE,"E7.1.0.29"),sQuery(id+"F1.wireOp",EDGE,"E7.1.0.30"),sQuery(id+"F1.wireOp",EDGE,"E7.1.0.31")])],"isStart":false});
            var Q12;
            Q12=makeQuery(id+"F3.opExtrude","CAP_FACE",FACE,{"disambiguationData":[OSD([sQuery(id+"F1.wireOp",EDGE,"E7.1.1.0"),sQuery(id+"F1.wireOp",EDGE,"E7.1.1.1"),sQuery(id+"F1.wireOp",EDGE,"E7.1.1.4"),sQuery(id+"F1.wireOp",EDGE,"E7.1.1.7"),sQuery(id+"F1.wireOp",EDGE,"E7.1.1.8"),sQuery(id+"F1.wireOp",EDGE,"E7.1.1.18"),sQuery(id+"F1.wireOp",EDGE,"E7.1.1.19"),sQuery(id+"F1.wireOp",EDGE,"E7.1.1.24")])],"isStart":false});
            var Q13;
            Q13=makeQuery(id+"F3.opExtrude","CAP_FACE",FACE,{"disambiguationData":[OSD([sQuery(id+"F1.wireOp",EDGE,"E7.1.1.5"),sQuery(id+"F1.wireOp",EDGE,"E7.1.1.12"),sQuery(id+"F1.wireOp",EDGE,"E7.1.1.13"),sQuery(id+"F1.wireOp",EDGE,"E7.1.1.23"),sQuery(id+"F1.wireOp",EDGE,"E7.1.1.27"),sQuery(id+"F1.wireOp",EDGE,"E7.1.1.29"),sQuery(id+"F1.wireOp",EDGE,"E7.1.1.30"),sQuery(id+"F1.wireOp",EDGE,"E7.1.1.31")])],"isStart":false});
            var Q14;
            Q14=makeQuery(id+"F3.opExtrude","CAP_FACE",FACE,{"disambiguationData":[OSD([sQuery(id+"F1.wireOp",EDGE,"E7.1.2.0"),sQuery(id+"F1.wireOp",EDGE,"E7.1.2.1"),sQuery(id+"F1.wireOp",EDGE,"E7.1.2.4"),sQuery(id+"F1.wireOp",EDGE,"E7.1.2.7"),sQuery(id+"F1.wireOp",EDGE,"E7.1.2.8"),sQuery(id+"F1.wireOp",EDGE,"E7.1.2.18"),sQuery(id+"F1.wireOp",EDGE,"E7.1.2.19"),sQuery(id+"F1.wireOp",EDGE,"E7.1.2.24")])],"isStart":false});
            var Q15;
            Q15=makeQuery(id+"F3.opExtrude","CAP_FACE",FACE,{"disambiguationData":[OSD([sQuery(id+"F1.wireOp",EDGE,"E7.1.2.5"),sQuery(id+"F1.wireOp",EDGE,"E7.1.2.12"),sQuery(id+"F1.wireOp",EDGE,"E7.1.2.13"),sQuery(id+"F1.wireOp",EDGE,"E7.1.2.23"),sQuery(id+"F1.wireOp",EDGE,"E7.1.2.27"),sQuery(id+"F1.wireOp",EDGE,"E7.1.2.29"),sQuery(id+"F1.wireOp",EDGE,"E7.1.2.30"),sQuery(id+"F1.wireOp",EDGE,"E7.1.2.31")])],"isStart":false});
            var Q16;
            Q16=makeQuery(id+"F3.opExtrude","CAP_FACE",FACE,{"disambiguationData":[OSD([sQuery(id+"F1.wireOp",EDGE,"E7.1.3.0"),sQuery(id+"F1.wireOp",EDGE,"E7.1.3.1"),sQuery(id+"F1.wireOp",EDGE,"E7.1.3.4"),sQuery(id+"F1.wireOp",EDGE,"E7.1.3.7"),sQuery(id+"F1.wireOp",EDGE,"E7.1.3.8"),sQuery(id+"F1.wireOp",EDGE,"E7.1.3.18"),sQuery(id+"F1.wireOp",EDGE,"E7.1.3.19"),sQuery(id+"F1.wireOp",EDGE,"E7.1.3.24")])],"isStart":false});
            var Q17;
            Q17=makeQuery(id+"F3.opExtrude","CAP_FACE",FACE,{"disambiguationData":[OSD([sQuery(id+"F1.wireOp",EDGE,"E7.1.3.5"),sQuery(id+"F1.wireOp",EDGE,"E7.1.3.12"),sQuery(id+"F1.wireOp",EDGE,"E7.1.3.13"),sQuery(id+"F1.wireOp",EDGE,"E7.1.3.23"),sQuery(id+"F1.wireOp",EDGE,"E7.1.3.27"),sQuery(id+"F1.wireOp",EDGE,"E7.1.3.29"),sQuery(id+"F1.wireOp",EDGE,"E7.1.3.30"),sQuery(id+"F1.wireOp",EDGE,"E7.1.3.31")])],"isStart":false});
            var Q18;
            Q18=makeQuery(id+"F3.opExtrude","CAP_FACE",FACE,{"disambiguationData":[OSD([sQuery(id+"F1.wireOp",EDGE,"E7.1.4.0"),sQuery(id+"F1.wireOp",EDGE,"E7.1.4.1"),sQuery(id+"F1.wireOp",EDGE,"E7.1.4.4"),sQuery(id+"F1.wireOp",EDGE,"E7.1.4.7"),sQuery(id+"F1.wireOp",EDGE,"E7.1.4.8"),sQuery(id+"F1.wireOp",EDGE,"E7.1.4.18"),sQuery(id+"F1.wireOp",EDGE,"E7.1.4.19"),sQuery(id+"F1.wireOp",EDGE,"E7.1.4.24")])],"isStart":false});
            var Q19;
            Q19=makeQuery(id+"F3.opExtrude","CAP_FACE",FACE,{"disambiguationData":[OSD([sQuery(id+"F1.wireOp",EDGE,"E7.1.4.5"),sQuery(id+"F1.wireOp",EDGE,"E7.1.4.12"),sQuery(id+"F1.wireOp",EDGE,"E7.1.4.13"),sQuery(id+"F1.wireOp",EDGE,"E7.1.4.23"),sQuery(id+"F1.wireOp",EDGE,"E7.1.4.27"),sQuery(id+"F1.wireOp",EDGE,"E7.1.4.29"),sQuery(id+"F1.wireOp",EDGE,"E7.1.4.30"),sQuery(id+"F1.wireOp",EDGE,"E7.1.4.31")])],"isStart":false});
            var Q20;
            Q20=makeQuery(id+"F3.opExtrude","CAP_FACE",FACE,{"disambiguationData":[OSD([sQuery(id+"F1.wireOp",EDGE,"E7.2.0.0"),sQuery(id+"F1.wireOp",EDGE,"E7.2.0.1"),sQuery(id+"F1.wireOp",EDGE,"E7.2.0.4"),sQuery(id+"F1.wireOp",EDGE,"E7.2.0.7"),sQuery(id+"F1.wireOp",EDGE,"E7.2.0.8"),sQuery(id+"F1.wireOp",EDGE,"E7.2.0.18"),sQuery(id+"F1.wireOp",EDGE,"E7.2.0.19"),sQuery(id+"F1.wireOp",EDGE,"E7.2.0.24")])],"isStart":false});
            var Q21;
            Q21=makeQuery(id+"F3.opExtrude","CAP_FACE",FACE,{"disambiguationData":[OSD([sQuery(id+"F1.wireOp",EDGE,"E7.2.0.5"),sQuery(id+"F1.wireOp",EDGE,"E7.2.0.12"),sQuery(id+"F1.wireOp",EDGE,"E7.2.0.13"),sQuery(id+"F1.wireOp",EDGE,"E7.2.0.23"),sQuery(id+"F1.wireOp",EDGE,"E7.2.0.27"),sQuery(id+"F1.wireOp",EDGE,"E7.2.0.29"),sQuery(id+"F1.wireOp",EDGE,"E7.2.0.30"),sQuery(id+"F1.wireOp",EDGE,"E7.2.0.31")])],"isStart":false});
            var Q22;
            Q22=makeQuery(id+"F3.opExtrude","CAP_FACE",FACE,{"disambiguationData":[OSD([sQuery(id+"F1.wireOp",EDGE,"E7.2.1.0"),sQuery(id+"F1.wireOp",EDGE,"E7.2.1.1"),sQuery(id+"F1.wireOp",EDGE,"E7.2.1.4"),sQuery(id+"F1.wireOp",EDGE,"E7.2.1.7"),sQuery(id+"F1.wireOp",EDGE,"E7.2.1.8"),sQuery(id+"F1.wireOp",EDGE,"E7.2.1.18"),sQuery(id+"F1.wireOp",EDGE,"E7.2.1.19"),sQuery(id+"F1.wireOp",EDGE,"E7.2.1.24")])],"isStart":false});
            var Q23;
            Q23=makeQuery(id+"F3.opExtrude","CAP_FACE",FACE,{"disambiguationData":[OSD([sQuery(id+"F1.wireOp",EDGE,"E7.2.1.5"),sQuery(id+"F1.wireOp",EDGE,"E7.2.1.12"),sQuery(id+"F1.wireOp",EDGE,"E7.2.1.13"),sQuery(id+"F1.wireOp",EDGE,"E7.2.1.23"),sQuery(id+"F1.wireOp",EDGE,"E7.2.1.27"),sQuery(id+"F1.wireOp",EDGE,"E7.2.1.29"),sQuery(id+"F1.wireOp",EDGE,"E7.2.1.30"),sQuery(id+"F1.wireOp",EDGE,"E7.2.1.31")])],"isStart":false});
            var Q24;
            Q24=makeQuery(id+"F3.opExtrude","CAP_FACE",FACE,{"disambiguationData":[OSD([sQuery(id+"F1.wireOp",EDGE,"E7.2.2.0"),sQuery(id+"F1.wireOp",EDGE,"E7.2.2.1"),sQuery(id+"F1.wireOp",EDGE,"E7.2.2.4"),sQuery(id+"F1.wireOp",EDGE,"E7.2.2.7"),sQuery(id+"F1.wireOp",EDGE,"E7.2.2.8"),sQuery(id+"F1.wireOp",EDGE,"E7.2.2.18"),sQuery(id+"F1.wireOp",EDGE,"E7.2.2.19"),sQuery(id+"F1.wireOp",EDGE,"E7.2.2.24")])],"isStart":false});
            var Q25;
            Q25=makeQuery(id+"F3.opExtrude","CAP_FACE",FACE,{"disambiguationData":[OSD([sQuery(id+"F1.wireOp",EDGE,"E7.2.2.5"),sQuery(id+"F1.wireOp",EDGE,"E7.2.2.12"),sQuery(id+"F1.wireOp",EDGE,"E7.2.2.13"),sQuery(id+"F1.wireOp",EDGE,"E7.2.2.23"),sQuery(id+"F1.wireOp",EDGE,"E7.2.2.27"),sQuery(id+"F1.wireOp",EDGE,"E7.2.2.29"),sQuery(id+"F1.wireOp",EDGE,"E7.2.2.30"),sQuery(id+"F1.wireOp",EDGE,"E7.2.2.31")])],"isStart":false});
            var Q26;
            Q26=makeQuery(id+"F3.opExtrude","CAP_FACE",FACE,{"disambiguationData":[OSD([sQuery(id+"F1.wireOp",EDGE,"E7.2.3.0"),sQuery(id+"F1.wireOp",EDGE,"E7.2.3.1"),sQuery(id+"F1.wireOp",EDGE,"E7.2.3.4"),sQuery(id+"F1.wireOp",EDGE,"E7.2.3.7"),sQuery(id+"F1.wireOp",EDGE,"E7.2.3.8"),sQuery(id+"F1.wireOp",EDGE,"E7.2.3.18"),sQuery(id+"F1.wireOp",EDGE,"E7.2.3.19"),sQuery(id+"F1.wireOp",EDGE,"E7.2.3.24")])],"isStart":false});
            var Q27;
            Q27=makeQuery(id+"F3.opExtrude","CAP_FACE",FACE,{"disambiguationData":[OSD([sQuery(id+"F1.wireOp",EDGE,"E7.2.3.5"),sQuery(id+"F1.wireOp",EDGE,"E7.2.3.12"),sQuery(id+"F1.wireOp",EDGE,"E7.2.3.13"),sQuery(id+"F1.wireOp",EDGE,"E7.2.3.23"),sQuery(id+"F1.wireOp",EDGE,"E7.2.3.27"),sQuery(id+"F1.wireOp",EDGE,"E7.2.3.29"),sQuery(id+"F1.wireOp",EDGE,"E7.2.3.30"),sQuery(id+"F1.wireOp",EDGE,"E7.2.3.31")])],"isStart":false});
            var Q28;
            Q28=makeQuery(id+"F3.opExtrude","CAP_FACE",FACE,{"disambiguationData":[OSD([sQuery(id+"F1.wireOp",EDGE,"E7.2.4.0"),sQuery(id+"F1.wireOp",EDGE,"E7.2.4.1"),sQuery(id+"F1.wireOp",EDGE,"E7.2.4.4"),sQuery(id+"F1.wireOp",EDGE,"E7.2.4.7"),sQuery(id+"F1.wireOp",EDGE,"E7.2.4.8"),sQuery(id+"F1.wireOp",EDGE,"E7.2.4.18"),sQuery(id+"F1.wireOp",EDGE,"E7.2.4.19"),sQuery(id+"F1.wireOp",EDGE,"E7.2.4.24")])],"isStart":false});
            var Q29;
            Q29=makeQuery(id+"F3.opExtrude","CAP_FACE",FACE,{"disambiguationData":[OSD([sQuery(id+"F1.wireOp",EDGE,"E7.2.4.5"),sQuery(id+"F1.wireOp",EDGE,"E7.2.4.12"),sQuery(id+"F1.wireOp",EDGE,"E7.2.4.13"),sQuery(id+"F1.wireOp",EDGE,"E7.2.4.23"),sQuery(id+"F1.wireOp",EDGE,"E7.2.4.27"),sQuery(id+"F1.wireOp",EDGE,"E7.2.4.29"),sQuery(id+"F1.wireOp",EDGE,"E7.2.4.30"),sQuery(id+"F1.wireOp",EDGE,"E7.2.4.31")])],"isStart":false});
            var Q30;
            Q30=makeQuery(id+"F3.opExtrude","CAP_FACE",FACE,{"disambiguationData":[OSD([sQuery(id+"F1.wireOp",EDGE,"E7.3.0.0"),sQuery(id+"F1.wireOp",EDGE,"E7.3.0.1"),sQuery(id+"F1.wireOp",EDGE,"E7.3.0.4"),sQuery(id+"F1.wireOp",EDGE,"E7.3.0.7"),sQuery(id+"F1.wireOp",EDGE,"E7.3.0.8"),sQuery(id+"F1.wireOp",EDGE,"E7.3.0.18"),sQuery(id+"F1.wireOp",EDGE,"E7.3.0.19"),sQuery(id+"F1.wireOp",EDGE,"E7.3.0.24")])],"isStart":false});
            var Q31;
            Q31=makeQuery(id+"F3.opExtrude","CAP_FACE",FACE,{"disambiguationData":[OSD([sQuery(id+"F1.wireOp",EDGE,"E7.3.0.5"),sQuery(id+"F1.wireOp",EDGE,"E7.3.0.12"),sQuery(id+"F1.wireOp",EDGE,"E7.3.0.13"),sQuery(id+"F1.wireOp",EDGE,"E7.3.0.23"),sQuery(id+"F1.wireOp",EDGE,"E7.3.0.27"),sQuery(id+"F1.wireOp",EDGE,"E7.3.0.29"),sQuery(id+"F1.wireOp",EDGE,"E7.3.0.30"),sQuery(id+"F1.wireOp",EDGE,"E7.3.0.31")])],"isStart":false});
            var Q32;
            Q32=makeQuery(id+"F3.opExtrude","CAP_FACE",FACE,{"disambiguationData":[OSD([sQuery(id+"F1.wireOp",EDGE,"E7.3.1.0"),sQuery(id+"F1.wireOp",EDGE,"E7.3.1.1"),sQuery(id+"F1.wireOp",EDGE,"E7.3.1.4"),sQuery(id+"F1.wireOp",EDGE,"E7.3.1.7"),sQuery(id+"F1.wireOp",EDGE,"E7.3.1.8"),sQuery(id+"F1.wireOp",EDGE,"E7.3.1.18"),sQuery(id+"F1.wireOp",EDGE,"E7.3.1.19"),sQuery(id+"F1.wireOp",EDGE,"E7.3.1.24")])],"isStart":false});
            var Q33;
            Q33=makeQuery(id+"F3.opExtrude","CAP_FACE",FACE,{"disambiguationData":[OSD([sQuery(id+"F1.wireOp",EDGE,"E7.3.1.5"),sQuery(id+"F1.wireOp",EDGE,"E7.3.1.12"),sQuery(id+"F1.wireOp",EDGE,"E7.3.1.13"),sQuery(id+"F1.wireOp",EDGE,"E7.3.1.23"),sQuery(id+"F1.wireOp",EDGE,"E7.3.1.27"),sQuery(id+"F1.wireOp",EDGE,"E7.3.1.29"),sQuery(id+"F1.wireOp",EDGE,"E7.3.1.30"),sQuery(id+"F1.wireOp",EDGE,"E7.3.1.31")])],"isStart":false});
            var Q34;
            Q34=makeQuery(id+"F3.opExtrude","CAP_FACE",FACE,{"disambiguationData":[OSD([sQuery(id+"F1.wireOp",EDGE,"E7.3.2.0"),sQuery(id+"F1.wireOp",EDGE,"E7.3.2.1"),sQuery(id+"F1.wireOp",EDGE,"E7.3.2.4"),sQuery(id+"F1.wireOp",EDGE,"E7.3.2.7"),sQuery(id+"F1.wireOp",EDGE,"E7.3.2.8"),sQuery(id+"F1.wireOp",EDGE,"E7.3.2.18"),sQuery(id+"F1.wireOp",EDGE,"E7.3.2.19"),sQuery(id+"F1.wireOp",EDGE,"E7.3.2.24")])],"isStart":false});
            var Q35;
            Q35=makeQuery(id+"F3.opExtrude","CAP_FACE",FACE,{"disambiguationData":[OSD([sQuery(id+"F1.wireOp",EDGE,"E7.3.2.5"),sQuery(id+"F1.wireOp",EDGE,"E7.3.2.12"),sQuery(id+"F1.wireOp",EDGE,"E7.3.2.13"),sQuery(id+"F1.wireOp",EDGE,"E7.3.2.23"),sQuery(id+"F1.wireOp",EDGE,"E7.3.2.27"),sQuery(id+"F1.wireOp",EDGE,"E7.3.2.29"),sQuery(id+"F1.wireOp",EDGE,"E7.3.2.30"),sQuery(id+"F1.wireOp",EDGE,"E7.3.2.31")])],"isStart":false});
            var Q36;
            Q36=makeQuery(id+"F3.opExtrude","CAP_FACE",FACE,{"disambiguationData":[OSD([sQuery(id+"F1.wireOp",EDGE,"E7.3.3.0"),sQuery(id+"F1.wireOp",EDGE,"E7.3.3.1"),sQuery(id+"F1.wireOp",EDGE,"E7.3.3.4"),sQuery(id+"F1.wireOp",EDGE,"E7.3.3.7"),sQuery(id+"F1.wireOp",EDGE,"E7.3.3.8"),sQuery(id+"F1.wireOp",EDGE,"E7.3.3.18"),sQuery(id+"F1.wireOp",EDGE,"E7.3.3.19"),sQuery(id+"F1.wireOp",EDGE,"E7.3.3.24")])],"isStart":false});
            var Q37;
            Q37=makeQuery(id+"F3.opExtrude","CAP_FACE",FACE,{"disambiguationData":[OSD([sQuery(id+"F1.wireOp",EDGE,"E7.3.3.5"),sQuery(id+"F1.wireOp",EDGE,"E7.3.3.12"),sQuery(id+"F1.wireOp",EDGE,"E7.3.3.13"),sQuery(id+"F1.wireOp",EDGE,"E7.3.3.23"),sQuery(id+"F1.wireOp",EDGE,"E7.3.3.27"),sQuery(id+"F1.wireOp",EDGE,"E7.3.3.29"),sQuery(id+"F1.wireOp",EDGE,"E7.3.3.30"),sQuery(id+"F1.wireOp",EDGE,"E7.3.3.31")])],"isStart":false});
            var Q38;
            Q38=makeQuery(id+"F3.opExtrude","CAP_FACE",FACE,{"disambiguationData":[OSD([sQuery(id+"F1.wireOp",EDGE,"E7.3.4.0"),sQuery(id+"F1.wireOp",EDGE,"E7.3.4.1"),sQuery(id+"F1.wireOp",EDGE,"E7.3.4.4"),sQuery(id+"F1.wireOp",EDGE,"E7.3.4.7"),sQuery(id+"F1.wireOp",EDGE,"E7.3.4.8"),sQuery(id+"F1.wireOp",EDGE,"E7.3.4.18"),sQuery(id+"F1.wireOp",EDGE,"E7.3.4.19"),sQuery(id+"F1.wireOp",EDGE,"E7.3.4.24")])],"isStart":false});
            var Q39;
            Q39=makeQuery(id+"F3.opExtrude","CAP_FACE",FACE,{"disambiguationData":[OSD([sQuery(id+"F1.wireOp",EDGE,"E7.3.4.5"),sQuery(id+"F1.wireOp",EDGE,"E7.3.4.12"),sQuery(id+"F1.wireOp",EDGE,"E7.3.4.13"),sQuery(id+"F1.wireOp",EDGE,"E7.3.4.23"),sQuery(id+"F1.wireOp",EDGE,"E7.3.4.27"),sQuery(id+"F1.wireOp",EDGE,"E7.3.4.29"),sQuery(id+"F1.wireOp",EDGE,"E7.3.4.30"),sQuery(id+"F1.wireOp",EDGE,"E7.3.4.31")])],"isStart":false});
            var Q40;
            Q40=makeQuery(id+"F3.opExtrude","CAP_FACE",FACE,{"disambiguationData":[OSD([sQuery(id+"F1.wireOp",EDGE,"E7.4.0.0"),sQuery(id+"F1.wireOp",EDGE,"E7.4.0.1"),sQuery(id+"F1.wireOp",EDGE,"E7.4.0.4"),sQuery(id+"F1.wireOp",EDGE,"E7.4.0.7"),sQuery(id+"F1.wireOp",EDGE,"E7.4.0.8"),sQuery(id+"F1.wireOp",EDGE,"E7.4.0.18"),sQuery(id+"F1.wireOp",EDGE,"E7.4.0.19"),sQuery(id+"F1.wireOp",EDGE,"E7.4.0.24")])],"isStart":false});
            var Q41;
            Q41=makeQuery(id+"F3.opExtrude","CAP_FACE",FACE,{"disambiguationData":[OSD([sQuery(id+"F1.wireOp",EDGE,"E7.4.0.5"),sQuery(id+"F1.wireOp",EDGE,"E7.4.0.12"),sQuery(id+"F1.wireOp",EDGE,"E7.4.0.13"),sQuery(id+"F1.wireOp",EDGE,"E7.4.0.23"),sQuery(id+"F1.wireOp",EDGE,"E7.4.0.27"),sQuery(id+"F1.wireOp",EDGE,"E7.4.0.29"),sQuery(id+"F1.wireOp",EDGE,"E7.4.0.30"),sQuery(id+"F1.wireOp",EDGE,"E7.4.0.31")])],"isStart":false});
            var Q42;
            Q42=makeQuery(id+"F3.opExtrude","CAP_FACE",FACE,{"disambiguationData":[OSD([sQuery(id+"F1.wireOp",EDGE,"E7.4.1.0"),sQuery(id+"F1.wireOp",EDGE,"E7.4.1.1"),sQuery(id+"F1.wireOp",EDGE,"E7.4.1.4"),sQuery(id+"F1.wireOp",EDGE,"E7.4.1.7"),sQuery(id+"F1.wireOp",EDGE,"E7.4.1.8"),sQuery(id+"F1.wireOp",EDGE,"E7.4.1.18"),sQuery(id+"F1.wireOp",EDGE,"E7.4.1.19"),sQuery(id+"F1.wireOp",EDGE,"E7.4.1.24")])],"isStart":false});
            var Q43;
            Q43=makeQuery(id+"F3.opExtrude","CAP_FACE",FACE,{"disambiguationData":[OSD([sQuery(id+"F1.wireOp",EDGE,"E7.4.1.5"),sQuery(id+"F1.wireOp",EDGE,"E7.4.1.12"),sQuery(id+"F1.wireOp",EDGE,"E7.4.1.13"),sQuery(id+"F1.wireOp",EDGE,"E7.4.1.23"),sQuery(id+"F1.wireOp",EDGE,"E7.4.1.27"),sQuery(id+"F1.wireOp",EDGE,"E7.4.1.29"),sQuery(id+"F1.wireOp",EDGE,"E7.4.1.30"),sQuery(id+"F1.wireOp",EDGE,"E7.4.1.31")])],"isStart":false});
            var Q44;
            Q44=makeQuery(id+"F3.opExtrude","CAP_FACE",FACE,{"disambiguationData":[OSD([sQuery(id+"F1.wireOp",EDGE,"E7.4.2.0"),sQuery(id+"F1.wireOp",EDGE,"E7.4.2.1"),sQuery(id+"F1.wireOp",EDGE,"E7.4.2.4"),sQuery(id+"F1.wireOp",EDGE,"E7.4.2.7"),sQuery(id+"F1.wireOp",EDGE,"E7.4.2.8"),sQuery(id+"F1.wireOp",EDGE,"E7.4.2.18"),sQuery(id+"F1.wireOp",EDGE,"E7.4.2.19"),sQuery(id+"F1.wireOp",EDGE,"E7.4.2.24")])],"isStart":false});
            var Q45;
            Q45=makeQuery(id+"F3.opExtrude","CAP_FACE",FACE,{"disambiguationData":[OSD([sQuery(id+"F1.wireOp",EDGE,"E7.4.2.5"),sQuery(id+"F1.wireOp",EDGE,"E7.4.2.12"),sQuery(id+"F1.wireOp",EDGE,"E7.4.2.13"),sQuery(id+"F1.wireOp",EDGE,"E7.4.2.23"),sQuery(id+"F1.wireOp",EDGE,"E7.4.2.27"),sQuery(id+"F1.wireOp",EDGE,"E7.4.2.29"),sQuery(id+"F1.wireOp",EDGE,"E7.4.2.30"),sQuery(id+"F1.wireOp",EDGE,"E7.4.2.31")])],"isStart":false});
            var Q46;
            Q46=makeQuery(id+"F3.opExtrude","CAP_FACE",FACE,{"disambiguationData":[OSD([sQuery(id+"F1.wireOp",EDGE,"E7.4.3.0"),sQuery(id+"F1.wireOp",EDGE,"E7.4.3.1"),sQuery(id+"F1.wireOp",EDGE,"E7.4.3.4"),sQuery(id+"F1.wireOp",EDGE,"E7.4.3.7"),sQuery(id+"F1.wireOp",EDGE,"E7.4.3.8"),sQuery(id+"F1.wireOp",EDGE,"E7.4.3.18"),sQuery(id+"F1.wireOp",EDGE,"E7.4.3.19"),sQuery(id+"F1.wireOp",EDGE,"E7.4.3.24")])],"isStart":false});
            var Q47;
            Q47=makeQuery(id+"F3.opExtrude","CAP_FACE",FACE,{"disambiguationData":[OSD([sQuery(id+"F1.wireOp",EDGE,"E7.4.3.5"),sQuery(id+"F1.wireOp",EDGE,"E7.4.3.12"),sQuery(id+"F1.wireOp",EDGE,"E7.4.3.13"),sQuery(id+"F1.wireOp",EDGE,"E7.4.3.23"),sQuery(id+"F1.wireOp",EDGE,"E7.4.3.27"),sQuery(id+"F1.wireOp",EDGE,"E7.4.3.29"),sQuery(id+"F1.wireOp",EDGE,"E7.4.3.30"),sQuery(id+"F1.wireOp",EDGE,"E7.4.3.31")])],"isStart":false});
            var Q48;
            Q48=makeQuery(id+"F3.opExtrude","CAP_FACE",FACE,{"disambiguationData":[OSD([sQuery(id+"F1.wireOp",EDGE,"E7.4.4.0"),sQuery(id+"F1.wireOp",EDGE,"E7.4.4.1"),sQuery(id+"F1.wireOp",EDGE,"E7.4.4.4"),sQuery(id+"F1.wireOp",EDGE,"E7.4.4.7"),sQuery(id+"F1.wireOp",EDGE,"E7.4.4.8"),sQuery(id+"F1.wireOp",EDGE,"E7.4.4.18"),sQuery(id+"F1.wireOp",EDGE,"E7.4.4.19"),sQuery(id+"F1.wireOp",EDGE,"E7.4.4.24")])],"isStart":false});
            var Q49;
            Q49=makeQuery(id+"F3.opExtrude","CAP_FACE",FACE,{"disambiguationData":[OSD([sQuery(id+"F1.wireOp",EDGE,"E7.4.4.5"),sQuery(id+"F1.wireOp",EDGE,"E7.4.4.12"),sQuery(id+"F1.wireOp",EDGE,"E7.4.4.13"),sQuery(id+"F1.wireOp",EDGE,"E7.4.4.23"),sQuery(id+"F1.wireOp",EDGE,"E7.4.4.27"),sQuery(id+"F1.wireOp",EDGE,"E7.4.4.29"),sQuery(id+"F1.wireOp",EDGE,"E7.4.4.30"),sQuery(id+"F1.wireOp",EDGE,"E7.4.4.31")])],"isStart":false});
            var Q50;
            Q50=makeQuery(id+"F3.opExtrude","CAP_FACE",FACE,{"disambiguationData":[OSD([sQuery(id+"F1.wireOp",EDGE,"E7.5.0.0"),sQuery(id+"F1.wireOp",EDGE,"E7.5.0.1"),sQuery(id+"F1.wireOp",EDGE,"E7.5.0.4"),sQuery(id+"F1.wireOp",EDGE,"E7.5.0.7"),sQuery(id+"F1.wireOp",EDGE,"E7.5.0.8"),sQuery(id+"F1.wireOp",EDGE,"E7.5.0.18"),sQuery(id+"F1.wireOp",EDGE,"E7.5.0.19"),sQuery(id+"F1.wireOp",EDGE,"E7.5.0.24")])],"isStart":false});
            var Q51;
            Q51=makeQuery(id+"F3.opExtrude","CAP_FACE",FACE,{"disambiguationData":[OSD([sQuery(id+"F1.wireOp",EDGE,"E7.5.0.5"),sQuery(id+"F1.wireOp",EDGE,"E7.5.0.12"),sQuery(id+"F1.wireOp",EDGE,"E7.5.0.13"),sQuery(id+"F1.wireOp",EDGE,"E7.5.0.23"),sQuery(id+"F1.wireOp",EDGE,"E7.5.0.27"),sQuery(id+"F1.wireOp",EDGE,"E7.5.0.29"),sQuery(id+"F1.wireOp",EDGE,"E7.5.0.30"),sQuery(id+"F1.wireOp",EDGE,"E7.5.0.31")])],"isStart":false});
            var Q52;
            Q52=makeQuery(id+"F3.opExtrude","CAP_FACE",FACE,{"disambiguationData":[OSD([sQuery(id+"F1.wireOp",EDGE,"E7.5.1.0"),sQuery(id+"F1.wireOp",EDGE,"E7.5.1.1"),sQuery(id+"F1.wireOp",EDGE,"E7.5.1.4"),sQuery(id+"F1.wireOp",EDGE,"E7.5.1.7"),sQuery(id+"F1.wireOp",EDGE,"E7.5.1.8"),sQuery(id+"F1.wireOp",EDGE,"E7.5.1.18"),sQuery(id+"F1.wireOp",EDGE,"E7.5.1.19"),sQuery(id+"F1.wireOp",EDGE,"E7.5.1.24")])],"isStart":false});
            var Q53;
            Q53=makeQuery(id+"F3.opExtrude","CAP_FACE",FACE,{"disambiguationData":[OSD([sQuery(id+"F1.wireOp",EDGE,"E7.5.1.5"),sQuery(id+"F1.wireOp",EDGE,"E7.5.1.12"),sQuery(id+"F1.wireOp",EDGE,"E7.5.1.13"),sQuery(id+"F1.wireOp",EDGE,"E7.5.1.23"),sQuery(id+"F1.wireOp",EDGE,"E7.5.1.27"),sQuery(id+"F1.wireOp",EDGE,"E7.5.1.29"),sQuery(id+"F1.wireOp",EDGE,"E7.5.1.30"),sQuery(id+"F1.wireOp",EDGE,"E7.5.1.31")])],"isStart":false});
            var Q54;
            Q54=makeQuery(id+"F3.opExtrude","CAP_FACE",FACE,{"disambiguationData":[OSD([sQuery(id+"F1.wireOp",EDGE,"E7.5.2.0"),sQuery(id+"F1.wireOp",EDGE,"E7.5.2.1"),sQuery(id+"F1.wireOp",EDGE,"E7.5.2.4"),sQuery(id+"F1.wireOp",EDGE,"E7.5.2.7"),sQuery(id+"F1.wireOp",EDGE,"E7.5.2.8"),sQuery(id+"F1.wireOp",EDGE,"E7.5.2.18"),sQuery(id+"F1.wireOp",EDGE,"E7.5.2.19"),sQuery(id+"F1.wireOp",EDGE,"E7.5.2.24")])],"isStart":false});
            var Q55;
            Q55=makeQuery(id+"F3.opExtrude","CAP_FACE",FACE,{"disambiguationData":[OSD([sQuery(id+"F1.wireOp",EDGE,"E7.5.2.5"),sQuery(id+"F1.wireOp",EDGE,"E7.5.2.12"),sQuery(id+"F1.wireOp",EDGE,"E7.5.2.13"),sQuery(id+"F1.wireOp",EDGE,"E7.5.2.23"),sQuery(id+"F1.wireOp",EDGE,"E7.5.2.27"),sQuery(id+"F1.wireOp",EDGE,"E7.5.2.29"),sQuery(id+"F1.wireOp",EDGE,"E7.5.2.30"),sQuery(id+"F1.wireOp",EDGE,"E7.5.2.31")])],"isStart":false});
            var Q56;
            Q56=makeQuery(id+"F3.opExtrude","CAP_FACE",FACE,{"disambiguationData":[OSD([sQuery(id+"F1.wireOp",EDGE,"E7.5.3.0"),sQuery(id+"F1.wireOp",EDGE,"E7.5.3.1"),sQuery(id+"F1.wireOp",EDGE,"E7.5.3.4"),sQuery(id+"F1.wireOp",EDGE,"E7.5.3.7"),sQuery(id+"F1.wireOp",EDGE,"E7.5.3.8"),sQuery(id+"F1.wireOp",EDGE,"E7.5.3.18"),sQuery(id+"F1.wireOp",EDGE,"E7.5.3.19"),sQuery(id+"F1.wireOp",EDGE,"E7.5.3.24")])],"isStart":false});
            var Q57;
            Q57=makeQuery(id+"F3.opExtrude","CAP_FACE",FACE,{"disambiguationData":[OSD([sQuery(id+"F1.wireOp",EDGE,"E7.5.3.5"),sQuery(id+"F1.wireOp",EDGE,"E7.5.3.12"),sQuery(id+"F1.wireOp",EDGE,"E7.5.3.13"),sQuery(id+"F1.wireOp",EDGE,"E7.5.3.23"),sQuery(id+"F1.wireOp",EDGE,"E7.5.3.27"),sQuery(id+"F1.wireOp",EDGE,"E7.5.3.29"),sQuery(id+"F1.wireOp",EDGE,"E7.5.3.30"),sQuery(id+"F1.wireOp",EDGE,"E7.5.3.31")])],"isStart":false});
            var Q58;
            Q58=makeQuery(id+"F3.opExtrude","CAP_FACE",FACE,{"disambiguationData":[OSD([sQuery(id+"F1.wireOp",EDGE,"E7.5.4.0"),sQuery(id+"F1.wireOp",EDGE,"E7.5.4.1"),sQuery(id+"F1.wireOp",EDGE,"E7.5.4.4"),sQuery(id+"F1.wireOp",EDGE,"E7.5.4.7"),sQuery(id+"F1.wireOp",EDGE,"E7.5.4.8"),sQuery(id+"F1.wireOp",EDGE,"E7.5.4.18"),sQuery(id+"F1.wireOp",EDGE,"E7.5.4.19"),sQuery(id+"F1.wireOp",EDGE,"E7.5.4.24")])],"isStart":false});
            var Q59;
            Q59=makeQuery(id+"F3.opExtrude","CAP_FACE",FACE,{"disambiguationData":[OSD([sQuery(id+"F1.wireOp",EDGE,"E7.5.4.5"),sQuery(id+"F1.wireOp",EDGE,"E7.5.4.12"),sQuery(id+"F1.wireOp",EDGE,"E7.5.4.13"),sQuery(id+"F1.wireOp",EDGE,"E7.5.4.23"),sQuery(id+"F1.wireOp",EDGE,"E7.5.4.27"),sQuery(id+"F1.wireOp",EDGE,"E7.5.4.29"),sQuery(id+"F1.wireOp",EDGE,"E7.5.4.30"),sQuery(id+"F1.wireOp",EDGE,"E7.5.4.31")])],"isStart":false});
            fillet(context, id + "F4", {"entities" : qUnion([Q0, Q1, Q2, Q3, Q4, Q5, Q6, Q7, Q8, Q9, Q10, Q11, Q12, Q13, Q14, Q15, Q16, Q17, Q18, Q19, Q20, Q21, Q22, Q23, Q24, Q25, Q26, Q27, Q28, Q29, Q30, Q31, Q32, Q33, Q34, Q35, Q36, Q37, Q38, Q39, Q40, Q41, Q42, Q43, Q44, Q45, Q46, Q47, Q48, Q49, Q50, Q51, Q52, Q53, Q54, Q55, Q56, Q57, Q58, Q59]), "radius" : 1.84 * mm, "tangentPropagation" : true, "allowEdgeOverflow" : false});
        }
        {
            var Q0;
            Q0=makeQuery(id+"F2.opExtrude","SWEPT_FACE",FACE,{"disambiguationData":[OSD([sQuery(id+"F0.wireOp",EDGE,"E0.right")])]});
            var Q1;
            Q1=makeQuery(id+"F2.opExtrude","SWEPT_FACE",FACE,{"disambiguationData":[OSD([sQuery(id+"F0.wireOp",EDGE,"E0.left")])]});
            var Q2;
            Q2=makeQuery(id+"F2.opExtrude","SWEPT_FACE",FACE,{"disambiguationData":[OSD([sQuery(id+"F0.wireOp",EDGE,"E1.filletArc")])]});
            var Q3;
            Q3=makeQuery(id+"F2.opExtrude","SWEPT_FACE",FACE,{"disambiguationData":[OSD([sQuery(id+"F0.wireOp",EDGE,"E0.bottom")])]});
            var Q4;
            {var subQ0=sQuery(id+"F1.wireOp",EDGE,"E6.15");var subQ1=sQuery(id+"F1.wireOp",EDGE,"E6.14");var subQ2=sQuery(id+"F1.wireOp",EDGE,"E6.13");var subQ3=sQuery(id+"F1.wireOp",EDGE,"E6.12");var subQ4=sQuery(id+"F1.wireOp",EDGE,"E6.6");var subQ5=sQuery(id+"F1.wireOp",EDGE,"E6.5");var subQ6=sQuery(id+"F1.wireOp",EDGE,"E6.4");var subQ7=sQuery(id+"F1.wireOp",EDGE,"E6.0");var subQ8=sQuery(id+"F1.wireOp",EDGE,"E5.15");var subQ9=sQuery(id+"F1.wireOp",EDGE,"E5.14");var subQ10=sQuery(id+"F1.wireOp",EDGE,"E5.13");var subQ11=sQuery(id+"F1.wireOp",EDGE,"E5.10");var subQ12=sQuery(id+"F1.wireOp",EDGE,"E5.9");var subQ13=sQuery(id+"F1.wireOp",EDGE,"E5.8");var subQ14=sQuery(id+"F1.wireOp",EDGE,"E5.3");var subQ15=sQuery(id+"F1.wireOp",EDGE,"E5.0");Q4=makeQuery(id+"F3.boolean.opBoolean","MERGE",FACE,{"derivedFrom":[makeQuery(id+"F2.opExtrude","CAP_FACE",FACE,{"disambiguationData":[OSD([sQuery(id+"F0.wireOp",EDGE,"E0.bottom"),sQuery(id+"F0.wireOp",EDGE,"E0.top"),sQuery(id+"F0.wireOp",EDGE,"E0.left"),sQuery(id+"F0.wireOp",EDGE,"E0.right"),sQuery(id+"F0.wireOp",EDGE,"E1.filletArc"),sQuery(id+"F0.wireOp",EDGE,"E2.filletArc"),sQuery(id+"F0.wireOp",EDGE,"E3.filletArc"),sQuery(id+"F0.wireOp",EDGE,"E4.filletArc"),subQ15,subQ14,subQ13,subQ12,subQ11,subQ10,subQ9,subQ8,subQ7,subQ6,subQ5,subQ4,subQ3,subQ2,subQ1,subQ0])],"isStart":true}),makeQuery(id+"F3.opExtrude","CAP_FACE",FACE,{"disambiguationData":[OSD([subQ15,subQ14,subQ13,subQ12,subQ11,subQ10,subQ9,subQ8])],"isStart":true}),makeQuery(id+"F3.opExtrude","CAP_FACE",FACE,{"disambiguationData":[OSD([subQ7,subQ6,subQ5,subQ4,subQ3,subQ2,subQ1,subQ0])],"isStart":true})]});}
            var Q5;
            Q5=makeQuery(id+"F2.opExtrude","SWEPT_FACE",FACE,{"disambiguationData":[OSD([sQuery(id+"F0.wireOp",EDGE,"E3.filletArc")])]});
            var Q6;
            Q6=makeQuery(id+"F2.opExtrude","SWEPT_FACE",FACE,{"disambiguationData":[OSD([sQuery(id+"F0.wireOp",EDGE,"E2.filletArc")])]});
            var Q7;
            Q7=makeQuery(id+"F2.opExtrude","SWEPT_FACE",FACE,{"disambiguationData":[OSD([sQuery(id+"F0.wireOp",EDGE,"E0.top")])]});
            var Q8;
            Q8=makeQuery(id+"F2.opExtrude","SWEPT_FACE",FACE,{"disambiguationData":[OSD([sQuery(id+"F0.wireOp",EDGE,"E4.filletArc")])]});
            shell(context, id + "F5", {"entities" : qUnion([Q0, Q1, Q2, Q3, Q4, Q5, Q6, Q7, Q8]), "thickness" : 0.23 * mm});
        }
        {
            var Q0;
            Q0=makeQuery(id+"F2.opExtrude","CAP_FACE",FACE,{"disambiguationData":[OSD([sQuery(id+"F0.wireOp",EDGE,"E0.bottom"),sQuery(id+"F0.wireOp",EDGE,"E0.top"),sQuery(id+"F0.wireOp",EDGE,"E0.left"),sQuery(id+"F0.wireOp",EDGE,"E0.right"),sQuery(id+"F0.wireOp",EDGE,"E1.filletArc"),sQuery(id+"F0.wireOp",EDGE,"E2.filletArc"),sQuery(id+"F0.wireOp",EDGE,"E3.filletArc"),sQuery(id+"F0.wireOp",EDGE,"E4.filletArc"),sQuery(id+"F1.wireOp",EDGE,"E5.0"),sQuery(id+"F1.wireOp",EDGE,"E5.3"),sQuery(id+"F1.wireOp",EDGE,"E5.8"),sQuery(id+"F1.wireOp",EDGE,"E5.9"),sQuery(id+"F1.wireOp",EDGE,"E5.10"),sQuery(id+"F1.wireOp",EDGE,"E5.13"),sQuery(id+"F1.wireOp",EDGE,"E5.14"),sQuery(id+"F1.wireOp",EDGE,"E5.15"),sQuery(id+"F1.wireOp",EDGE,"E6.0"),sQuery(id+"F1.wireOp",EDGE,"E6.4"),sQuery(id+"F1.wireOp",EDGE,"E6.5"),sQuery(id+"F1.wireOp",EDGE,"E6.6"),sQuery(id+"F1.wireOp",EDGE,"E6.12"),sQuery(id+"F1.wireOp",EDGE,"E6.13"),sQuery(id+"F1.wireOp",EDGE,"E6.14"),sQuery(id+"F1.wireOp",EDGE,"E6.15")])],"isStart":false});
            chamfer(context, id + "F6", {"entities" : qUnion([Q0]), "width" : 2.54 * mm, "tangentPropagation" : true});
        }
    });
